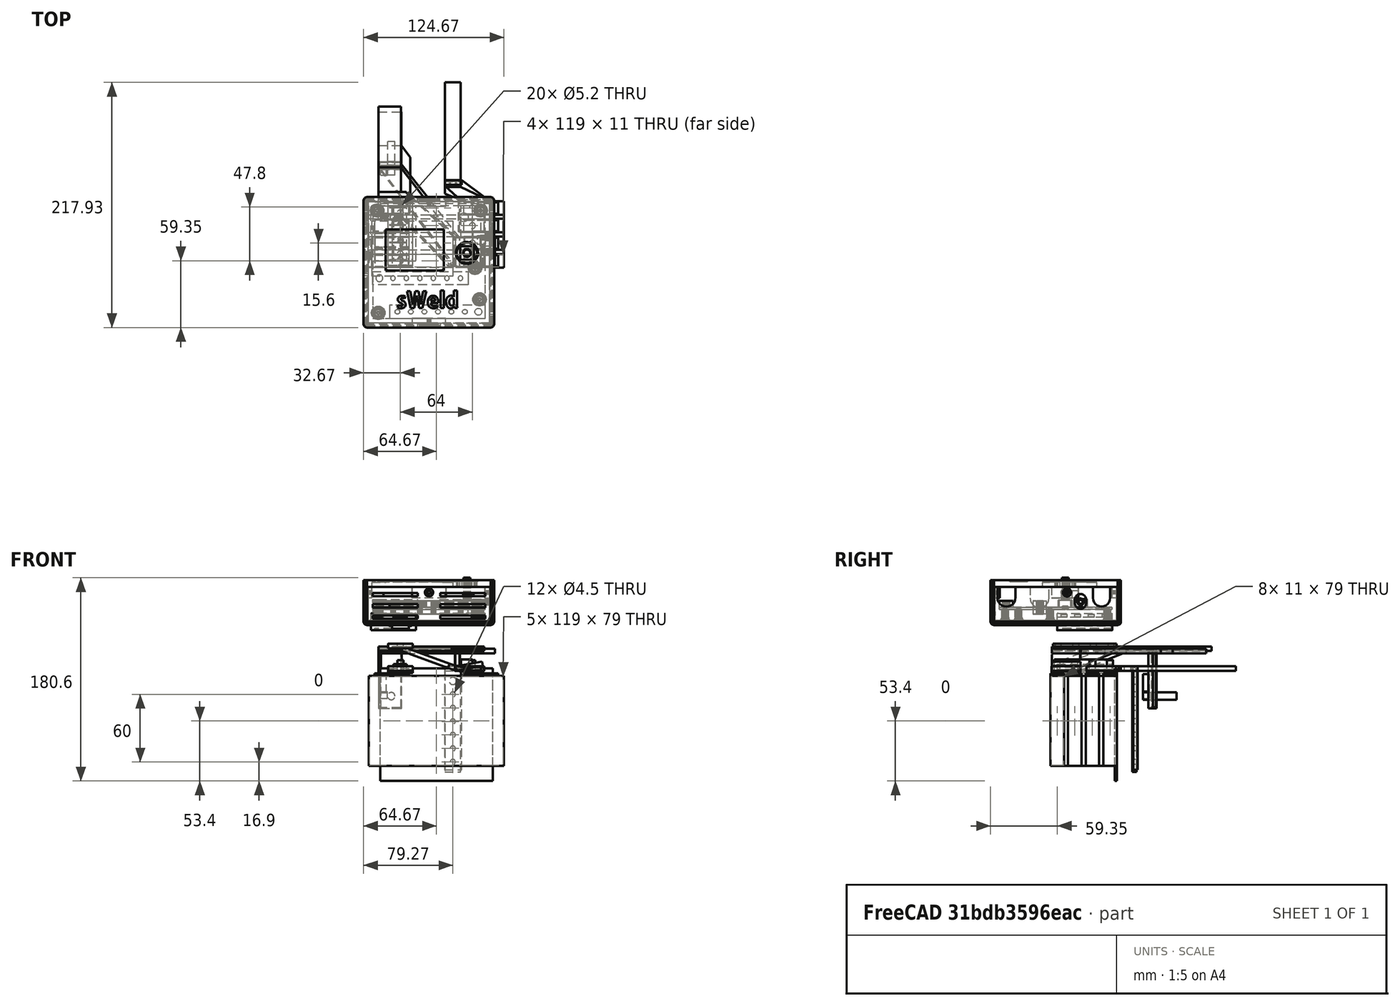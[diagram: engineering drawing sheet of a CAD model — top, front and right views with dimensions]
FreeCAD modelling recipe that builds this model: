
FCSTD DOCUMENT  (FreeCAD 0.17R13541 (Git))
Label: stm32welder-3d
License: CreativeCommons Attribution-NonCommercial-ShareAlike
LicenseURL: http://creativecommons.org/licenses/by-nc-sa/4.0/
objects: Drawing::FeatureViewPython×114, Part::Feature×45, Part::Box×32, Drawing::FeatureViewPart×32, Part::FeaturePython×13, Part::Fillet×11, Part::MultiFuse×11, Drawing::FeaturePage×10, Part::Cylinder×7, Part::Cut×6, Raytracing::RayFeature×5, App::DocumentObjectGroup×4, Part::Chamfer×4, Sketcher::SketchObject×3, App::Part×2, Raytracing::RayProject×1
note: 132 computed .brp shape members not serialized (recipe doc carries the construction recipe); baked Part::Feature solids carry a one-line shape summary decoded from their .brp

FEATURE [Part::Box] Box  label="立方体"
  AttacherType = Attacher::AttachEngine3D
  Height = 80
  Length = 120
  Placement = pos=(-84.5,0,-80) rot=(0,0,1;0rad)
  Width = 12
FEATURE [Part::Box] Box001  label="dianpian"
  AttacherType = Attacher::AttachEngine3D
  Height = 2.25
  Length = 30.5
  Width = 12
FEATURE [Part::Box] Box002  label="dianpian001"
  AttacherType = Attacher::AttachEngine3D
  Height = 2.25
  Length = 15
  Placement = pos=(0,0,2.25) rot=(0,0,1;0rad)
  Width = 12
FEATURE [Part::Fillet] Fillet
  Base = -> Box002
  Edges = 2 edges r=2: [Edge2,Edge6]
FEATURE [Part::Cylinder] Cylinder  label="圆柱体"
  Angle = 360
  AttacherType = Attacher::AttachEngine3D
  Height = 10
  Placement = pos=(7.5,6,4.5) rot=(0,0,1;0rad)
  Radius = 2.7
FEATURE [Part::MultiFuse] Fusion001  label="电极001"
  Placement = pos=(-24.5,12,80) rot=(0,0,1;3.14159rad)
  Shapes = -> [Fillet,Box001,Cylinder]
FEATURE [Part::Box] Box003  label="立方体001"
  AttacherType = Attacher::AttachEngine3D
  Height = 3.3
  Length = 22
  Placement = pos=(-43,-0.2,84.5) rot=(0,0,1;0rad)
  Width = 49
FEATURE [Part::Fillet] Fillet001
  Base = -> Box003
  Edges = 4 edges r=1: [Edge1,Edge3,Edge5,Edge7]
FEATURE [Part::Fillet] Fillet002
  Base = -> Box
  Edges = 12 edges r=0.5: [Edge1,Edge2,Edge3,Edge4,Edge5,Edge6,Edge7,Edge8,Edge9,Edge10,Edge11,Edge12]
FEATURE [Part::MultiFuse] Fusion  label="电极2"
  Placement = pos=(24.5,0,80) rot=(0,0,1;0rad)
  Shapes = -> [Fillet,Box001,Cylinder,Fillet002]
FEATURE [Part::Cylinder] Cylinder001  label="圆柱体001"
  Angle = 360
  AttacherType = Attacher::AttachEngine3D
  Height = 10
  Placement = pos=(7.5,6,4.5) rot=(0,0,1;0rad)
  Radius = 2.7
FEATURE [Part::MultiFuse] Fusion002  label="1201280"
  Shapes = -> [Fusion,Fusion001,Cylinder001]
FEATURE [Part::FeaturePython] Array  # Draft array (typed FeaturePython)
  Angle = 360
  ArrayType = 0
  Axis = (0,0,1)
  Base = -> Fusion002
  Center = (0,0,0)
  Fuse = false
  IntervalAxis = (0,0,0)
  IntervalX = (1,0,0)
  IntervalY = (0,12.2,0)
  IntervalZ = (0,0,0)
  NumberPolar = 1
  NumberX = 1
  NumberY = 4
  NumberZ = 1
FEATURE [Part::Box] Box004  label="立方体002"
  AttacherType = Attacher::AttachEngine3D
  Height = 8
  Length = 11.5
  Placement = pos=(-38,-0.2,84.5) rot=(0,0,1;0rad)
  Width = 49
FEATURE [Part::Box] Box005  label="立方体003"
  AttacherType = Attacher::AttachEngine3D
  Height = 3
  Length = 15
  Placement = pos=(-39.5,-0.2,82) rot=(0,0,1;0rad)
  Width = 49
FEATURE [Part::MultiFuse] Fusion002005
  Shapes = -> [Box005,Box004,Fillet001]
FEATURE [Part::MultiFuse] Fusion002006
  Shapes = -> [Array,Fusion002005]
FEATURE [Part::Box] Box006  label="立方体004"
  AttacherType = Attacher::AttachEngine3D
  Height = 15
  Length = 40
  Placement = pos=(-58,-0.2,80.5) rot=(0,0,1;0rad)
  Width = 49
FEATURE [Part::Fillet] Fillet003
  Base = -> Box006
  Edges = 4 edges r=1: [Edge1,Edge3,Edge5,Edge7]
FEATURE [Part::Cut] Cut
  Base = -> Fillet003
  Tool = -> Fusion002006
FEATURE [Part::Box] Box007  label="电极片"
  AttacherType = Attacher::AttachEngine3D
  Height = 2.25
  Length = 30.5
  Placement = pos=(24.5,-6,40) rot=(0,0,1;0rad)
  Width = 12
FEATURE [Part::Box] Box008  label="dianpian003"
  AttacherType = Attacher::AttachEngine3D
  Height = 2.25
  Length = 15
  Placement = pos=(24.5,-5,42.25) rot=(0,0,1;0rad)
  Width = 10
FEATURE [Part::Fillet] Fillet004  label="小垫片"
  Base = -> Box008
  Edges = 2 edges r=2: [Edge2,Edge6]
FEATURE [Part::Cylinder] Cylinder002  label="圆柱体002"
  Angle = 360
  AttacherType = Attacher::AttachEngine3D
  Height = 10
  Placement = pos=(32,0,44) rot=(0,0,1;0rad)
  Radius = 2.6
FEATURE [Part::Box] Box009  label="立方体005"
  AttacherType = Attacher::AttachEngine3D
  Height = 80
  Length = 120
  Placement = pos=(-60,-6,-40) rot=(0,0,1;0rad)
  Width = 12
FEATURE [Part::Fillet] Fillet005  label="1280120"
  Base = -> Box009
  Edges = 12 edges r=0.5: [Edge1,Edge2,Edge3,Edge4,Edge5,Edge6,Edge7,Edge8,Edge9,Edge10,Edge11,Edge12]
FEATURE [Part::Box] Box010  label="立方体006"
  AttacherType = Attacher::AttachEngine3D
  Height = 3.3
  Length = 22
  Placement = pos=(-43,-0.2,84.5) rot=(0,0,1;0rad)
  Width = 49
FEATURE [Part::Fillet] Fillet006
  Base = -> Box010
  Edges = 4 edges r=1: [Edge1,Edge3,Edge5,Edge7]
FEATURE [Part::Box] Box011  label="立方体007"
  AttacherType = Attacher::AttachEngine3D
  Height = 8
  Length = 11.5
  Placement = pos=(-38,-0.2,84.5) rot=(0,0,1;0rad)
  Width = 49
FEATURE [Part::Box] Box012  label="立方体008"
  AttacherType = Attacher::AttachEngine3D
  Height = 3
  Length = 15
  Placement = pos=(-39.5,-0.2,82) rot=(0,0,1;0rad)
  Width = 49
FEATURE [Part::MultiFuse] Fusion002007
  Placement = pos=(0,0,-42) rot=(0,0,1;0rad)
  Shapes = -> [Box012,Box011,Fillet006]
FEATURE [Part::Box] Box015  label="电极片001"
  AttacherType = Attacher::AttachEngine3D
  Height = 2.25
  Length = 30
  Placement = pos=(24.75,-5,40.1) rot=(0,0,1;0rad)
  Width = 10
FEATURE [Part::Box] Box016  label="电极片002"
  AttacherType = Attacher::AttachEngine3D
  Height = 2.25
  Length = 30.5
  Placement = pos=(-55,-6,40) rot=(0,0,1;0rad)
  Width = 12
FEATURE [Part::Box] Box017  label="dianpian004"
  AttacherType = Attacher::AttachEngine3D
  Height = 2.25
  Length = 15
  Placement = pos=(-39.5,-5,42.25) rot=(0,0,1;0rad)
  Width = 10
FEATURE [Part::Fillet] Fillet007  label="小垫片001"
  Base = -> Box017
  Edges = 2 edges r=2: [Edge2,Edge6]
FEATURE [Part::Cylinder] Cylinder003  label="圆柱体003"
  Angle = 360
  AttacherType = Attacher::AttachEngine3D
  Height = 10
  Placement = pos=(-32,0,44) rot=(0,0,1;0rad)
  Radius = 2.6
FEATURE [Part::Box] Box018  label="电极片003"
  AttacherType = Attacher::AttachEngine3D
  Height = 2.25
  Length = 30
  Placement = pos=(-54.75,-5,40.1) rot=(0,0,1;0rad)
  Width = 10
FEATURE [App::DocumentObjectGroup] ___  label="垫片1"
  Group = -> [Fillet004,Box015,Cylinder002,Box007]
FEATURE [App::DocumentObjectGroup] ___001  label="垫片"
  Group = -> [Fillet007,Box018,Cylinder003,Box016]
FEATURE [Part::Box] Box019  label="立方体009"
  AttacherType = Attacher::AttachEngine3D
  Height = 80
  Length = 120
  Placement = pos=(-60,-6,-40) rot=(0,0,1;0rad)
  Width = 58.7
FEATURE [Part::Feature] Fusion002008001  label="Fusion002009"
  shape: bbox 120 x 12 x 94 mm, 57 faces (baked)
FEATURE [Part::FeaturePython] Array001  # Draft array (typed FeaturePython)
  Angle = 360
  ArrayType = 0
  Axis = (0,0,1)
  Base = -> Fusion002008001
  Center = (0,0,0)
  Fuse = false
  IntervalAxis = (0,0,0)
  IntervalX = (1,0,0)
  IntervalY = (0,15.6,0)
  IntervalZ = (0,0,0)
  NumberPolar = 1
  NumberX = 1
  NumberY = 4
  NumberZ = 1
FEATURE [Part::Feature] Fusion002008002  label="Fusion002010"
  Placement = pos=(0,0,0) rot=(0,0,1;3.14159rad)
  shape: bbox 120 x 12 x 94 mm, 57 faces (baked)
FEATURE [Part::Feature] Fusion002008003  label="Fusion002011"
  Placement = pos=(0,15.6,0) rot=(0,0,1;3.14159rad)
  shape: bbox 120 x 12 x 94 mm, 57 faces (baked)
FEATURE [Part::Feature] Fusion002008004  label="Fusion002012"
  Placement = pos=(0,31.2,0) rot=(0,0,1;0rad)
  shape: bbox 120 x 12 x 94 mm, 57 faces (baked)
FEATURE [Part::Feature] Fusion002008005  label="Fusion002013"
  Placement = pos=(0,46.8,0) rot=(0,0,1;0rad)
  shape: bbox 120 x 12 x 94 mm, 57 faces (baked)
FEATURE [Raytracing::RayFeature] Fusion002008002_View
  Result = <blob: 50830 chars omitted>
  Source = -> Fusion002008002
  Transparency = 0
FEATURE [Raytracing::RayFeature] Fusion002008003_View
  Result = <blob: 51430 chars omitted>
  Source = -> Fusion002008003
  Transparency = 0
FEATURE [Raytracing::RayFeature] Fusion002008004_View
  Result = <blob: 48512 chars omitted>
  Source = -> Fusion002008004
  Transparency = 0
FEATURE [Raytracing::RayFeature] Fusion002008005_View
  Result = <blob: 48514 chars omitted>
  Source = -> Fusion002008005
  Transparency = 0
FEATURE [Raytracing::RayFeature] Box019_View
  Result = <blob: 2730 chars omitted>
  Source = -> Box019
  Transparency = 0
FEATURE [Raytracing::RayProject] PovProject
  Camera = // declares position and view direction\n\n// Generated by FreeCAD (http://www.freecadweb.org/)\n#declare cam_location =  <-28.5232,128.515,-118.34>;\n#declare cam_look_at  = <-1.61992,1.61848,13.5845>;\n#declare cam_sky      = <0.137048,0.727723,0.672039>;\n#declare cam_angle    = 45; \ncamera {\n  location  cam_location\n  look_at   cam_look_at\n  sky       cam_sky\n  angle     cam_angle \n  right x*2560/1920\n}
  Group = -> [Fusion002008002_View,Fusion002008003_View,Fusion002008004_View,Fusion002008005_View,Box019_View]
  Template = <path>
FEATURE [Part::Feature] Part__Feature  label="PCB-1"
  Placement = pos=(-56.6699,-51.3757,99.2) rot=(0,0,1;0rad)
  shape: bbox 100 x 100 x 1.6 mm, 576 faces (baked)
FEATURE [Part::Feature] Part__Feature001  label="300A\X2\4fdd9669\X0\-1"
  Placement = pos=(-47.0399,30.0255,103.8) rot=(0,0,1;0rad)
  shape: bbox 80.8 x 19.2 x 9 mm, 223 faces, 0 solids (baked)
FEATURE [Part::Feature] Part__Feature002  label="铜条1"
  Placement = pos=(28.3301,-21.5457,106.8) rot=(0,0.707107,-0.707107;3.14159rad)
  shape: bbox 85 x 12 x 6 mm, 478 faces (baked)
FEATURE [Part::Feature] Part__Feature003  label="铜条2"
  Placement = pos=(-41.6699,-51.3757,100.8) rot=(1,0,0;1.5708rad)
  shape: bbox 85 x 12 x 6 mm, 478 faces (baked)
FEATURE [Part::Feature] Part__Feature004  label="cross recessed hex bolts indentation gb-1"
  Placement = pos=(37.3301,-45.3757,114.971) rot=(0.367338,0.854474,-0.367338;1.72742rad)
  shape: bbox 11.23 x 11.07 x 14 mm, 1805 faces, 0 solids (baked)
FEATURE [Part::Feature] Part__Feature005  label="cross recessed hex bolts indentation gb-2"
  Placement = pos=(-50.6699,-15.5457,113.264) rot=(-0.550865,0.626973,0.550865;2.02156rad)
  shape: bbox 10.66 x 11.45 x 14 mm, 1805 faces, 0 solids (baked)
FEATURE [Part::Feature] Part__Feature006  label="plain washers-xl series-grade c1 gb-1"
  Placement = pos=(24.3601,38.5743,103.8) rot=(0,0,1;0.568241rad)
  shape: bbox 19.99 x 19.99 x 3 mm, 244 faces, 0 solids (baked)
FEATURE [Part::Feature] Part__Feature007  label="plain washers-xl series-grade c1 gb-2"
  Placement = pos=(-36.8399,38.5743,103.8) rot=(0,0,1;0rad)
  shape: bbox 19.99 x 19.99 x 3 mm, 244 faces, 0 solids (baked)
FEATURE [Part::Feature] Part__Feature008  label="18mm\X2\94dc67f1\X0\-1"
  Placement = pos=(-49.2499,-6.10568,100.8) rot=(1,0,0;1.5708rad)
  shape: bbox 4.33 x 5 x 18 mm, 90 faces, 0 solids (baked)
FEATURE [Part::Feature] Part__Feature009  label="18mm\X2\94dc67f1\X0\-2"
  Placement = pos=(-49.2499,24.8943,100.8) rot=(1,0,0;1.5708rad)
  shape: bbox 4.33 x 5 x 18 mm, 90 faces, 0 solids (baked)
FEATURE [Part::Feature] Part__Feature010  label="18mm\X2\94dc67f1\X0\-3"
  Placement = pos=(10.7501,-6.10568,100.8) rot=(1,0,0;1.5708rad)
  shape: bbox 4.33 x 5 x 18 mm, 90 faces, 0 solids (baked)
FEATURE [Part::Feature] Part__Feature011  label="18mm\X2\94dc67f1\X0\-4"
  Placement = pos=(10.7501,24.8943,100.8) rot=(1,0,0;1.5708rad)
  shape: bbox 4.33 x 5 x 18 mm, 90 faces, 0 solids (baked)
FEATURE [Part::Feature] Part__Feature012  label="外壳"
  Placement = pos=(-56.6699,-51.6162,89.2) rot=(0,0,1;0rad)
  shape: bbox 116 x 116 x 34 mm, 3868 faces (baked)
FEATURE [Part::Feature] Part__Feature013  label="盖子"
  Placement = pos=(-64.6699,-59.3507,119.2) rot=(1,0,0;1.5708rad)
  shape: bbox 116 x 116 x 16 mm, 1294 faces (baked)
FEATURE [Part::Feature] Part__Feature014  label="2.0IPS-2"
  Placement = pos=(-52.2499,-10.1057,118.8) rot=(1,0,0;1.5708rad)
  shape: bbox 66 x 39 x 3.8 mm, 322 faces, 0 solids (baked)
FEATURE [Part::Feature] Part__Feature015  label="EC11-2"
  Placement = pos=(21.1801,0.954319,100.8) rot=(1,0,0;1.5708rad)
  shape: bbox 12 x 12 x 26.4 mm, 312 faces (baked)
FEATURE [Part::Feature] Part__Feature016  label="编码开关帽"
  Placement = pos=(27.1801,6.95432,115.2) rot=(0.098915,0.703639,0.703639;2.9444rad)
  shape: bbox 19.8 x 19.79 x 22.36 mm, 3852 faces, 0 solids (baked)
FEATURE [Part::Feature] Part__Feature017  label="hex flange bolts-heavy grade b gb-1"
  Placement = pos=(-36.8399,38.5743,115.068) rot=(0.395904,0.828566,-0.395904;1.75776rad)
  shape: bbox 14.19 x 14.19 x 18.6 mm, 3036 faces, 0 solids (baked)
FEATURE [Part::Feature] Part__Feature018  label="hex flange bolts-heavy grade b gb-2"
  Placement = pos=(24.3601,38.5743,115.493) rot=(-0.329414,0.884858,0.329414;1.69282rad)
  shape: bbox 14.2 x 14.19 x 18.6 mm, 3036 faces, 0 solids (baked)
FEATURE [Part::Feature] Part__Feature019  label="SC16-6-1"
  Placement = pos=(-70.1441,38.5743,110.61) rot=(0.57735,0.57735,0.57735;2.0944rad)
  shape: bbox 43.96 x 13 x 9 mm, 516 faces, 0 solids (baked)
FEATURE [Part::Feature] Part__Feature020  label="SC16-6-2"
  Placement = pos=(57.6643,38.5743,110.61) rot=(0.57735,-0.57735,-0.57735;2.0944rad)
  shape: bbox 43.96 x 13 x 9 mm, 516 faces, 0 solids (baked)
FEATURE [Part::Feature] Part__Feature021  label="SC16-6-4"
  Placement = pos=(-83.9741,-15.5457,110.61) rot=(0.57735,0.57735,0.57735;2.0944rad)
  shape: bbox 43.96 x 13 x 9 mm, 516 faces, 0 solids (baked)
FEATURE [Part::Feature] Part__Feature022  label="SC16-6-6"
  Placement = pos=(70.6343,-45.3757,110.61) rot=(0.57735,-0.57735,-0.57735;2.0944rad)
  shape: bbox 43.96 x 13 x 9 mm, 516 faces, 0 solids (baked)
FEATURE [Part::Feature] Part__Feature023  label="3F06-2"
  Placement = pos=(43.3301,26.6243,103.3) rot=(0.57735,-0.57735,-0.57735;2.0944rad)
  shape: bbox 14.3 x 12 x 7.998 mm, 182 faces (baked)
FEATURE [Part::MultiFuse] Fusion002008006  label="电池组"
  Shapes = -> [Fusion002008005,Fusion002008004,Fusion002008003,Fusion002008002,Box019]
FEATURE [Part::Feature] Part__Feature024  label="铜条003"
  Placement = pos=(28.3301,-21.55,101) rot=(0,0.707107,-0.707107;3.14159rad)
  shape: bbox 85 x 12 x 6 mm, 478 faces (baked)
FEATURE [App::Part] _X2_9ed88ba4_X0_
  Group = -> [Part__Feature,Part__Feature001,Part__Feature002,Part__Feature003,Part__Feature004,Part__Feature005,Part__Feature006,Part__Feature007,Part__Feature008,Part__Feature009,Part__Feature010,Part__Feature011,Part__Feature012,Part__Feature013,Part__Feature014,Part__Feature015,Part__Feature016,Part__Feature017,Part__Feature018,Part__Feature019,Part__Feature020,Part__Feature021,Part__Feature022,+2 more]
  License = CC BY 3.0
  LicenseURL = http://creativecommons.org/licenses/by/3.0/
  Origin = -> Origin
FEATURE [App::Part] STM32
  Group = -> [_X2_9ed88ba4_X0_]
  License = CC BY 3.0
  LicenseURL = http://creativecommons.org/licenses/by/3.0/
  Origin = -> Origin001
  Placement = pos=(-1,-24,-15) rot=(-0.57735,0.57735,0.57735;2.0944rad)
FEATURE [Part::Box] Box020  label="立方体010"
  AttacherType = Attacher::AttachEngine3D
  Height = 4
  Length = 22
  Placement = pos=(-43,-5,44.5) rot=(0,0,1;0rad)
  Width = 56.7
FEATURE [Part::Fillet] Fillet008  label="串连铜排"
  Base = -> Box020
  Edges = 4 edges r=1: [Edge1,Edge3,Edge5,Edge7]
FEATURE [Part::Box] Box021  label="testpcb"
  AttacherType = Attacher::AttachEngine3D
  Height = 100
  Length = 100
  Placement = pos=(-50,51,-53.4) rot=(0,0,1;0rad)
  Width = 2
FEATURE [Part::Box] Box022  label="立方体011"
  AttacherType = Attacher::AttachEngine3D
  Height = 4
  Length = 22
  Placement = pos=(20.5,26.2,44.5) rot=(0,0,1;0rad)
  Width = 28.35
FEATURE [Part::Fillet] Fillet009  label="负极"
  Base = -> Box022
  Edges = 2 edges r=1: [Edge1,Edge5]
FEATURE [Part::Box] Box023  label="负极1"
  AttacherType = Attacher::AttachEngine3D
  Height = 4
  Length = 35
  Placement = pos=(7.5,54.5,44.5) rot=(0,0,1;0rad)
  Width = 11
FEATURE [Part::Box] Box024  label="负极002"
  AttacherType = Attacher::AttachEngine3D
  Height = 92
  Length = 15
  Placement = pos=(7.5,67.5,-43.5) rot=(0,0,1;0rad)
  Width = 4
FEATURE [Part::Box] Box025  label="正"
  AttacherType = Attacher::AttachEngine3D
  Height = 4
  Length = 22
  Placement = pos=(20.5,-4.9,44.5) rot=(0,0,1;0rad)
  Width = 25.5
FEATURE [Part::Box] Box026  label="负极003"
  AttacherType = Attacher::AttachEngine3D
  Height = 4
  Length = 66
  Placement = pos=(-50.2,-4.9,60) rot=(0,0,1;0rad)
  Width = 87.48
FEATURE [Part::Chamfer] Chamfer001  label="正001"
  Base = -> Box026
  Edges = 2 edges: [Edge1 r1=85.85 r2=64.7,Edge7 r1=62.2 r2=47]
FEATURE [Part::Box] Box027  label="正002"
  AttacherType = Attacher::AttachEngine3D
  Height = 15.6
  Length = 4
  Placement = pos=(16.5,-4.9,44.5) rot=(0,0,1;0rad)
  Width = 25.6
FEATURE [Part::Box] Box028  label="正003"
  AttacherType = Attacher::AttachEngine3D
  Height = 53
  Length = 18.5
  Placement = pos=(-49.2,81,11) rot=(0,0,1;0rad)
  Width = 4
FEATURE [Part::Cylinder] Cylinder004  label="圆柱体004"
  Angle = 360
  AttacherType = Attacher::AttachEngine3D
  Height = 20
  Radius = 2.25
FEATURE [Part::FeaturePython] Array002  # Draft array (typed FeaturePython)
  Angle = 360
  ArrayType = 0
  Axis = (0,0,1)
  Base = -> Cylinder004
  Center = (0,0,0)
  Fuse = false
  IntervalAxis = (0,0,0)
  IntervalX = (1,0,0)
  IntervalY = (0,12,0)
  IntervalZ = (0,0,0)
  NumberPolar = 1
  NumberX = 1
  NumberY = 6
  NumberZ = 1
FEATURE [Part::Cylinder] Cylinder005  label="圆柱体005"
  Angle = 360
  AttacherType = Attacher::AttachEngine3D
  Height = 20
  Placement = pos=(0,72,0) rot=(0,0,1;0rad)
  Radius = 3.25
FEATURE [Part::MultiFuse] Fusion002008007
  Placement = pos=(14.6,85,-36.5) rot=(1,0,0;1.5708rad)
  Shapes = -> [Cylinder005,Array002]
FEATURE [Part::Feature] Fusion002008006001  label="电池组切割"
  shape: bbox 120 x 58.8 x 94 mm, 234 faces (baked)
FEATURE [Part::MultiFuse] Fusion002008006002  label="开孔"
  Shapes = -> [Fusion002008007,Fusion002008006001]
FEATURE [Part::Feature] Cut001001  label="串联铜排"
  shape: bbox 22 x 56.7 x 4 mm, 18 faces (baked)
FEATURE [Part::MultiFuse] Fusion002008006003  label="负001"
  Shapes = -> [Box024,Fillet009]
FEATURE [App::DocumentObjectGroup] ___003  label="负"
  Group = -> [Fusion002008006003]
FEATURE [Part::Box] Box029  label="立方体012"
  AttacherType = Attacher::AttachEngine3D
  Height = 6
  Length = 6
  Placement = pos=(-49.5,76,20) rot=(0,0,1;0rad)
  Width = 5.7
FEATURE [Part::Box] Box030  label="立方体013"
  AttacherType = Attacher::AttachEngine3D
  Height = 16.7
  Length = 5
  Placement = pos=(-49.5,76,25) rot=(0,0,1;0rad)
  Width = 5.7
FEATURE [Part::Cylinder] Cylinder006  label="保险位置开孔"
  Angle = 360
  AttacherType = Attacher::AttachEngine3D
  Height = 30
  Placement = pos=(-40.1,76,22) rot=(-1,0,0;1.5708rad)
  Radius = 3.25
FEATURE [Part::Box] Box031  label="立方体014"
  AttacherType = Attacher::AttachEngine3D
  Height = 14.6
  Length = 10
  Placement = pos=(22,-2.6,40) rot=(0,0,1;0rad)
  Width = 51.7
FEATURE [Part::Feature] Fusion002008006003002001  label="正005"
  shape: bbox 91.7 x 89.9 x 53.1 mm, 32 faces (baked)
FEATURE [Part::Feature] Fusion002008006003002002001  label="开孔002"
  shape: bbox 120 x 112 x 94 mm, 237 faces, 2 solids (baked)
FEATURE [Part::Feature] Cut001002002_solid  label="正极"
  shape: bbox 91.7 x 89.9 x 53.1 mm, 37 faces (baked)
FEATURE [Part::Feature] Fusion002008006003002002002  label="负002"
  shape: bbox 35 x 45.3 x 92 mm, 24 faces (baked)
FEATURE [Part::Cut] Cut001002
  Base = -> Fusion002008006003002002002
  Tool = -> Fusion002008006002
FEATURE [Drawing::FeatureViewPart] Ortho  label="Ortho_0_0"
  Direction = (0,0,1)
  HiddenWidth = 0.15
  LineWidth = 0.35
  Rotation = 0
  Scale = 3
  ShowHiddenLines = false
  ShowSmoothLines = false
  Source = -> Cut001001
  Tolerance = 0.05
  ViewResult = <g id="Ortho_0_0"\n   transform="rotate(0,239,240.367) translate(239,240.367) scale(3,3)"\n  >\n<g   fill="none"\n   stroke="rgb(0, 0, 0)"\n   stroke-linecap="butt"\n   stroke-linejoin="miter"\n   stroke-width="0.116667"\n   transform="scale(1,-1)"\n  >\n<path id= "1" d=" M -43 -4 L -43 50.7 " />\n<path d="M-43 -4 A1 1 0 0 1 -42 -5" /><path d="M-43 50.7 A1 1 0 0 0 -42 51.7" /><path id= "4" d=" M -42 -5 L -22 -5 " />\n<path id= "5" d=" M -42 51.7 L -22 51.7 " />\n<path d="M-21 -4 A1 1 0 0 0 -22 -5" /><path d="M-21 50.7 A1 1 0 0 1 -22 51.7" /><path id= "8" d=" M -21 -4 L -21 50.7 " />\n<circle cx ="-32" cy ="3.92e-15" r ="2.6" /><circle cx ="-32" cy ="15.6" r ="2.6" /><circle cx ="-32" cy ="46.8" r ="2.6" /><circle cx ="-32" cy ="31.2" r ="2.6" /></g>\n</g>
  Visible = false
  X = 239
  Y = 240.367
FEATURE [Drawing::FeatureViewPart] Ortho001  label="Ortho_-1_0"
  Direction = (-1,0,0)
  HiddenWidth = 0.15
  LineWidth = 0.35
  Rotation = 180
  Scale = 3
  ShowHiddenLines = false
  ShowSmoothLines = false
  Source = -> Cut001001
  Tolerance = 0.05
  ViewResult = <g id="Ortho_-1_0"\n   transform="rotate(180,-79.5,240.367) translate(-79.5,240.367) scale(3,3)"\n  >\n<g   fill="none"\n   stroke="rgb(0, 0, 0)"\n   stroke-linecap="butt"\n   stroke-linejoin="miter"\n   stroke-width="0.116667"\n   transform="scale(1,-1)"\n  >\n<path id= "1" d=" M -48.5 4 L -48.5 -50.7 " />\n<path id= "2" d=" M -44.5 4 L -44.5 -50.7 " />\n<path d="M-48.5,4 Q-48.5,4.16942 -48.5,4.33028  Q-48.5,4.43541 -48.5,4.53203  Q-48.5,4.62569 -48.5,4.70711  Q-48.5,4.74447 -48.5,4.78183  Q-48.5,4.81428 -48.5,4.84672  Q-48.5,4.87385 -48.5,4.90097  Q-48.5,4.92243 -48.5,4.94388  Q-48.5,4.95941 -48.5,4.97493  Q-48.5,4.98432 -48.5,4.99371  Q-48.5,4.99686 -48.5,5 " /><path d="M-48.5,-50.7 Q-48.5,-50.8694 -48.5,-51.0303  Q-48.5,-51.1354 -48.5,-51.232  Q-48.5,-51.3257 -48.5,-51.4071  Q-48.5,-51.4445 -48.5,-51.4818  Q-48.5,-51.5143 -48.5,-51.5467  Q-48.5,-51.5738 -48.5,-51.601  Q-48.5,-51.6224 -48.5,-51.6439  Q-48.5,-51.6594 -48.5,-51.6749  Q-48.5,-51.6843 -48.5,-51.6937  Q-48.5,-51.6969 -48.5,-51.7 " /><path d="M-44.5,4 Q-44.5,4.16942 -44.5,4.33028  Q-44.5,4.43541 -44.5,4.53203  Q-44.5,4.62569 -44.5,4.70711  Q-44.5,4.74447 -44.5,4.78183  Q-44.5,4.81428 -44.5,4.84672  Q-44.5,4.87385 -44.5,4.90097  Q-44.5,4.92243 -44.5,4.94388  Q-44.5,4.95941 -44.5,4.97493  Q-44.5,4.98432 -44.5,4.99371  Q-44.5,4.99686 -44.5,5 " /><path id= "6" d=" M -44.5 5 L -48.5 5 " />\n<path d="M-44.5,-50.7 Q-44.5,-50.8694 -44.5,-51.0303  Q-44.5,-51.1354 -44.5,-51.232  Q-44.5,-51.3257 -44.5,-51.4071  Q-44.5,-51.4445 -44.5,-51.4818  Q-44.5,-51.5143 -44.5,-51.5467  Q-44.5,-51.5738 -44.5,-51.601  Q-44.5,-51.6224 -44.5,-51.6439  Q-44.5,-51.6594 -44.5,-51.6749  Q-44.5,-51.6843 -44.5,-51.6937  Q-44.5,-51.6969 -44.5,-51.7 " /><path id= "8" d=" M -44.5 -51.7 L -48.5 -51.7 " />\n</g>\n</g>
  Visible = false
  X = -79.5
  Y = 240.367
FEATURE [Drawing::FeatureViewPart] Ortho002  label="Ortho_0_1"
  Direction = (0,1,0)
  HiddenWidth = 0.15
  LineWidth = 0.35
  Rotation = 90
  Scale = 3
  ShowHiddenLines = false
  ShowSmoothLines = false
  Source = -> Cut001001
  Tolerance = 0.05
  ViewResult = <blob: 2357 chars omitted>
  Visible = false
  X = 239
  Y = -91.8667
FEATURE [Drawing::FeatureViewPython] dim001  # drawing view (typed FeaturePython)
  Rotation = 0
  ViewResult = <g> \n  <line x1="54.000000" y1="83.267000" x2="54.000000" y2="68.562284" style="stroke:rgb(0,0,255);stroke-width:0.30" />\n<line x1="66.000000" y1="83.267000" x2="66.000000" y2="68.562284" style="stroke:rgb(0,0,255);stroke-width:0.30" />\n<line x1="54.000000" y1="69.562284" x2="66.000000" y2="69.562284" style="stroke:rgb(0,0,255);stroke-width:0.30" /> \n  <polygon points="66.000000,69.562284 63.000000,68.562284 62.000000,69.562284 63.000000,70.562284" style="fill:rgb(0,0,255);stroke:rgb(0,0,255);stroke-width:0" /><polygon points="54.000000,69.562284 57.000000,70.562284 58.000000,69.562284 57.000000,68.562284" style="fill:rgb(0,0,255);stroke:rgb(0,0,255);stroke-width:0" /> \n  <text x="60.000000" y="67.562284" font-family="Verdana" font-size="3.6" fill="rgb(255,0,0)" text-anchor="middle" transform="rotate(0.000000 60.000000,67.562284)" >4</text> </g>
  Visible = false
  X = 0
  Y = 0
  arrowL1 = 3
  arrowL2 = 1
  arrowW = 2
  arrow_scheme = 0
  autoPlaceOffset = 2
  autoPlaceText = true
  click1_x = 58.398
  click1_y = 69.5623
  click2_x = 58.398
  click2_y = 69.5623
  comma_decimal_place = false
  dimension_line_overshoot = 1
  gap_datum_points = 2
  halfDimension_linear = false
  lineColor = rgb(0,0,255)
  strokeWidth = 0.3
  textFormat_linear = %(value)3.3f
  textRenderer_color = rgb(255,0,0)
  textRenderer_family = Verdana
  textRenderer_size = 3.6
  unit_custom_scale = 1
  unit_scheme = 0
FEATURE [Drawing::FeatureViewPython] dim002  # drawing view (typed FeaturePython)
  Rotation = 0
  ViewResult = <g> \n  <line x1="68.000000" y1="252.367000" x2="74.426855" y2="252.367000" style="stroke:rgb(0,0,255);stroke-width:0.30" />\n<line x1="68.000000" y1="88.267000" x2="74.426855" y2="88.267000" style="stroke:rgb(0,0,255);stroke-width:0.30" />\n<line x1="73.426855" y1="252.367000" x2="73.426855" y2="88.267000" style="stroke:rgb(0,0,255);stroke-width:0.30" /> \n  <polygon points="73.426855,88.267000 72.426855,91.267000 73.426855,92.267000 74.426855,91.267000" style="fill:rgb(0,0,255);stroke:rgb(0,0,255);stroke-width:0" /><polygon points="73.426855,252.367000 74.426855,249.367000 73.426855,248.367000 72.426855,249.367000" style="fill:rgb(0,0,255);stroke:rgb(0,0,255);stroke-width:0" /> \n  <text x="71.426855" y="170.317000" font-family="Verdana" font-size="3.6" fill="rgb(255,0,0)" text-anchor="middle" transform="rotate(-90.000000 71.426855,170.317000)" >54.7</text> </g>
  Visible = false
  X = 0
  Y = 0
  arrowL1 = 3
  arrowL2 = 1
  arrowW = 2
  arrow_scheme = 0
  autoPlaceOffset = 2
  autoPlaceText = true
  click1_x = 73.4269
  click1_y = 109.067
  click2_x = 73.4269
  click2_y = 109.067
  comma_decimal_place = false
  dimension_line_overshoot = 1
  gap_datum_points = 2
  halfDimension_linear = false
  lineColor = rgb(0,0,255)
  strokeWidth = 0.3
  textFormat_linear = %(value)3.3f
  textRenderer_color = rgb(255,0,0)
  textRenderer_family = Verdana
  textRenderer_size = 3.6
  unit_custom_scale = 1
  unit_scheme = 0
FEATURE [Drawing::FeatureViewPython] dia001  # drawing view (typed FeaturePython)
  Rotation = 0
  ViewResult = <g>  <circle cx ="113.000000" cy ="88.267000" r="0.500000" stroke="none" fill="rgb(0,0,255)" /> \n<line x1="100.192590" y1="71.566136" x2="114.825601" y2="90.647584" style="stroke:rgb(0,0,255);stroke-width:0.30" />\n<polygon points="111.174399,85.886416 110.142326,82.897298 108.740264,82.712304 108.555270,84.114366" style="fill:rgb(0,0,255);stroke:rgb(0,0,255);stroke-width:0" />\n<polygon points="114.825601,90.647584 115.857674,93.636702 117.259736,93.821696 117.444730,92.419634" style="fill:rgb(0,0,255);stroke:rgb(0,0,255);stroke-width:0" />\n<line x1="100.192590" y1="71.566136" x2="115.579310" y2="71.566136" style="stroke:rgb(0,0,255);stroke-width:0.30" />\n<text x="107.885950" y="69.566136" font-family="Verdana" font-size="3.6" fill="rgb(255,0,0)" text-anchor="middle" transform="rotate(0.000000 107.885950,69.566136)" >Ø2</text> </g>
  Visible = false
  X = 0
  Y = 0
  arrowL1 = 3
  arrowL2 = 1
  arrowW = 2
  arrow_scheme = 0
  autoPlaceOffset = 2
  autoPlaceText = true
  centerPointDia = 1
  click1_x = 100.193
  click1_y = 71.5661
  click2_x = 115.579
  click2_y = 80.5119
  click3_x = 115.579
  click3_y = 80.5119
  comma_decimal_place = false
  lineColor = rgb(0,0,255)
  strokeWidth = 0.3
  textFormat_circular = Ø%(value)3.3f
  textRenderer_color = rgb(255,0,0)
  textRenderer_family = Verdana
  textRenderer_size = 3.6
  unit_custom_scale = 1
  unit_scheme = 0
FEATURE [Drawing::FeatureViewPython] dia002  # drawing view (typed FeaturePython)
  Rotation = 0
  ViewResult = <g>  <circle cx ="173.000000" cy ="252.367000" r="0.500000" stroke="none" fill="rgb(0,0,255)" /> \n<line x1="187.861107" y1="260.142904" x2="170.341882" y2="250.976170" style="stroke:rgb(0,0,255);stroke-width:0.30" />\n<polygon points="175.658118,253.757830 177.852626,256.034699 179.202276,255.612270 178.779846,254.262620" style="fill:rgb(0,0,255);stroke:rgb(0,0,255);stroke-width:0" />\n<polygon points="170.341882,250.976170 168.147374,248.699301 166.797724,249.121730 167.220154,250.471380" style="fill:rgb(0,0,255);stroke:rgb(0,0,255);stroke-width:0" />\n<line x1="187.861107" y1="260.142904" x2="193.944228" y2="260.142904" style="stroke:rgb(0,0,255);stroke-width:0.30" />\n<text x="190.902668" y="258.142904" font-family="Verdana" font-size="3.6" fill="rgb(255,0,0)" text-anchor="middle" transform="rotate(0.000000 190.902668,258.142904)" >Ø2</text> </g>
  Visible = false
  X = 0
  Y = 0
  arrowL1 = 3
  arrowL2 = 1
  arrowW = 2
  arrow_scheme = 0
  autoPlaceOffset = 2
  autoPlaceText = true
  centerPointDia = 1
  click1_x = 187.861
  click1_y = 260.143
  click2_x = 193.944
  click2_y = 263.721
  click3_x = 193.944
  click3_y = 263.721
  comma_decimal_place = false
  lineColor = rgb(0,0,255)
  strokeWidth = 0.3
  textFormat_circular = Ø%(value)3.3f
  textRenderer_color = rgb(255,0,0)
  textRenderer_family = Verdana
  textRenderer_size = 3.6
  unit_custom_scale = 1
  unit_scheme = 0
FEATURE [Drawing::FeatureViewPython] dia003  # drawing view (typed FeaturePython)
  Rotation = 0
  ViewResult = <g>  <circle cx ="143.000000" cy ="99.967000" r="0.500000" stroke="none" fill="rgb(0,0,255)" /> \n<line x1="150.288885" y1="114.147987" x2="139.434308" y2="93.029721" style="stroke:rgb(0,0,255);stroke-width:0.30" />\n<polygon points="146.565692,106.904279 146.083667,103.778955 144.737132,103.346700 144.304877,104.693235" style="fill:rgb(0,0,255);stroke:rgb(0,0,255);stroke-width:0" />\n<polygon points="139.434308,93.029721 139.916333,96.155045 141.262868,96.587300 141.695123,95.240765" style="fill:rgb(0,0,255);stroke:rgb(0,0,255);stroke-width:0" />\n<line x1="150.288885" y1="114.147987" x2="163.170790" y2="114.147987" style="stroke:rgb(0,0,255);stroke-width:0.30" />\n<text x="156.729838" y="112.147987" font-family="Verdana" font-size="3.6" fill="rgb(255,0,0)" text-anchor="middle" transform="rotate(0.000000 156.729838,112.147987)" >Ø5.2</text> </g>
  Visible = false
  X = 0
  Y = 0
  arrowL1 = 3
  arrowL2 = 1
  arrowW = 2
  arrow_scheme = 0
  autoPlaceOffset = 2
  autoPlaceText = true
  centerPointDia = 1
  click1_x = 150.289
  click1_y = 114.148
  click2_x = 163.171
  click2_y = 115.221
  click3_x = 163.171
  click3_y = 115.221
  comma_decimal_place = false
  lineColor = rgb(0,0,255)
  strokeWidth = 0.3
  textFormat_circular = Ø%(value)3.3f
  textRenderer_color = rgb(255,0,0)
  textRenderer_family = Verdana
  textRenderer_size = 3.6
  unit_custom_scale = 1
  unit_scheme = 0
FEATURE [Drawing::FeatureViewPython] dim003  # drawing view (typed FeaturePython)
  Rotation = 0
  ViewResult = <g> \n  <line x1="141.000000" y1="99.967000" x2="125.314230" y2="99.967000" style="stroke:rgb(0,0,255);stroke-width:0.30" />\n<line x1="141.000000" y1="146.767000" x2="125.314230" y2="146.767000" style="stroke:rgb(0,0,255);stroke-width:0.30" />\n<line x1="126.314230" y1="99.967000" x2="126.314230" y2="146.767000" style="stroke:rgb(0,0,255);stroke-width:0.30" /> \n  <polygon points="126.314230,146.767000 127.314230,143.767000 126.314230,142.767000 125.314230,143.767000" style="fill:rgb(0,0,255);stroke:rgb(0,0,255);stroke-width:0" /><polygon points="126.314230,99.967000 125.314230,102.967000 126.314230,103.967000 127.314230,102.967000" style="fill:rgb(0,0,255);stroke:rgb(0,0,255);stroke-width:0" /> \n  <text x="124.314230" y="123.367000" font-family="Verdana" font-size="3.6" fill="rgb(255,0,0)" text-anchor="middle" transform="rotate(-90.000000 124.314230,123.367000)" >15.6</text> </g>
  Visible = false
  X = 0
  Y = 0
  arrowL1 = 3
  arrowL2 = 1
  arrowW = 2
  arrow_scheme = 0
  autoPlaceOffset = 2
  autoPlaceText = true
  click1_x = 126.314
  click1_y = 150.647
  click2_x = 126.314
  click2_y = 150.647
  comma_decimal_place = false
  dimension_line_overshoot = 1
  gap_datum_points = 2
  halfDimension_linear = false
  lineColor = rgb(0,0,255)
  strokeWidth = 0.3
  textFormat_linear = %(value)3.3f
  textRenderer_color = rgb(255,0,0)
  textRenderer_family = Verdana
  textRenderer_size = 3.6
  unit_custom_scale = 1
  unit_scheme = 0
FEATURE [Drawing::FeatureViewPython] dim004  # drawing view (typed FeaturePython)
  Rotation = 0
  ViewResult = <g> \n  <line x1="145.000000" y1="146.767000" x2="158.445499" y2="146.767000" style="stroke:rgb(0,0,255);stroke-width:0.30" />\n<line x1="145.000000" y1="193.567000" x2="158.445499" y2="193.567000" style="stroke:rgb(0,0,255);stroke-width:0.30" />\n<line x1="157.445499" y1="146.767000" x2="157.445499" y2="193.567000" style="stroke:rgb(0,0,255);stroke-width:0.30" /> \n  <polygon points="157.445499,193.567000 158.445499,190.567000 157.445499,189.567000 156.445499,190.567000" style="fill:rgb(0,0,255);stroke:rgb(0,0,255);stroke-width:0" /><polygon points="157.445499,146.767000 156.445499,149.767000 157.445499,150.767000 158.445499,149.767000" style="fill:rgb(0,0,255);stroke:rgb(0,0,255);stroke-width:0" /> \n  <text x="155.445499" y="170.167000" font-family="Verdana" font-size="3.6" fill="rgb(255,0,0)" text-anchor="middle" transform="rotate(-90.000000 155.445499,170.167000)" >15.6</text> </g>
  Visible = false
  X = 0
  Y = 0
  arrowL1 = 3
  arrowL2 = 1
  arrowW = 2
  arrow_scheme = 0
  autoPlaceOffset = 2
  autoPlaceText = true
  click1_x = 157.445
  click1_y = 174.264
  click2_x = 157.445
  click2_y = 174.264
  comma_decimal_place = false
  dimension_line_overshoot = 1
  gap_datum_points = 2
  halfDimension_linear = false
  lineColor = rgb(0,0,255)
  strokeWidth = 0.3
  textFormat_linear = %(value)3.3f
  textRenderer_color = rgb(255,0,0)
  textRenderer_family = Verdana
  textRenderer_size = 3.6
  unit_custom_scale = 1
  unit_scheme = 0
FEATURE [Drawing::FeatureViewPython] dim005  # drawing view (typed FeaturePython)
  Rotation = 0
  ViewResult = <g> \n  <line x1="141.000000" y1="193.567000" x2="127.103383" y2="193.567000" style="stroke:rgb(0,0,255);stroke-width:0.30" />\n<line x1="141.000000" y1="240.367000" x2="127.103383" y2="240.367000" style="stroke:rgb(0,0,255);stroke-width:0.30" />\n<line x1="128.103383" y1="193.567000" x2="128.103383" y2="240.367000" style="stroke:rgb(0,0,255);stroke-width:0.30" /> \n  <polygon points="128.103383,240.367000 129.103383,237.367000 128.103383,236.367000 127.103383,237.367000" style="fill:rgb(0,0,255);stroke:rgb(0,0,255);stroke-width:0" /><polygon points="128.103383,193.567000 127.103383,196.567000 128.103383,197.567000 129.103383,196.567000" style="fill:rgb(0,0,255);stroke:rgb(0,0,255);stroke-width:0" /> \n  <text x="126.103383" y="216.967000" font-family="Verdana" font-size="3.6" fill="rgb(255,0,0)" text-anchor="middle" transform="rotate(-90.000000 126.103383,216.967000)" >15.6</text> </g>
  Visible = false
  X = 0
  Y = 0
  arrowL1 = 3
  arrowL2 = 1
  arrowW = 2
  arrow_scheme = 0
  autoPlaceOffset = 2
  autoPlaceText = true
  click1_x = 128.103
  click1_y = 220.782
  click2_x = 128.103
  click2_y = 220.782
  comma_decimal_place = false
  dimension_line_overshoot = 1
  gap_datum_points = 2
  halfDimension_linear = false
  lineColor = rgb(0,0,255)
  strokeWidth = 0.3
  textFormat_linear = %(value)3.3f
  textRenderer_color = rgb(255,0,0)
  textRenderer_family = Verdana
  textRenderer_size = 3.6
  unit_custom_scale = 1
  unit_scheme = 0
FEATURE [Drawing::FeatureViewPython] centerLines001  # drawing view (typed FeaturePython)
  Rotation = 0
  ViewResult = <g transform="scale(3.000000,3.000000)" stroke="rgb(0,0,255)"  stroke-width="0.100000" > <path d="M 47.666667,28.422333 L 47.666667,29.089000 M 47.666667,29.755667 L 47.666667,31.755667 M 47.666667,32.422333 L 47.666667,33.089000 M 47.666667,33.755667 L 47.666667,35.755667 M 47.666667,36.422333 L 47.666667,37.089000 M 47.666667,37.755667 L 47.666667,39.755667 M 47.666667,40.422333 L 47.666667,41.089000 M 47.666667,41.755667 L 47.666667,43.755667 M 47.666667,44.422333 L 47.666667,45.089000 M 47.666667,45.755667 L 47.666667,47.755667 M 47.666667,48.422333 L 47.666667,49.089000 M 47.666667,49.755667 L 47.666667,51.755667 M 47.666667,52.422333 L 47.666667,53.089000 M 47.666667,53.755667 L 47.666667,55.755667 M 47.666667,56.422333 L 47.666667,57.089000 M 47.666667,57.755667 L 47.666667,59.755667 M 47.666667,60.422333 L 47.666667,61.089000 M 47.666667,61.755667 L 47.666667,63.755667 M 47.666667,64.422333 L 47.666667,65.089000 M 47.666667,65.755667 L 47.666667,67.755667 M 47.666667,68.422333 L 47.666667,69.089000 M 47.666667,69.755667 L 47.666667,71.755667 M 47.666667,72.422333 L 47.666667,73.089000 M 47.666667,73.755667 L 47.666667,75.755667 M 47.666667,76.422333 L 47.666667,77.089000 M 47.666667,77.755667 L 47.666667,79.755667 M 47.666667,80.422333 L 47.666667,81.089000 M 47.666667,81.755667 L 47.666667,83.755667 M 47.666667,84.422333 L 47.666667,85.089000 M 47.666667,85.755667 L 47.666667,87.755667 "/>\n<path d="M 47.666667,28.422333 L 47.666667,27.755667 M 47.666667,27.089000 L 47.666667,25.089000 "/> </g> 
  Visible = false
  X = 0
  Y = 0
  centerLine_color = rgb(0,0,255)
  centerLine_len_dash = 6
  centerLine_len_dot = 2
  centerLine_len_gap = 2
  centerLine_width = 0.3
  click1_x = 145.279
  click1_y = 263.721
  click2_x = 144.206
  click2_y = 73.3553
FEATURE [Drawing::FeatureViewPython] dimStack001  # drawing view (typed FeaturePython)
  Rotation = 0
  ViewResult = <g> <line x1="110.000000" y1="254.367000" x2="110.000000" y2="278.733860" style="stroke:rgb(0,0,255);stroke-width:0.30" />\n<line x1="176.000000" y1="254.367000" x2="176.000000" y2="278.733860" style="stroke:rgb(0,0,255);stroke-width:0.30" />\n<line x1="110.000000" y1="277.733860" x2="176.000000" y2="277.733860" style="stroke:rgb(0,0,255);stroke-width:0.30" />\n<polygon points="110.000000,277.733860 113.000000,278.733860 114.000000,277.733860 113.000000,276.733860" style="fill:rgb(0,0,255);stroke:rgb(0,0,255);stroke-width:0" />\n<polygon points="176.000000,277.733860 173.000000,276.733860 172.000000,277.733860 173.000000,278.733860" style="fill:rgb(0,0,255);stroke:rgb(0,0,255);stroke-width:0" />\n<text x="143.000000" y="275.733860" font-family="Verdana" font-size="3.6" fill="rgb(255,0,0)" text-anchor="middle" transform="rotate(0.000000 143.000000,275.733860)" >22</text> </g> 
  Visible = false
  X = 0
  Y = 0
  arrowL1 = 3
  arrowL2 = 1
  arrowW = 2
  arrow_scheme = 0
  autoPlaceOffset = 2
  click1_x = 175.709
  click1_y = 277.734
  comma_decimal_place = false
  dimension_line_overshoot = 1
  gap_datum_points = 2
  lineColor = rgb(0,0,255)
  stack_offset = 7
  stack_offset0 = 0
  strokeWidth = 0.3
  textFormat_linear = %(value)3.3f
  textRenderer_color = rgb(255,0,0)
  textRenderer_family = Verdana
  textRenderer_size = 3.6
  unit_custom_scale = 1
  unit_scheme = 0
FEATURE [Drawing::FeatureViewPython] dimStack002  # drawing view (typed FeaturePython)
  Rotation = 0
  ViewResult = <g> <line x1="111.000000" y1="255.367000" x2="89.688607" y2="255.367000" style="stroke:rgb(0,0,255);stroke-width:0.30" />\n<line x1="111.000000" y1="85.267000" x2="89.688607" y2="85.267000" style="stroke:rgb(0,0,255);stroke-width:0.30" />\n<line x1="90.688607" y1="255.367000" x2="90.688607" y2="85.267000" style="stroke:rgb(0,0,255);stroke-width:0.30" />\n<polygon points="90.688607,255.367000 91.688607,252.367000 90.688607,251.367000 89.688607,252.367000" style="fill:rgb(0,0,255);stroke:rgb(0,0,255);stroke-width:0" />\n<polygon points="90.688607,85.267000 89.688607,88.267000 90.688607,89.267000 91.688607,88.267000" style="fill:rgb(0,0,255);stroke:rgb(0,0,255);stroke-width:0" />\n<text x="88.688607" y="170.317000" font-family="Verdana" font-size="3.6" fill="rgb(255,0,0)" text-anchor="middle" transform="rotate(-90.000000 88.688607,170.317000)" >56.7</text> </g> 
  Visible = false
  X = 0
  Y = 0
  arrowL1 = 3
  arrowL2 = 1
  arrowW = 2
  arrow_scheme = 0
  autoPlaceOffset = 2
  click1_x = 90.6886
  click1_y = 104.601
  comma_decimal_place = false
  dimension_line_overshoot = 1
  gap_datum_points = 2
  lineColor = rgb(0,0,255)
  stack_offset = 7
  stack_offset0 = 0
  strokeWidth = 0.3
  textFormat_linear = %(value)3.3f
  textRenderer_color = rgb(255,0,0)
  textRenderer_family = Verdana
  textRenderer_size = 3.6
  unit_custom_scale = 1
  unit_scheme = 0
FEATURE [Drawing::FeaturePage] Page  label="chuanlian"
  EditableTexts = AUTHOR NAME | CREATION DATE | SUPERVISOR NAME | CHECK DATE | SCALE | WEIGHT | NUMBER | SHEET | TITLE | SUBTITLE
  Group = -> [Ortho,Ortho001,Ortho002,dim001,dim002,dia001,dia002,dia003,dim003,dim004,dim005,centerLines001,dimStack001,dimStack002]
  Template = <path>
FEATURE [Drawing::FeatureViewPart] Ortho003  label="Ortho_0_002"
  Direction = (1,0,0)
  HiddenWidth = 0.15
  LineWidth = 0.35
  Rotation = -90
  Scale = 0.8
  ShowHiddenLines = false
  ShowSmoothLines = false
  Source = -> Cut001002002_solid
  Tolerance = 0.05
  ViewResult = <g id="Ortho_0_002"\n   transform="rotate(-90,177.96,148.54) translate(177.96,148.54) scale(0.8,0.8)"\n  >\n<g   fill="none"\n   stroke="rgb(0, 0, 0)"\n   stroke-linecap="butt"\n   stroke-linejoin="miter"\n   stroke-width="0.437500"\n   transform="scale(1,-1)"\n  >\n<path id= "1" d=" M 11 -81 L 60 -81 " />\n<path id= "2" d=" M 64 -84.95 L 64 -85 " />\n<path id= "3" d=" M 11 -85 L 64 -85 " />\n<path id= "4" d=" M 11 -81 L 11 -85 " />\n<path id= "5" d=" M 60 -20.75 L 60 -84.95 " />\n<path id= "6" d=" M 60 -20.7 L 60 -20.75 " />\n<path id= "7" d=" M 60 -84.95 L 64 -84.95 " />\n<path id= "8" d=" M 60 -20.75 L 64 -20.75 " />\n<path id= "9" d=" M 64 -20.75 L 64 -84.95 " />\n<path id= "10" d=" M 64 -20.7 L 64 -20.75 " />\n<path id= "11" d=" M 60 -20.7 L 64 -20.7 " />\n<path id= "12" d=" M 44.5 -20.7 L 60 -20.7 " />\n<path id= "13" d=" M 64 4.9 L 64 -20.7 " />\n<path id= "14" d=" M 60 4.9 L 60 -20.7 " />\n<path id= "15" d=" M 60 4.9 L 64 4.9 " />\n<path id= "16" d=" M 48.5 4.9 L 60 4.9 " />\n<path id= "17" d=" M 44.5 -20.6 L 44.5 -20.7 " />\n<path id= "18" d=" M 64 -20.7 L 64.1 -20.7 " />\n<path id= "19" d=" M 64 4.9 L 64.1 4.9 " />\n<path id= "20" d=" M 64.1 4.9 L 64.1 -20.7 " />\n<path id= "21" d=" M 44.5 -20.6 L 48.5 -20.6 " />\n<path id= "22" d=" M 48.5 4.9 L 48.5 -20.6 " />\n<path id= "23" d=" M 44.5 4.9 L 44.5 -20.6 " />\n<path id= "24" d=" M 44.5 4.9 L 48.5 4.9 " />\n</g>\n</g>
  Visible = false
  X = 177.96
  Y = 148.54
FEATURE [Drawing::FeatureViewPart] Ortho004  label="Ortho_-1_001"
  Direction = (0,-1,0)
  HiddenWidth = 0.15
  LineWidth = 0.35
  Rotation = 90
  Scale = 0.8
  ShowHiddenLines = false
  ShowSmoothLines = false
  Source = -> Cut001002002_solid
  Tolerance = 0.05
  ViewResult = <g id="Ortho_-1_001"\n   transform="rotate(90,101.442,148.54) translate(101.442,148.54) scale(0.8,0.8)"\n  >\n<g   fill="none"\n   stroke="rgb(0, 0, 0)"\n   stroke-linecap="butt"\n   stroke-linejoin="miter"\n   stroke-width="0.437500"\n   transform="scale(1,-1)"\n  >\n<path id= "1" d=" M -11 -49.2 L -60 -49.2 " />\n<path id= "2" d=" M -11 -30.7 L -60 -30.7 " />\n<path id= "3" d=" M -11 -49.2 L -11 -30.7 " />\n<circle cx ="-22" cy ="-40.1" r ="3.25" /><path id= "5" d=" M -60 -49.2 L -60 16.5 " />\n<path id= "6" d=" M -60 -49.2 L -64 -49.2 " />\n<path id= "7" d=" M -44.5 16.5 L -60 16.5 " />\n<path id= "8" d=" M -60 16.5 L -64 16.5 " />\n<path id= "9" d=" M -64 -49.2 L -64 16.5 " />\n<path id= "10" d=" M -60 20.5 L -64 20.5 " />\n<path id= "11" d=" M -48.5 20.5 L -60 20.5 " />\n<path id= "12" d=" M -44.5 16.5 L -44.5 20.5 " />\n<path id= "13" d=" M -44.5 20.5 L -48.5 20.5 " />\n<path id= "14" d=" M -60 16.5 L -60 20.5 " />\n<path id= "15" d=" M -64 16.5 L -64 20.5 " />\n<path id= "16" d=" M -64 16.5 L -64.1 16.5 " />\n<path id= "17" d=" M -64 20.5 L -64.1 20.5 " />\n<path id= "18" d=" M -48.5 20.5 L -48.5 42.5 " />\n<path id= "19" d=" M -44.5 37.5 L -44.5 42.5 " />\n<path id= "20" d=" M -44.5 20.5 L -44.5 26.5 " />\n<path id= "21" d=" M -44.5 26.5 L -44.5 37.5 " />\n<path id= "22" d=" M -44.5 42.5 L -48.5 42.5 " />\n<path id= "23" d=" M -64.1 16.5 L -64.1 20.5 " />\n</g>\n</g>
  Visible = false
  X = 101.442
  Y = 148.54
FEATURE [Drawing::FeatureViewPart] Ortho005  label="Ortho_0_003"
  Direction = (0,0,1)
  HiddenWidth = 0.15
  LineWidth = 0.35
  Rotation = 90
  Scale = 0.8
  ShowHiddenLines = false
  ShowSmoothLines = false
  Source = -> Cut001002002_solid
  Tolerance = 0.05
  ViewResult = <g id="Ortho_0_003"\n   transform="rotate(90,177.96,60.2925) translate(177.96,60.2925) scale(0.8,0.8)"\n  >\n<g   fill="none"\n   stroke="rgb(0, 0, 0)"\n   stroke-linecap="butt"\n   stroke-linejoin="miter"\n   stroke-width="0.437500"\n   transform="scale(1,-1)"\n  >\n<path id= "1" d=" M -49.2 84.95 L -49.2 85 " />\n<path id= "2" d=" M -49.2 81 L -49.2 84.95 " />\n<path id= "3" d=" M -49.2 85 L -30.7 85 " />\n<path id= "4" d=" M -30.7 84.95 L -30.7 85 " />\n<path id= "5" d=" M -49.2 84.95 L -30.7 84.95 " />\n<path id= "6" d=" M -49.2 80.95 L -49.2 81 " />\n<path id= "7" d=" M -30.7 81 L -30.7 84.95 " />\n<path id= "8" d=" M -49.2 81 L -30.7 81 " />\n<path id= "9" d=" M -30.7 84.95 L -30.5 84.95 " />\n<path id= "10" d=" M 20.5 20.75 L -30.5 84.95 " />\n<path id= "11" d=" M 20.5 20.7 L 20.5 20.75 " />\n<path id= "12" d=" M -49.2 80.95 L 16.5 -4.9 " />\n<path id= "13" d=" M 16.5 20.7 L 20.5 20.7 " />\n<path id= "14" d=" M 16.5 -4.9 L 16.5 20.7 " />\n<path id= "15" d=" M 20.5 -4.9 L 20.5 20.7 " />\n<path id= "16" d=" M 20.5 20.6 L 42.5 20.6 " />\n<path id= "17" d=" M 20.5 -4.9 L 42.5 -4.9 " />\n<path id= "18" d=" M 42.5 -4.9 L 42.5 20.6 " />\n<circle cx ="32" cy ="0" r ="2.6" /><circle cx ="32" cy ="15.6" r ="2.6" /><path id= "21" d=" M 16.5 -4.9 L 20.5 -4.9 " />\n</g>\n</g>
  Visible = false
  X = 177.96
  Y = 60.2925
FEATURE [Drawing::FeatureViewPart] Ortho006  label="Ortho_1_0"
  Direction = (0,1,0)
  HiddenWidth = 0.15
  LineWidth = 0.35
  Rotation = -90
  Scale = 0.8
  ShowHiddenLines = false
  ShowSmoothLines = false
  Source = -> Cut001002002_solid
  Tolerance = 0.05
  ViewResult = <g id="Ortho_1_0"\n   transform="rotate(-90,318.557,148.54) translate(318.557,148.54) scale(0.8,0.8)"\n  >\n<g   fill="none"\n   stroke="rgb(0, 0, 0)"\n   stroke-linecap="butt"\n   stroke-linejoin="miter"\n   stroke-width="0.437500"\n   transform="scale(1,-1)"\n  >\n<path id= "1" d=" M 11 -49.2 L 64 -49.2 " />\n<path id= "2" d=" M 64 -49.2 L 64 -30.7 " />\n<path id= "3" d=" M 11 -49.2 L 11 -30.7 " />\n<path id= "4" d=" M 11 -30.7 L 64 -30.7 " />\n<circle cx ="22" cy ="-40.1" r ="3.25" /><path id= "6" d=" M 60 -30.7 L 60 -30.5 " />\n<path id= "7" d=" M 60 20.5 L 60 -30.5 " />\n<path id= "8" d=" M 60 -30.5 L 64 -30.5 " />\n<path id= "9" d=" M 64 -30.7 L 64 -30.5 " />\n<path id= "10" d=" M 60 20.5 L 64 20.5 " />\n<path id= "11" d=" M 64 20.5 L 64 -30.5 " />\n<path id= "12" d=" M 44.5 20.5 L 60 20.5 " />\n<path id= "13" d=" M 44.5 16.5 L 60 16.5 " />\n<path id= "14" d=" M 44.5 16.5 L 44.5 20.5 " />\n<path id= "15" d=" M 64 20.5 L 64.1 20.5 " />\n<path id= "16" d=" M 64.1 16.5 L 64.1 20.5 " />\n<path id= "17" d=" M 64 16.5 L 64.1 16.5 " />\n<path id= "18" d=" M 44.5 20.5 L 44.5 26.5 " />\n<path id= "19" d=" M 44.5 37.5 L 44.5 26.5 " />\n<path id= "20" d=" M 44.5 37.5 L 44.5 42.5 " />\n<path id= "21" d=" M 44.5 42.5 L 48.5 42.5 " />\n<path id= "22" d=" M 48.5 20.5 L 48.5 42.5 " />\n</g>\n</g>
  Visible = false
  X = 318.557
  Y = 148.54
FEATURE [Drawing::FeatureViewPart] Ortho007  label="Ortho_0_-1"
  Direction = (0,0,-1)
  HiddenWidth = 0.15
  LineWidth = 0.35
  Rotation = 90
  Scale = 0.8
  ShowHiddenLines = false
  ShowSmoothLines = false
  Source = -> Cut001002002_solid
  Tolerance = 0.05
  ViewResult = <g id="Ortho_0_-1"\n   transform="rotate(90,177.96,176.708) translate(177.96,176.708) scale(0.8,0.8)"\n  >\n<g   fill="none"\n   stroke="rgb(0, 0, 0)"\n   stroke-linecap="butt"\n   stroke-linejoin="miter"\n   stroke-width="0.437500"\n   transform="scale(1,-1)"\n  >\n<path id= "1" d=" M 49.2 81 L 49.2 85 " />\n<path id= "2" d=" M 49.2 81 L 30.7 81 " />\n<path id= "3" d=" M 49.2 85 L 30.7 85 " />\n<path id= "4" d=" M 30.7 81 L 30.7 85 " />\n<path id= "5" d=" M 49.2 80.95 L 49.2 81 " />\n<path id= "6" d=" M 30.7 84.95 L 30.5 84.95 " />\n<path id= "7" d=" M -20.5 20.75 L 30.5 84.95 " />\n<path id= "8" d=" M -20.5 20.7 L -20.5 20.75 " />\n<path id= "9" d=" M 49.2 80.95 L -16.5 -4.9 " />\n<path id= "10" d=" M -16.5 20.7 L -20.5 20.7 " />\n<path id= "11" d=" M -16.5 -4.9 L -16.5 20.7 " />\n<path id= "12" d=" M -20.5 20.6 L -20.5 20.7 " />\n<path id= "13" d=" M -20.5 -4.9 L -20.5 20.6 " />\n<path id= "14" d=" M -16.5 -4.9 L -20.5 -4.9 " />\n<path id= "15" d=" M -20.5 20.6 L -26.5 20.6 " />\n<path id= "16" d=" M -37.5 20.6 L -26.5 20.6 " />\n<path id= "17" d=" M -37.5 20.6 L -42.5 20.6 " />\n<path id= "18" d=" M -26.5 20.6 L -26.5 10.6 " />\n<path id= "19" d=" M -37.5 10.6 L -26.5 10.6 " />\n<path id= "20" d=" M -37.5 20.6 L -37.5 10.6 " />\n<path id= "21" d=" M -42.5 -4.9 L -42.5 20.6 " />\n<path id= "22" d=" M -37.5 -4.9 L -42.5 -4.9 " />\n<path id= "23" d=" M -37.5 5 L -37.5 -4.9 " />\n<path id= "24" d=" M -37.5 5 L -26.5 5 " />\n<path id= "25" d=" M -26.5 5 L -26.5 -4.9 " />\n<path id= "26" d=" M -20.5 -4.9 L -26.5 -4.9 " />\n<path id= "27" d=" M -26.5 -4.9 L -37.5 -4.9 " />\n<circle cx ="-32" cy ="15.6" r ="2.6" /><circle cx ="-32" cy ="0" r ="2.6" /></g>\n</g>
  Visible = false
  X = 177.96
  Y = 176.708
FEATURE [Drawing::FeaturePage] Page001
  EditableTexts = AUTHOR NAME | CREATION DATE | SUPERVISOR NAME | CHECK DATE | SCALE | WEIGHT | NUMBER | SHEET | TITLE | SUBTITLE
  Group = -> [Ortho007,Ortho003,Ortho004,Ortho005,Ortho006]
  Template = <path>
FEATURE [Part::Feature] Cut001002002  label="负003"
  shape: bbox 35 x 45.3 x 92 mm, 35 faces (baked)
FEATURE [Drawing::FeatureViewPart] Ortho008  label="Ortho_0_004"
  Direction = (1,0,0)
  HiddenWidth = 0.15
  LineWidth = 0.35
  Rotation = -90
  Scale = 1.5
  ShowHiddenLines = false
  ShowSmoothLines = false
  Source = -> Cut001002002
  Tolerance = 0.05
  ViewResult = <g id="Ortho_0_004"\n   transform="rotate(-90,82.9,192.917) translate(82.9,192.917) scale(1.5,1.5)"\n  >\n<g   fill="none"\n   stroke="rgb(0, 0, 0)"\n   stroke-linecap="butt"\n   stroke-linejoin="miter"\n   stroke-width="0.233333"\n   transform="scale(1,-1)"\n  >\n<path id= "1" d=" M -43.5 -67.5 L 44.5 -67.5 " />\n<path id= "2" d=" M -43.5 -71.5 L 44.5 -71.5 " />\n<path id= "3" d=" M -43.5 -67.5 L -43.5 -71.5 " />\n<path id= "4" d=" M 44.5 -56.5 L 44.5 -71.5 " />\n<path id= "5" d=" M 44.5 -54.55 L 44.5 -56.5 " />\n<path id= "6" d=" M 44.5 -71.5 L 48.5 -71.5 " />\n<path id= "7" d=" M 44.5 -56.5 L 48.5 -56.5 " />\n<path id= "8" d=" M 48.5 -56.5 L 48.5 -71.5 " />\n<path id= "9" d=" M 48.5 -54.55 L 48.5 -56.5 " />\n<path id= "10" d=" M 44.5 -54.55 L 48.5 -54.55 " />\n<path id= "11" d=" M 44.5 -54.5 L 44.5 -54.55 " />\n<path id= "12" d=" M 48.5 -54.5 L 48.5 -54.55 " />\n<path id= "13" d=" M 44.5 -54.5 L 48.5 -54.5 " />\n<path id= "14" d=" M 44.5 -27.2 L 44.5 -54.5 " />\n<path d="M44.5,-27.2 Q44.5,-27.0306 44.5,-26.8697  Q44.5,-26.7646 44.5,-26.668  Q44.5,-26.5743 44.5,-26.4929  Q44.5,-26.4555 44.5,-26.4182  Q44.5,-26.3857 44.5,-26.3533  Q44.5,-26.3262 44.5,-26.299  Q44.5,-26.2776 44.5,-26.2561  Q44.5,-26.2406 44.5,-26.2251  Q44.5,-26.2157 44.5,-26.2063  Q44.5,-26.2031 44.5,-26.2 " /><path id= "16" d=" M 48.5 -27.2 L 48.5 -54.5 " />\n<path id= "17" d=" M 44.5 -26.2 L 48.5 -26.2 " />\n<path d="M48.5,-27.2 Q48.5,-27.0306 48.5,-26.8697  Q48.5,-26.7646 48.5,-26.668  Q48.5,-26.5743 48.5,-26.4929  Q48.5,-26.4555 48.5,-26.4182  Q48.5,-26.3857 48.5,-26.3533  Q48.5,-26.3262 48.5,-26.299  Q48.5,-26.2776 48.5,-26.2561  Q48.5,-26.2406 48.5,-26.2251  Q48.5,-26.2157 48.5,-26.2063  Q48.5,-26.2031 48.5,-26.2 " /></g>\n</g>
  Visible = false
  X = 82.9
  Y = 192.917
FEATURE [Drawing::FeatureViewPart] Ortho009  label="Ortho_-1_002"
  Direction = (0,-1,0)
  HiddenWidth = 0.15
  LineWidth = 0.35
  Rotation = 90
  Scale = 1.5
  ShowHiddenLines = false
  ShowSmoothLines = false
  Source = -> Cut001002002
  Tolerance = 0.05
  ViewResult = <blob: 2983 chars omitted>
  Visible = false
  X = 28.6
  Y = 192.917
FEATURE [Drawing::FeatureViewPart] Ortho010  label="Ortho_0_005"
  Direction = (0,0,1)
  HiddenWidth = 0.15
  LineWidth = 0.35
  Rotation = 90
  Scale = 1.5
  ShowHiddenLines = false
  ShowSmoothLines = false
  Source = -> Cut001002002
  Tolerance = 0.05
  ViewResult = <g id="Ortho_0_005"\n   transform="rotate(90,82.9,27.5833) translate(82.9,27.5833) scale(1.5,1.5)"\n  >\n<g   fill="none"\n   stroke="rgb(0, 0, 0)"\n   stroke-linecap="butt"\n   stroke-linejoin="miter"\n   stroke-width="0.233333"\n   transform="scale(1,-1)"\n  >\n<path id= "1" d=" M 7.5 67.5 L 7.5 71.5 " />\n<path id= "2" d=" M 7.5 66.5 L 7.5 67.5 " />\n<path id= "3" d=" M 7.5 71.5 L 22.5 71.5 " />\n<path id= "4" d=" M 22.5 67.5 L 22.5 71.5 " />\n<path id= "5" d=" M 7.5 67.5 L 22.5 67.5 " />\n<path id= "6" d=" M 42.5 56.5 L 22.5 71.5 " />\n<path id= "7" d=" M 42.5 54.55 L 42.5 56.5 " />\n<path id= "8" d=" M 7.5 66.5 L 20.5 54.5 " />\n<path id= "9" d=" M 20.5 54.55 L 42.5 54.55 " />\n<path id= "10" d=" M 20.5 54.5 L 20.5 54.55 " />\n<path id= "11" d=" M 42.5 54.5 L 42.5 54.55 " />\n<path id= "12" d=" M 20.5 27.2 L 20.5 54.5 " />\n<path id= "13" d=" M 20.5 54.5 L 42.5 54.5 " />\n<path id= "14" d=" M 42.5 27.2 L 42.5 54.5 " />\n<path d="M42.5 27.2 A1 1 0 0 0 41.5 26.2" /><path id= "16" d=" M 21.5 26.2 L 41.5 26.2 " />\n<path d="M20.5 27.2 A1 1 0 0 1 21.5 26.2" /><circle cx ="32" cy ="31.2" r ="2.6" /><circle cx ="32" cy ="46.8" r ="2.6" /></g>\n</g>
  Visible = false
  X = 82.9
  Y = 27.5833
FEATURE [Drawing::FeatureViewPython] dim006  # drawing view (typed FeaturePython)
  Rotation = 0
  ViewResult = <g> \n  <line x1="192.150000" y1="258.167000" x2="206.681075" y2="258.167000" style="stroke:rgb(0,0,255);stroke-width:0.30" />\n<line x1="192.150000" y1="126.167000" x2="206.681075" y2="126.167000" style="stroke:rgb(0,0,255);stroke-width:0.30" />\n<line x1="205.681075" y1="258.167000" x2="205.681075" y2="126.167000" style="stroke:rgb(0,0,255);stroke-width:0.30" /> \n  <polygon points="205.681075,126.167000 204.681075,129.167000 205.681075,130.167000 206.681075,129.167000" style="fill:rgb(0,0,255);stroke:rgb(0,0,255);stroke-width:0" /><polygon points="205.681075,258.167000 206.681075,255.167000 205.681075,254.167000 204.681075,255.167000" style="fill:rgb(0,0,255);stroke:rgb(0,0,255);stroke-width:0" /> \n  <text x="203.681075" y="192.167000" font-family="Verdana" font-size="3.6" fill="rgb(255,0,0)" text-anchor="middle" transform="rotate(-90.000000 203.681075,192.167000)" >88</text> </g>
  Visible = false
  X = 0
  Y = 0
  arrowL1 = 3
  arrowL2 = 1
  arrowW = 2
  arrow_scheme = 0
  autoPlaceOffset = 2
  autoPlaceText = true
  click1_x = 205.681
  click1_y = 157.589
  click2_x = 205.681
  click2_y = 157.589
  comma_decimal_place = false
  dimension_line_overshoot = 1
  gap_datum_points = 2
  halfDimension_linear = false
  lineColor = rgb(0,0,255)
  strokeWidth = 0.3
  textFormat_linear = %(value)3.3f
  textRenderer_color = rgb(255,0,0)
  textRenderer_family = Verdana
  textRenderer_size = 3.6
  unit_custom_scale = 1
  unit_scheme = 0
FEATURE [Drawing::FeatureViewPython] dim007  # drawing view (typed FeaturePython)
  Rotation = 0
  ViewResult = <g> \n  <line x1="37.850000" y1="258.167000" x2="21.328634" y2="258.167000" style="stroke:rgb(0,0,255);stroke-width:0.30" />\n<line x1="37.850000" y1="126.167000" x2="21.328634" y2="126.167000" style="stroke:rgb(0,0,255);stroke-width:0.30" />\n<line x1="22.328634" y1="258.167000" x2="22.328634" y2="126.167000" style="stroke:rgb(0,0,255);stroke-width:0.30" /> \n  <polygon points="22.328634,126.167000 21.328634,129.167000 22.328634,130.167000 23.328634,129.167000" style="fill:rgb(0,0,255);stroke:rgb(0,0,255);stroke-width:0" /><polygon points="22.328634,258.167000 23.328634,255.167000 22.328634,254.167000 21.328634,255.167000" style="fill:rgb(0,0,255);stroke:rgb(0,0,255);stroke-width:0" /> \n  <text x="20.328634" y="192.167000" font-family="Verdana" font-size="3.6" fill="rgb(255,0,0)" text-anchor="middle" transform="rotate(-90.000000 20.328634,192.167000)" >88</text> </g>
  Visible = false
  X = 0
  Y = 0
  arrowL1 = 3
  arrowL2 = 1
  arrowW = 2
  arrow_scheme = 0
  autoPlaceOffset = 2
  autoPlaceText = true
  click1_x = 22.3286
  click1_y = 167.465
  click2_x = 22.3286
  click2_y = 167.465
  comma_decimal_place = false
  dimension_line_overshoot = 1
  gap_datum_points = 2
  halfDimension_linear = false
  lineColor = rgb(0,0,255)
  strokeWidth = 0.3
  textFormat_linear = %(value)3.3f
  textRenderer_color = rgb(255,0,0)
  textRenderer_family = Verdana
  textRenderer_size = 3.6
  unit_custom_scale = 1
  unit_scheme = 0
FEATURE [Drawing::FeatureViewPython] dia004  # drawing view (typed FeaturePython)
  Rotation = 0
  ViewResult = <g>  <circle cx ="50.500000" cy ="139.667000" r="0.500000" stroke="none" fill="rgb(0,0,255)" /> \n<line x1="65.268316" y1="145.136124" x2="45.928412" y2="137.974012" style="stroke:rgb(0,0,255);stroke-width:0.30" />\n<polygon points="55.071588,141.359988 52.605583,139.380388 51.320541,139.970870 51.911024,141.255911" style="fill:rgb(0,0,255);stroke:rgb(0,0,255);stroke-width:0" />\n<polygon points="45.928412,137.974012 48.394417,139.953612 49.679459,139.363130 49.088976,138.078089" style="fill:rgb(0,0,255);stroke:rgb(0,0,255);stroke-width:0" />\n<line x1="65.268316" y1="145.136124" x2="78.150220" y2="145.136124" style="stroke:rgb(0,0,255);stroke-width:0.30" />\n<text x="71.709268" y="143.136124" font-family="Verdana" font-size="3.6" fill="rgb(255,0,0)" text-anchor="middle" transform="rotate(0.000000 71.709268,143.136124)" >Ø6.5</text> </g>
  Visible = false
  X = 0
  Y = 0
  arrowL1 = 3
  arrowL2 = 1
  arrowW = 2
  arrow_scheme = 0
  autoPlaceOffset = 2
  autoPlaceText = true
  centerPointDia = 1
  click1_x = 65.2683
  click1_y = 145.136
  click2_x = 78.1502
  click2_y = 147.283
  click3_x = 78.1502
  click3_y = 147.283
  comma_decimal_place = false
  lineColor = rgb(0,0,255)
  strokeWidth = 0.3
  textFormat_circular = Ø%(value)3.3f
  textRenderer_color = rgb(255,0,0)
  textRenderer_family = Verdana
  textRenderer_size = 3.6
  unit_custom_scale = 1
  unit_scheme = 0
FEATURE [Drawing::FeatureViewPython] dia005  # drawing view (typed FeaturePython)
  Rotation = 0
  ViewResult = <g>  <circle cx ="50.500000" cy ="157.667000" r="0.500000" stroke="none" fill="rgb(0,0,255)" /> \n<line x1="64.838919" y1="162.741393" x2="47.318356" y2="156.541049" style="stroke:rgb(0,0,255);stroke-width:0.30" />\n<polygon points="53.681644,158.792951 56.176158,160.736505 57.452482,160.127410 56.843388,158.851086" style="fill:rgb(0,0,255);stroke:rgb(0,0,255);stroke-width:0" />\n<polygon points="47.318356,156.541049 44.823842,154.597495 43.547518,155.206590 44.156612,156.482914" style="fill:rgb(0,0,255);stroke:rgb(0,0,255);stroke-width:0" />\n<line x1="64.838919" y1="162.741393" x2="79.009014" y2="162.741393" style="stroke:rgb(0,0,255);stroke-width:0.30" />\n<text x="71.923967" y="160.741393" font-family="Verdana" font-size="3.6" fill="rgb(255,0,0)" text-anchor="middle" transform="rotate(0.000000 71.923967,160.741393)" >Ø4.5</text> </g>
  Visible = false
  X = 0
  Y = 0
  arrowL1 = 3
  arrowL2 = 1
  arrowW = 2
  arrow_scheme = 0
  autoPlaceOffset = 2
  autoPlaceText = true
  centerPointDia = 1
  click1_x = 64.8389
  click1_y = 162.741
  click2_x = 79.009
  click2_y = 164.459
  click3_x = 79.009
  click3_y = 164.459
  comma_decimal_place = false
  lineColor = rgb(0,0,255)
  strokeWidth = 0.3
  textFormat_circular = Ø%(value)3.3f
  textRenderer_color = rgb(255,0,0)
  textRenderer_family = Verdana
  textRenderer_size = 3.6
  unit_custom_scale = 1
  unit_scheme = 0
FEATURE [Drawing::FeatureViewPython] dia006  # drawing view (typed FeaturePython)
  Rotation = 0
  ViewResult = <g>  <circle cx ="129.700000" cy ="75.583300" r="0.500000" stroke="none" fill="rgb(0,0,255)" /> \n<line x1="133.971806" y1="81.585395" x2="127.438574" y2="72.405887" style="stroke:rgb(0,0,255);stroke-width:0.30" />\n<polygon points="131.961426,78.760713 132.886263,81.784729 134.280837,82.019598 134.515706,80.625024" style="fill:rgb(0,0,255);stroke:rgb(0,0,255);stroke-width:0" />\n<polygon points="127.438574,72.405887 126.513737,69.381871 125.119163,69.147002 124.884294,70.541576" style="fill:rgb(0,0,255);stroke:rgb(0,0,255);stroke-width:0" />\n<line x1="133.971806" y1="81.585395" x2="141.271552" y2="81.585395" style="stroke:rgb(0,0,255);stroke-width:0.30" />\n<text x="137.621679" y="79.585395" font-family="Verdana" font-size="3.6" fill="rgb(255,0,0)" text-anchor="middle" transform="rotate(0.000000 137.621679,79.585395)" >Ø5.2</text> </g>
  Visible = false
  X = 0
  Y = 0
  arrowL1 = 3
  arrowL2 = 1
  arrowW = 2
  arrow_scheme = 0
  autoPlaceOffset = 2
  autoPlaceText = true
  centerPointDia = 1
  click1_x = 133.972
  click1_y = 81.5854
  click2_x = 141.272
  click2_y = 82.4442
  click3_x = 141.272
  click3_y = 82.4442
  comma_decimal_place = false
  lineColor = rgb(0,0,255)
  strokeWidth = 0.3
  textFormat_circular = Ø%(value)3.3f
  textRenderer_color = rgb(255,0,0)
  textRenderer_family = Verdana
  textRenderer_size = 3.6
  unit_custom_scale = 1
  unit_scheme = 0
FEATURE [Drawing::FeatureViewPython] dia007  # drawing view (typed FeaturePython)
  Rotation = 0
  ViewResult = <g>  <circle cx ="153.100000" cy ="75.583300" r="0.500000" stroke="none" fill="rgb(0,0,255)" /> \n<line x1="158.447425" y1="81.155998" x2="150.399747" y2="72.769293" style="stroke:rgb(0,0,255);stroke-width:0.30" />\n<polygon points="155.800253,78.397307 157.155830,81.254301 158.569742,81.283468 158.598910,79.869556" style="fill:rgb(0,0,255);stroke:rgb(0,0,255);stroke-width:0" />\n<polygon points="150.399747,72.769293 149.044170,69.912299 147.630258,69.883132 147.601090,71.297044" style="fill:rgb(0,0,255);stroke:rgb(0,0,255);stroke-width:0" />\n<line x1="158.447425" y1="81.155998" x2="161.882599" y2="81.155998" style="stroke:rgb(0,0,255);stroke-width:0.30" />\n<text x="160.165012" y="79.155998" font-family="Verdana" font-size="3.6" fill="rgb(255,0,0)" text-anchor="middle" transform="rotate(0.000000 160.165012,79.155998)" >Ø5.2</text> </g>
  Visible = false
  X = 0
  Y = 0
  arrowL1 = 3
  arrowL2 = 1
  arrowW = 2
  arrow_scheme = 0
  autoPlaceOffset = 2
  autoPlaceText = true
  centerPointDia = 1
  click1_x = 158.447
  click1_y = 81.156
  click2_x = 161.883
  click2_y = 81.156
  click3_x = 161.883
  click3_y = 81.156
  comma_decimal_place = false
  lineColor = rgb(0,0,255)
  strokeWidth = 0.3
  textFormat_circular = Ø%(value)3.3f
  textRenderer_color = rgb(255,0,0)
  textRenderer_family = Verdana
  textRenderer_size = 3.6
  unit_custom_scale = 1
  unit_scheme = 0
FEATURE [Drawing::FeatureViewPython] dia008  # drawing view (typed FeaturePython)
  Rotation = 0
  ViewResult = <g>  <circle cx ="123.700000" cy ="59.833300" r="0.500000" stroke="none" fill="rgb(0,0,255)" /> \n<line x1="126.317543" y1="62.537538" x2="122.656757" y2="58.755504" style="stroke:rgb(0,0,255);stroke-width:0.30" />\n<polygon points="124.743243,60.911096 126.111199,63.762183 127.525224,63.785218 127.548260,62.371192" style="fill:rgb(0,0,255);stroke:rgb(0,0,255);stroke-width:0" />\n<polygon points="122.656757,58.755504 121.288801,55.904417 119.874776,55.881382 119.851740,57.295408" style="fill:rgb(0,0,255);stroke:rgb(0,0,255);stroke-width:0" />\n<line x1="126.317543" y1="62.537538" x2="132.529881" y2="62.537538" style="stroke:rgb(0,0,255);stroke-width:0.30" />\n<text x="129.423712" y="60.537538" font-family="Verdana" font-size="3.6" fill="rgb(255,0,0)" text-anchor="middle" transform="rotate(0.000000 129.423712,60.537538)" >Ø2</text> </g>
  Visible = false
  X = 0
  Y = 0
  arrowL1 = 3
  arrowL2 = 1
  arrowW = 2
  arrow_scheme = 0
  autoPlaceOffset = 2
  autoPlaceText = true
  centerPointDia = 1
  click1_x = 126.318
  click1_y = 62.5375
  click2_x = 132.53
  click2_y = 65.4366
  click3_x = 132.53
  click3_y = 65.4366
  comma_decimal_place = false
  lineColor = rgb(0,0,255)
  strokeWidth = 0.3
  textFormat_circular = Ø%(value)3.3f
  textRenderer_color = rgb(255,0,0)
  textRenderer_family = Verdana
  textRenderer_size = 3.6
  unit_custom_scale = 1
  unit_scheme = 0
FEATURE [Drawing::FeatureViewPython] dimStack003  # drawing view (typed FeaturePython)
  Rotation = 0
  ViewResult = <g> <line x1="52.500001" y1="139.667000" x2="87.558579" y2="139.667000" style="stroke:rgb(0,0,255);stroke-width:0.30" />\n<line x1="52.500001" y1="157.667000" x2="87.558579" y2="157.667000" style="stroke:rgb(0,0,255);stroke-width:0.30" />\n<line x1="86.558579" y1="139.667000" x2="86.558579" y2="157.667000" style="stroke:rgb(0,0,255);stroke-width:0.30" />\n<polygon points="86.558579,139.667000 85.558579,142.667000 86.558579,143.667000 87.558579,142.667000" style="fill:rgb(0,0,255);stroke:rgb(0,0,255);stroke-width:0" />\n<polygon points="86.558579,157.667000 87.558579,154.667000 86.558579,153.667000 85.558579,154.667000" style="fill:rgb(0,0,255);stroke:rgb(0,0,255);stroke-width:0" />\n<text x="84.558579" y="148.667000" font-family="Verdana" font-size="3.6" fill="rgb(255,0,0)" text-anchor="middle" transform="rotate(-90.000000 84.558579,148.667000)" >12</text> </g> 
  Visible = false
  X = 0
  Y = 0
  arrowL1 = 3
  arrowL2 = 1
  arrowW = 2
  arrow_scheme = 0
  autoPlaceOffset = 2
  click1_x = 86.5586
  click1_y = 158.415
  comma_decimal_place = false
  dimension_line_overshoot = 1
  gap_datum_points = 2
  lineColor = rgb(0,0,255)
  stack_offset = 7
  stack_offset0 = 0
  strokeWidth = 0.3
  textFormat_linear = %(value)3.3f
  textRenderer_color = rgb(255,0,0)
  textRenderer_family = Verdana
  textRenderer_size = 3.6
  unit_custom_scale = 1
  unit_scheme = 0
FEATURE [Drawing::FeatureViewPython] dimStack004  # drawing view (typed FeaturePython)
  Rotation = 0
  ViewResult = <g> <line x1="52.500001" y1="175.667000" x2="87.765657" y2="175.667000" style="stroke:rgb(0,0,255);stroke-width:0.30" />\n<line x1="52.500001" y1="193.667000" x2="87.765657" y2="193.667000" style="stroke:rgb(0,0,255);stroke-width:0.30" />\n<line x1="86.765657" y1="175.667000" x2="86.765657" y2="193.667000" style="stroke:rgb(0,0,255);stroke-width:0.30" />\n<polygon points="86.765657,175.667000 85.765657,178.667000 86.765657,179.667000 87.765657,178.667000" style="fill:rgb(0,0,255);stroke:rgb(0,0,255);stroke-width:0" />\n<polygon points="86.765657,193.667000 87.765657,190.667000 86.765657,189.667000 85.765657,190.667000" style="fill:rgb(0,0,255);stroke:rgb(0,0,255);stroke-width:0" />\n<text x="84.765657" y="184.667000" font-family="Verdana" font-size="3.6" fill="rgb(255,0,0)" text-anchor="middle" transform="rotate(-90.000000 84.765657,184.667000)" >12</text> </g> 
  Visible = false
  X = 0
  Y = 0
  arrowL1 = 3
  arrowL2 = 1
  arrowW = 2
  arrow_scheme = 0
  autoPlaceOffset = 2
  click1_x = 86.7657
  click1_y = 193.618
  comma_decimal_place = false
  dimension_line_overshoot = 1
  gap_datum_points = 2
  lineColor = rgb(0,0,255)
  stack_offset = 7
  stack_offset0 = 0
  strokeWidth = 0.3
  textFormat_linear = %(value)3.3f
  textRenderer_color = rgb(255,0,0)
  textRenderer_family = Verdana
  textRenderer_size = 3.6
  unit_custom_scale = 1
  unit_scheme = 0
FEATURE [Drawing::FeatureViewPython] dimStack005  # drawing view (typed FeaturePython)
  Rotation = 0
  ViewResult = <g> <line x1="52.500001" y1="157.667000" x2="87.558579" y2="157.667000" style="stroke:rgb(0,0,255);stroke-width:0.30" />\n<line x1="52.500001" y1="175.667000" x2="87.558579" y2="175.667000" style="stroke:rgb(0,0,255);stroke-width:0.30" />\n<line x1="86.558579" y1="157.667000" x2="86.558579" y2="175.667000" style="stroke:rgb(0,0,255);stroke-width:0.30" />\n<polygon points="86.558579,157.667000 85.558579,160.667000 86.558579,161.667000 87.558579,160.667000" style="fill:rgb(0,0,255);stroke:rgb(0,0,255);stroke-width:0" />\n<polygon points="86.558579,175.667000 87.558579,172.667000 86.558579,171.667000 85.558579,172.667000" style="fill:rgb(0,0,255);stroke:rgb(0,0,255);stroke-width:0" />\n<text x="84.558579" y="166.667000" font-family="Verdana" font-size="3.6" fill="rgb(255,0,0)" text-anchor="middle" transform="rotate(-90.000000 84.558579,166.667000)" >12</text> </g> 
  Visible = false
  X = 0
  Y = 0
  arrowL1 = 3
  arrowL2 = 1
  arrowW = 2
  arrow_scheme = 0
  autoPlaceOffset = 2
  click1_x = 86.5586
  click1_y = 173.738
  comma_decimal_place = false
  dimension_line_overshoot = 1
  gap_datum_points = 2
  lineColor = rgb(0,0,255)
  stack_offset = 7
  stack_offset0 = 0
  strokeWidth = 0.3
  textFormat_linear = %(value)3.3f
  textRenderer_color = rgb(255,0,0)
  textRenderer_family = Verdana
  textRenderer_size = 3.6
  unit_custom_scale = 1
  unit_scheme = 0
FEATURE [Drawing::FeatureViewPython] dimStack006  # drawing view (typed FeaturePython)
  Rotation = 0
  ViewResult = <g> <line x1="52.500001" y1="211.667000" x2="87.578227" y2="211.667000" style="stroke:rgb(0,0,255);stroke-width:0.30" />\n<line x1="52.500001" y1="193.667000" x2="87.578227" y2="193.667000" style="stroke:rgb(0,0,255);stroke-width:0.30" />\n<line x1="86.578227" y1="211.667000" x2="86.578227" y2="193.667000" style="stroke:rgb(0,0,255);stroke-width:0.30" />\n<polygon points="86.578227,211.667000 87.578227,208.667000 86.578227,207.667000 85.578227,208.667000" style="fill:rgb(0,0,255);stroke:rgb(0,0,255);stroke-width:0" />\n<polygon points="86.578227,193.667000 85.578227,196.667000 86.578227,197.667000 87.578227,196.667000" style="fill:rgb(0,0,255);stroke:rgb(0,0,255);stroke-width:0" />\n<text x="84.578227" y="202.667000" font-family="Verdana" font-size="3.6" fill="rgb(255,0,0)" text-anchor="middle" transform="rotate(-90.000000 84.578227,202.667000)" >12</text> </g> 
  Visible = false
  X = 0
  Y = 0
  arrowL1 = 3
  arrowL2 = 1
  arrowW = 2
  arrow_scheme = 0
  autoPlaceOffset = 2
  click1_x = 86.5782
  click1_y = 203.024
  comma_decimal_place = false
  dimension_line_overshoot = 1
  gap_datum_points = 2
  lineColor = rgb(0,0,255)
  stack_offset = 7
  stack_offset0 = 0
  strokeWidth = 0.3
  textFormat_linear = %(value)3.3f
  textRenderer_color = rgb(255,0,0)
  textRenderer_family = Verdana
  textRenderer_size = 3.6
  unit_custom_scale = 1
  unit_scheme = 0
FEATURE [Drawing::FeatureViewPython] dimStack007  # drawing view (typed FeaturePython)
  Rotation = 0
  ViewResult = <g> <line x1="52.500001" y1="211.667000" x2="87.956298" y2="211.667000" style="stroke:rgb(0,0,255);stroke-width:0.30" />\n<line x1="52.500001" y1="229.667000" x2="87.956298" y2="229.667000" style="stroke:rgb(0,0,255);stroke-width:0.30" />\n<line x1="86.956298" y1="211.667000" x2="86.956298" y2="229.667000" style="stroke:rgb(0,0,255);stroke-width:0.30" />\n<polygon points="86.956298,211.667000 85.956298,214.667000 86.956298,215.667000 87.956298,214.667000" style="fill:rgb(0,0,255);stroke:rgb(0,0,255);stroke-width:0" />\n<polygon points="86.956298,229.667000 87.956298,226.667000 86.956298,225.667000 85.956298,226.667000" style="fill:rgb(0,0,255);stroke:rgb(0,0,255);stroke-width:0" />\n<text x="84.956298" y="220.667000" font-family="Verdana" font-size="3.6" fill="rgb(255,0,0)" text-anchor="middle" transform="rotate(-90.000000 84.956298,220.667000)" >12</text> </g> 
  Visible = false
  X = 0
  Y = 0
  arrowL1 = 3
  arrowL2 = 1
  arrowW = 2
  arrow_scheme = 0
  autoPlaceOffset = 2
  click1_x = 86.9563
  click1_y = 231.19
  comma_decimal_place = false
  dimension_line_overshoot = 1
  gap_datum_points = 2
  lineColor = rgb(0,0,255)
  stack_offset = 7
  stack_offset0 = 0
  strokeWidth = 0.3
  textFormat_linear = %(value)3.3f
  textRenderer_color = rgb(255,0,0)
  textRenderer_family = Verdana
  textRenderer_size = 3.6
  unit_custom_scale = 1
  unit_scheme = 0
FEATURE [Drawing::FeatureViewPython] dimStack008  # drawing view (typed FeaturePython)
  Rotation = 0
  ViewResult = <g> <line x1="52.500001" y1="229.667000" x2="88.145334" y2="229.667000" style="stroke:rgb(0,0,255);stroke-width:0.30" />\n<line x1="52.500001" y1="247.667000" x2="88.145334" y2="247.667000" style="stroke:rgb(0,0,255);stroke-width:0.30" />\n<line x1="87.145334" y1="229.667000" x2="87.145334" y2="247.667000" style="stroke:rgb(0,0,255);stroke-width:0.30" />\n<polygon points="87.145334,229.667000 86.145334,232.667000 87.145334,233.667000 88.145334,232.667000" style="fill:rgb(0,0,255);stroke:rgb(0,0,255);stroke-width:0" />\n<polygon points="87.145334,247.667000 88.145334,244.667000 87.145334,243.667000 86.145334,244.667000" style="fill:rgb(0,0,255);stroke:rgb(0,0,255);stroke-width:0" />\n<text x="85.145334" y="238.667000" font-family="Verdana" font-size="3.6" fill="rgb(255,0,0)" text-anchor="middle" transform="rotate(-90.000000 85.145334,238.667000)" >12</text> </g> 
  Visible = false
  X = 0
  Y = 0
  arrowL1 = 3
  arrowL2 = 1
  arrowW = 2
  arrow_scheme = 0
  autoPlaceOffset = 2
  click1_x = 87.1453
  click1_y = 248.014
  comma_decimal_place = false
  dimension_line_overshoot = 1
  gap_datum_points = 2
  lineColor = rgb(0,0,255)
  stack_offset = 7
  stack_offset0 = 0
  strokeWidth = 0.3
  textFormat_linear = %(value)3.3f
  textRenderer_color = rgb(255,0,0)
  textRenderer_family = Verdana
  textRenderer_size = 3.6
  unit_custom_scale = 1
  unit_scheme = 0
FEATURE [Drawing::FeatureViewPython] dimStack009  # drawing view (typed FeaturePython)
  Rotation = 0
  ViewResult = <g> <line x1="52.500001" y1="247.667000" x2="88.334369" y2="247.667000" style="stroke:rgb(0,0,255);stroke-width:0.30" />\n<line x1="41.850001" y1="258.167000" x2="88.334369" y2="258.167000" style="stroke:rgb(0,0,255);stroke-width:0.30" />\n<line x1="87.334369" y1="247.667000" x2="87.334369" y2="258.167000" style="stroke:rgb(0,0,255);stroke-width:0.30" />\n<polygon points="87.334369,247.667000 86.334369,250.667000 87.334369,251.667000 88.334369,250.667000" style="fill:rgb(0,0,255);stroke:rgb(0,0,255);stroke-width:0" />\n<polygon points="87.334369,258.167000 88.334369,255.167000 87.334369,254.167000 86.334369,255.167000" style="fill:rgb(0,0,255);stroke:rgb(0,0,255);stroke-width:0" />\n<text x="85.334369" y="252.917000" font-family="Verdana" font-size="3.6" fill="rgb(255,0,0)" text-anchor="middle" transform="rotate(-90.000000 85.334369,252.917000)" >7</text> </g> 
  Visible = false
  X = 0
  Y = 0
  arrowL1 = 3
  arrowL2 = 1
  arrowW = 2
  arrow_scheme = 0
  autoPlaceOffset = 2
  click1_x = 87.3344
  click1_y = 258.979
  comma_decimal_place = false
  dimension_line_overshoot = 1
  gap_datum_points = 2
  lineColor = rgb(0,0,255)
  stack_offset = 7
  stack_offset0 = 0
  strokeWidth = 0.3
  textFormat_linear = %(value)3.3f
  textRenderer_color = rgb(255,0,0)
  textRenderer_family = Verdana
  textRenderer_size = 3.6
  unit_custom_scale = 1
  unit_scheme = 0
FEATURE [Drawing::FeatureViewPython] dimStack010  # drawing view (typed FeaturePython)
  Rotation = 0
  ViewResult = <g> <line x1="37.850000" y1="126.167000" x2="30.531110" y2="126.167000" style="stroke:rgb(0,0,255);stroke-width:0.30" />\n<line x1="48.499999" y1="139.667000" x2="30.531110" y2="139.667000" style="stroke:rgb(0,0,255);stroke-width:0.30" />\n<line x1="31.531110" y1="126.167000" x2="31.531110" y2="139.667000" style="stroke:rgb(0,0,255);stroke-width:0.30" />\n<polygon points="31.531110,126.167000 30.531110,129.167000 31.531110,130.167000 32.531110,129.167000" style="fill:rgb(0,0,255);stroke:rgb(0,0,255);stroke-width:0" />\n<polygon points="31.531110,139.667000 32.531110,136.667000 31.531110,135.667000 30.531110,136.667000" style="fill:rgb(0,0,255);stroke:rgb(0,0,255);stroke-width:0" />\n<text x="29.531110" y="132.917000" font-family="Verdana" font-size="3.6" fill="rgb(255,0,0)" text-anchor="middle" transform="rotate(-90.000000 29.531110,132.917000)" >9</text> </g> 
  Visible = false
  X = 0
  Y = 0
  arrowL1 = 3
  arrowL2 = 1
  arrowW = 2
  arrow_scheme = 0
  autoPlaceOffset = 2
  click1_x = 31.5311
  click1_y = 139.281
  comma_decimal_place = false
  dimension_line_overshoot = 1
  gap_datum_points = 2
  lineColor = rgb(0,0,255)
  stack_offset = 7
  stack_offset0 = 0
  strokeWidth = 0.3
  textFormat_linear = %(value)3.3f
  textRenderer_color = rgb(255,0,0)
  textRenderer_family = Verdana
  textRenderer_size = 3.6
  unit_custom_scale = 1
  unit_scheme = 0
FEATURE [Drawing::FeatureViewPython] dimStack011  # drawing view (typed FeaturePython)
  Rotation = 0
  ViewResult = <g> <line x1="122.200000" y1="57.833300" x2="122.200000" y2="38.977547" style="stroke:rgb(0,0,255);stroke-width:0.30" />\n<line x1="164.650000" y1="56.333300" x2="164.650000" y2="38.977547" style="stroke:rgb(0,0,255);stroke-width:0.30" />\n<line x1="122.200000" y1="39.977547" x2="164.650000" y2="39.977547" style="stroke:rgb(0,0,255);stroke-width:0.30" />\n<polygon points="122.200000,39.977547 125.200000,40.977547 126.200000,39.977547 125.200000,38.977547" style="fill:rgb(0,0,255);stroke:rgb(0,0,255);stroke-width:0" />\n<polygon points="164.650000,39.977547 161.650000,38.977547 160.650000,39.977547 161.650000,40.977547" style="fill:rgb(0,0,255);stroke:rgb(0,0,255);stroke-width:0" />\n<text x="143.425000" y="37.977547" font-family="Verdana" font-size="3.6" fill="rgb(255,0,0)" text-anchor="middle" transform="rotate(-0.000000 143.425000,37.977547)" >28.3</text> </g> 
  Visible = false
  X = 0
  Y = 0
  arrowL1 = 3
  arrowL2 = 1
  arrowW = 2
  arrow_scheme = 0
  autoPlaceOffset = 2
  click1_x = 160.054
  click1_y = 39.9775
  comma_decimal_place = false
  dimension_line_overshoot = 1
  gap_datum_points = 2
  lineColor = rgb(0,0,255)
  stack_offset = 7
  stack_offset0 = 0
  strokeWidth = 0.3
  textFormat_linear = %(value)3.3f
  textRenderer_color = rgb(255,0,0)
  textRenderer_family = Verdana
  textRenderer_size = 3.6
  unit_custom_scale = 1
  unit_scheme = 0
FEATURE [Drawing::FeatureViewPython] dimStack012  # drawing view (typed FeaturePython)
  Rotation = 0
  ViewResult = <g> <line x1="192.150000" y1="38.833300" x2="206.208486" y2="38.833300" style="stroke:rgb(0,0,255);stroke-width:0.30" />\n<line x1="192.150000" y1="61.333300" x2="206.208486" y2="61.333300" style="stroke:rgb(0,0,255);stroke-width:0.30" />\n<line x1="205.208486" y1="38.833300" x2="205.208486" y2="61.333300" style="stroke:rgb(0,0,255);stroke-width:0.30" />\n<polygon points="205.208486,38.833300 204.208486,41.833300 205.208486,42.833300 206.208486,41.833300" style="fill:rgb(0,0,255);stroke:rgb(0,0,255);stroke-width:0" />\n<polygon points="205.208486,61.333300 206.208486,58.333300 205.208486,57.333300 204.208486,58.333300" style="fill:rgb(0,0,255);stroke:rgb(0,0,255);stroke-width:0" />\n<text x="203.208486" y="50.083300" font-family="Verdana" font-size="3.6" fill="rgb(255,0,0)" text-anchor="middle" transform="rotate(-90.000000 203.208486,50.083300)" >15</text> </g> 
  Visible = false
  X = 0
  Y = 0
  arrowL1 = 3
  arrowL2 = 1
  arrowW = 2
  arrow_scheme = 0
  autoPlaceOffset = 2
  click1_x = 205.208
  click1_y = 60.1101
  comma_decimal_place = false
  dimension_line_overshoot = 1
  gap_datum_points = 2
  lineColor = rgb(0,0,255)
  stack_offset = 7
  stack_offset0 = 0
  strokeWidth = 0.3
  textFormat_linear = %(value)3.3f
  textRenderer_color = rgb(255,0,0)
  textRenderer_family = Verdana
  textRenderer_size = 3.6
  unit_custom_scale = 1
  unit_scheme = 0
FEATURE [Drawing::FeatureViewPython] dimStack013  # drawing view (typed FeaturePython)
  Rotation = 0
  ViewResult = <g> <line x1="39.850000" y1="260.167000" x2="39.850000" y2="274.955168" style="stroke:rgb(0,0,255);stroke-width:0.30" />\n<line x1="62.350000" y1="260.167000" x2="62.350000" y2="274.955168" style="stroke:rgb(0,0,255);stroke-width:0.30" />\n<line x1="39.850000" y1="273.955168" x2="62.350000" y2="273.955168" style="stroke:rgb(0,0,255);stroke-width:0.30" />\n<polygon points="39.850000,273.955168 42.850000,274.955168 43.850000,273.955168 42.850000,272.955168" style="fill:rgb(0,0,255);stroke:rgb(0,0,255);stroke-width:0" />\n<polygon points="62.350000,273.955168 59.350000,272.955168 58.350000,273.955168 59.350000,274.955168" style="fill:rgb(0,0,255);stroke:rgb(0,0,255);stroke-width:0" />\n<text x="51.100000" y="271.955168" font-family="Verdana" font-size="3.6" fill="rgb(255,0,0)" text-anchor="middle" transform="rotate(-0.000000 51.100000,271.955168)" >15</text> </g> 
  Visible = false
  X = 0
  Y = 0
  arrowL1 = 3
  arrowL2 = 1
  arrowW = 2
  arrow_scheme = 0
  autoPlaceOffset = 2
  click1_x = 55.8216
  click1_y = 273.955
  comma_decimal_place = false
  dimension_line_overshoot = 1
  gap_datum_points = 2
  lineColor = rgb(0,0,255)
  stack_offset = 7
  stack_offset0 = 0
  strokeWidth = 0.3
  textFormat_linear = %(value)3.3f
  textRenderer_color = rgb(255,0,0)
  textRenderer_family = Verdana
  textRenderer_size = 3.6
  unit_custom_scale = 1
  unit_scheme = 0
FEATURE [Drawing::FeatureViewPython] dimStack014  # drawing view (typed FeaturePython)
  Rotation = 0
  ViewResult = <g> <line x1="190.150000" y1="63.333300" x2="190.150000" y2="104.213345" style="stroke:rgb(0,0,255);stroke-width:0.30" />\n<line x1="164.650000" y1="93.333300" x2="164.650000" y2="104.213345" style="stroke:rgb(0,0,255);stroke-width:0.30" />\n<line x1="190.150000" y1="103.213345" x2="164.650000" y2="103.213345" style="stroke:rgb(0,0,255);stroke-width:0.30" />\n<polygon points="190.150000,103.213345 187.150000,102.213345 186.150000,103.213345 187.150000,104.213345" style="fill:rgb(0,0,255);stroke:rgb(0,0,255);stroke-width:0" />\n<polygon points="164.650000,103.213345 167.650000,104.213345 168.650000,103.213345 167.650000,102.213345" style="fill:rgb(0,0,255);stroke:rgb(0,0,255);stroke-width:0" />\n<text x="177.400000" y="101.213345" font-family="Verdana" font-size="3.6" fill="rgb(255,0,0)" text-anchor="middle" transform="rotate(0.000000 177.400000,101.213345)" >17</text> </g> 
  Visible = false
  X = 0
  Y = 0
  arrowL1 = 3
  arrowL2 = 1
  arrowW = 2
  arrow_scheme = 0
  autoPlaceOffset = 2
  click1_x = 177.504
  click1_y = 103.213
  comma_decimal_place = false
  dimension_line_overshoot = 1
  gap_datum_points = 2
  lineColor = rgb(0,0,255)
  stack_offset = 7
  stack_offset0 = 0
  strokeWidth = 0.3
  textFormat_linear = %(value)3.3f
  textRenderer_color = rgb(255,0,0)
  textRenderer_family = Verdana
  textRenderer_size = 3.6
  unit_custom_scale = 1
  unit_scheme = 0
FEATURE [Drawing::FeatureViewPython] dimStack015  # drawing view (typed FeaturePython)
  Rotation = 0
  ViewResult = <g> <line x1="166.650000" y1="91.333300" x2="225.385057" y2="91.333300" style="stroke:rgb(0,0,255);stroke-width:0.30" />\n<line x1="192.150000" y1="38.833300" x2="225.385057" y2="38.833300" style="stroke:rgb(0,0,255);stroke-width:0.30" />\n<line x1="224.385057" y1="91.333300" x2="224.385057" y2="38.833300" style="stroke:rgb(0,0,255);stroke-width:0.30" />\n<polygon points="224.385057,91.333300 225.385057,88.333300 224.385057,87.333300 223.385057,88.333300" style="fill:rgb(0,0,255);stroke:rgb(0,0,255);stroke-width:0" />\n<polygon points="224.385057,38.833300 223.385057,41.833300 224.385057,42.833300 225.385057,41.833300" style="fill:rgb(0,0,255);stroke:rgb(0,0,255);stroke-width:0" />\n<text x="222.385057" y="65.083300" font-family="Verdana" font-size="3.6" fill="rgb(255,0,0)" text-anchor="middle" transform="rotate(-90.000000 222.385057,65.083300)" >35</text> </g> 
  Visible = false
  X = 0
  Y = 0
  arrowL1 = 3
  arrowL2 = 1
  arrowW = 2
  arrow_scheme = 0
  autoPlaceOffset = 2
  click1_x = 224.385
  click1_y = 50.4725
  comma_decimal_place = false
  dimension_line_overshoot = 1
  gap_datum_points = 2
  lineColor = rgb(0,0,255)
  stack_offset = 7
  stack_offset0 = 0
  strokeWidth = 0.3
  textFormat_linear = %(value)3.3f
  textRenderer_color = rgb(255,0,0)
  textRenderer_family = Verdana
  textRenderer_size = 3.6
  unit_custom_scale = 1
  unit_scheme = 0
FEATURE [Drawing::FeatureViewPython] dimStack016  # drawing view (typed FeaturePython)
  Rotation = 0
  ViewResult = <g> <line x1="127.699999" y1="75.583300" x2="106.561160" y2="75.583300" style="stroke:rgb(0,0,255);stroke-width:0.30" />\n<line x1="121.699999" y1="91.333300" x2="106.561160" y2="91.333300" style="stroke:rgb(0,0,255);stroke-width:0.30" />\n<line x1="107.561160" y1="75.583300" x2="107.561160" y2="91.333300" style="stroke:rgb(0,0,255);stroke-width:0.30" />\n<polygon points="107.561160,75.583300 106.561160,78.583300 107.561160,79.583300 108.561160,78.583300" style="fill:rgb(0,0,255);stroke:rgb(0,0,255);stroke-width:0" />\n<polygon points="107.561160,91.333300 108.561160,88.333300 107.561160,87.333300 106.561160,88.333300" style="fill:rgb(0,0,255);stroke:rgb(0,0,255);stroke-width:0" />\n<text x="105.561160" y="83.458300" font-family="Verdana" font-size="3.6" fill="rgb(255,0,0)" text-anchor="middle" transform="rotate(-90.000000 105.561160,83.458300)" >10.5</text> </g> 
  Visible = false
  X = 0
  Y = 0
  arrowL1 = 3
  arrowL2 = 1
  arrowW = 2
  arrow_scheme = 0
  autoPlaceOffset = 2
  click1_x = 107.561
  click1_y = 90.1699
  comma_decimal_place = false
  dimension_line_overshoot = 1
  gap_datum_points = 2
  lineColor = rgb(0,0,255)
  stack_offset = 7
  stack_offset0 = 0
  strokeWidth = 0.3
  textFormat_linear = %(value)3.3f
  textRenderer_color = rgb(255,0,0)
  textRenderer_family = Verdana
  textRenderer_size = 3.6
  unit_custom_scale = 1
  unit_scheme = 0
FEATURE [Drawing::FeatureViewPython] dimStack017  # drawing view (typed FeaturePython)
  Rotation = 0
  ViewResult = <g> <line x1="127.699999" y1="75.583300" x2="106.561160" y2="75.583300" style="stroke:rgb(0,0,255);stroke-width:0.30" />\n<line x1="121.699999" y1="58.333300" x2="106.561160" y2="58.333300" style="stroke:rgb(0,0,255);stroke-width:0.30" />\n<line x1="107.561160" y1="75.583300" x2="107.561160" y2="58.333300" style="stroke:rgb(0,0,255);stroke-width:0.30" />\n<polygon points="107.561160,75.583300 108.561160,72.583300 107.561160,71.583300 106.561160,72.583300" style="fill:rgb(0,0,255);stroke:rgb(0,0,255);stroke-width:0" />\n<polygon points="107.561160,58.333300 106.561160,61.333300 107.561160,62.333300 108.561160,61.333300" style="fill:rgb(0,0,255);stroke:rgb(0,0,255);stroke-width:0" />\n<text x="105.561160" y="66.958300" font-family="Verdana" font-size="3.6" fill="rgb(255,0,0)" text-anchor="middle" transform="rotate(-90.000000 105.561160,66.958300)" >11.5</text> </g> 
  Visible = false
  X = 0
  Y = 0
  arrowL1 = 3
  arrowL2 = 1
  arrowW = 2
  arrow_scheme = 0
  autoPlaceOffset = 2
  click1_x = 107.561
  click1_y = 59.5462
  comma_decimal_place = false
  dimension_line_overshoot = 1
  gap_datum_points = 2
  lineColor = rgb(0,0,255)
  stack_offset = 7
  stack_offset0 = 0
  strokeWidth = 0.3
  textFormat_linear = %(value)3.3f
  textRenderer_color = rgb(255,0,0)
  textRenderer_family = Verdana
  textRenderer_size = 3.6
  unit_custom_scale = 1
  unit_scheme = 0
FEATURE [Drawing::FeatureViewPython] centerLines002  # drawing view (typed FeaturePython)
  Rotation = 0
  ViewResult = <g transform="scale(1.500000,1.500000)" stroke="rgb(0,0,255)"  stroke-width="0.200000" > <path d="M 33.666667,93.111333 L 33.666667,91.778000 M 33.666667,90.444667 L 33.666667,86.444667 M 33.666667,85.111333 L 33.666667,83.778000 M 33.666667,82.444667 L 33.666667,78.444667 M 33.666667,77.111333 L 33.666667,75.778000 M 33.666667,74.444667 L 33.666667,70.444667 M 33.666667,69.111333 L 33.666667,67.778000 M 33.666667,66.444667 L 33.666667,62.444667 M 33.666667,61.111333 L 33.666667,59.778000 M 33.666667,58.444667 L 33.666667,54.444667 M 33.666667,53.111333 L 33.666667,51.813882 "/>\n<path d="M 33.666667,93.111333 L 33.666667,94.444667 M 33.666667,95.778000 L 33.666667,99.778000 M 33.666667,101.111333 L 33.666667,102.444667 M 33.666667,103.778000 L 33.666667,107.778000 M 33.666667,109.111333 L 33.666667,110.444667 M 33.666667,111.778000 L 33.666667,115.778000 M 33.666667,117.111333 L 33.666667,118.444667 M 33.666667,119.778000 L 33.666667,123.778000 M 33.666667,125.111333 L 33.666667,126.444667 M 33.666667,127.778000 L 33.666667,131.778000 M 33.666667,133.111333 L 33.666667,134.444667 M 33.666667,135.778000 L 33.666667,139.778000 M 33.666667,141.111333 L 33.666667,142.444667 M 33.666667,143.778000 L 33.666667,147.778000 M 33.666667,149.111333 L 33.666667,150.444667 M 33.666667,151.778000 L 33.666667,155.778000 M 33.666667,157.111333 L 33.666667,158.444667 M 33.666667,159.778000 L 33.666667,163.778000 M 33.666667,165.111333 L 33.666667,166.444667 M 33.666667,167.778000 L 33.666667,171.778000 M 33.666667,173.111333 L 33.666667,174.444667 M 33.666667,175.778000 L 33.666667,179.778000 M 33.666667,181.111333 L 33.666667,182.444667 M 33.666667,183.778000 L 33.666667,187.778000 M 33.666667,189.111333 L 33.666667,189.220863 "/> </g> 
  Visible = false
  X = 0
  Y = 0
  centerLine_color = rgb(0,0,255)
  centerLine_len_dash = 6
  centerLine_len_dot = 2
  centerLine_len_gap = 2
  centerLine_width = 0.3
  click1_x = 51.5276
  click1_y = 77.7208
  click2_x = 60.1156
  click2_y = 283.831
FEATURE [Drawing::FeaturePage] Page002
  EditableTexts = AUTHOR NAME | CREATION DATE | SUPERVISOR NAME | CHECK DATE | SCALE | WEIGHT | NUMBER | SHEET | TITLE | SUBTITLE
  Group = -> [Ortho008,Ortho009,Ortho010,dim006,dim007,dia004,dia005,dia006,dia007,dia008,dimStack003,dimStack004,dimStack005,dimStack006,dimStack007,dimStack008,dimStack009,dimStack010,dimStack011,dimStack012,dimStack013,dimStack014,dimStack015,dimStack016,dimStack017,centerLines002]
  Template = <path>
FEATURE [Part::Fillet] Fillet010
  Base = -> Box025
  Edges = 2 edges r=2: [Edge5,Edge7]
FEATURE [Part::MultiFuse] Fusion002008006003002  label="正006"
  Shapes = -> [Box028,Chamfer001,Box027,Fillet010]
FEATURE [App::DocumentObjectGroup] ___002  label="正004"
  Group = -> [Fusion002008006003002,Box025]
FEATURE [Part::FeaturePython] Bend  # WARN: FeaturePython — macro-defined, semantics opaque (R4)
  AutoMiter = true
  BendType = 0
  LengthList = [10]
  ReliefFactor = 0.7
  UseReliefFactor = false
  angle = -90
  baseObject = -> Chamfer001 [Face8]
  bendAList = [-90]
  extend1 = 0
  extend2 = 0
  gap1 = 0
  gap2 = 0
  invert = false
  kfactor = 0.5
  length = 10
  miterangle1 = 0
  miterangle2 = 0
  offset = 0
  radius = 1
  reliefType = 0
  reliefd = 1
  reliefw = 0.8
  sketchflip = false
  sketchinvert = false
  unfold = false
FEATURE [Part::FeaturePython] Bend001  # WARN: FeaturePython — macro-defined, semantics opaque (R4)
  AutoMiter = true
  BendType = 0
  LengthList = [20.5]
  ReliefFactor = 0.7
  UseReliefFactor = false
  angle = 90
  baseObject = -> Bend [Face3]
  bendAList = [90]
  extend1 = 0
  extend2 = 0
  gap1 = 0
  gap2 = 0
  invert = false
  kfactor = 0.5
  length = 20.5
  miterangle1 = 0
  miterangle2 = 0
  offset = 0
  radius = 1
  reliefType = 0
  reliefd = 1
  reliefw = 0.8
  sketchflip = false
  sketchinvert = false
  unfold = false
FEATURE [Part::FeaturePython] Bend002  label="Bend002_material_0.40din"  # WARN: FeaturePython — macro-defined, semantics opaque (R4)
  AutoMiter = true
  BendType = 0
  LengthList = [47]
  ReliefFactor = 0.7
  UseReliefFactor = false
  angle = -90
  baseObject = -> Bend001 [Face24]
  bendAList = [-90]
  extend1 = 1
  extend2 = 0
  gap1 = 0
  gap2 = 0
  invert = false
  kfactor = 0.5
  length = 47
  miterangle1 = 0
  miterangle2 = 0
  offset = 0
  radius = 1
  reliefType = 0
  reliefd = 1
  reliefw = 0.8
  sketchflip = false
  sketchinvert = false
  unfold = false
FEATURE [Sketcher::SketchObject] Sketch  label="Unfold_Sketch"
  sketch-geometry (13):
    g0: LineSegment StartX=-50.2 StartY=85.4074 StartZ=0 EndX=-51.2 EndY=85.4074 EndZ=0
    g1: LineSegment StartX=-51.2 StartY=85.4074 StartZ=0 EndX=-51.2 EndY=132.407 EndZ=0
    g2: LineSegment StartX=-51.2 StartY=132.407 StartZ=0 EndX=-31.2 EndY=132.407 EndZ=0
    g3: LineSegment StartX=15.8 StartY=20.38 StartZ=0 EndX=-31.2 EndY=82.58 EndZ=0
    g4: LineSegment StartX=51.9549 StartY=-4.9 StartZ=0 EndX=51.9549 EndY=20.38 EndZ=0
    g5: LineSegment StartX=-50.2 StartY=80.95 StartZ=0 EndX=14.5 EndY=-4.9 EndZ=0
    g6: LineSegment StartX=-50.2 StartY=80.95 StartZ=0 EndX=-50.2 EndY=85.4074 EndZ=0
    g7: LineSegment StartX=14.5 StartY=-4.9 StartZ=0 EndX=51.9549 EndY=-4.9 EndZ=0
    g8: LineSegment StartX=51.9549 StartY=20.38 StartZ=0 EndX=15.8 EndY=20.38 EndZ=0
    g9: LineSegment StartX=-31.2 StartY=132.407 StartZ=0 EndX=-31.2 EndY=82.58 EndZ=0
    g10: LineSegment StartX=-50.2 StartY=83.9937 StartZ=0 EndX=-31.2 EndY=83.9937 EndZ=0
    g11: LineSegment StartX=30.0412 StartY=-4.9 StartZ=0 EndX=30.0412 EndY=20.38 EndZ=0
    g12: LineSegment StartX=17.2137 StartY=-4.9 StartZ=0 EndX=17.2137 EndY=20.38 EndZ=0
FEATURE [Drawing::FeatureViewPart] Ortho011  label="Ortho_0_006"
  Direction = (1,0,0)
  HiddenWidth = 0.15
  LineWidth = 0.35
  Rotation = -90
  Scale = 1.5
  ShowHiddenLines = false
  ShowSmoothLines = false
  Source = -> Sketch
  Tolerance = 0.05
  ViewResult = <g id="Ortho_0_006"\n   transform="rotate(-90,114.369,206.244) translate(114.369,206.244) scale(1.5,1.5)"\n  >\n<g   fill="none"\n   stroke="rgb(0, 0, 0)"\n   stroke-linecap="butt"\n   stroke-linejoin="miter"\n   stroke-width="0.233333"\n   transform="scale(1,-1)"\n  >\n<path id= "1" d=" M 0 -80.95 L 0 -85.4074 " />\n<path id= "2" d=" M 0 -85.4074 L 0 -132.407 " />\n<path id= "3" d=" M 0 -132.407 L 0 -82.58 " />\n<path id= "4" d=" M 0 -20.38 L 0 -82.58 " />\n<path id= "5" d=" M 0 4.9 L 0 -20.38 " />\n<path id= "6" d=" M 0 -80.95 L 0 4.9 " />\n<path id= "7" d=" M 0 4.9 L 0 -20.38 " />\n<path id= "8" d=" M 0 4.9 L 0 -20.38 " />\n</g>\n</g>
  Visible = false
  X = 114.369
  Y = 206.244
FEATURE [Drawing::FeatureViewPart] Ortho013  label="Ortho_0_007"
  Direction = (0,0,1)
  HiddenWidth = 0.15
  LineWidth = 0.35
  Rotation = 90
  Scale = 1.5
  ShowHiddenLines = false
  ShowSmoothLines = false
  Source = -> Sketch
  Tolerance = 0.05
  ViewResult = <g id="Ortho_0_007"\n   transform="rotate(90,114.369,107.556) translate(114.369,107.556) scale(1.5,1.5)"\n  >\n<g   fill="none"\n   stroke="rgb(0, 0, 0)"\n   stroke-linecap="butt"\n   stroke-linejoin="miter"\n   stroke-width="0.233333"\n   transform="scale(1,-1)"\n  >\n<path id= "1" d=" M -50.2 80.95 L -50.2 85.4074 " />\n<path id= "2" d=" M -50.2 85.4074 L -51.2 85.4074 " />\n<path id= "3" d=" M -51.2 85.4074 L -51.2 132.407 " />\n<path id= "4" d=" M -51.2 132.407 L -31.2 132.407 " />\n<path id= "5" d=" M -31.2 132.407 L -31.2 82.58 " />\n<path id= "6" d=" M 15.8 20.38 L -31.2 82.58 " />\n<path id= "7" d=" M 51.9549 20.38 L 15.8 20.38 " />\n<path id= "8" d=" M 51.9549 -4.9 L 51.9549 20.38 " />\n<path id= "9" d=" M 14.5 -4.9 L 51.9549 -4.9 " />\n<path id= "10" d=" M -50.2 80.95 L 14.5 -4.9 " />\n<path id= "11" d=" M -50.2 83.9937 L -31.2 83.9937 " />\n<path id= "12" d=" M 30.0412 -4.9 L 30.0412 20.38 " />\n<path id= "13" d=" M 17.2137 -4.9 L 17.2137 20.38 " />\n</g>\n</g>
  Visible = false
  X = 114.369
  Y = 107.556
FEATURE [Drawing::FeaturePage] Page003
  EditableTexts = AUTHOR NAME | CREATION DATE | SUPERVISOR NAME | CHECK DATE | SCALE | WEIGHT | NUMBER | SHEET | TITLE | SUBTITLE
  Group = -> [Ortho011,Ortho013]
  Template = <path>
FEATURE [Part::Cut] Cut001002003  label="zhengji"
  Base = -> Bend002
  Tool = -> Fusion002008006003002002001
FEATURE [Drawing::FeatureViewPart] Ortho014  label="Ortho_0_008"
  Direction = (1,0,0)
  HiddenWidth = 0.15
  LineWidth = 0.35
  Rotation = -90
  ShowHiddenLines = false
  ShowSmoothLines = false
  Source = -> Cut001002003
  Tolerance = 0.05
  ViewResult = <blob: 2479 chars omitted>
  Visible = false
  X = 168.66
  Y = 215.167
FEATURE [Drawing::FeatureViewPart] Ortho015  label="Ortho_1_1"
  Direction = (0.57735,0.57735,0.57735)
  HiddenWidth = 0.15
  LineWidth = 0.35
  Rotation = 120
  ShowHiddenLines = false
  ShowSmoothLines = false
  Source = -> Cut001002003
  Tolerance = 0.05
  ViewResult = <blob: 4084 chars omitted>
  Visible = false
  X = 300.742
  Y = 96.5499
FEATURE [Drawing::FeatureViewPart] Ortho016  label="Ortho_-1_003"
  Direction = (0,-1,0)
  HiddenWidth = 0.15
  LineWidth = 0.35
  Rotation = 90
  ShowHiddenLines = false
  ShowSmoothLines = false
  Source = -> Cut001002003
  Tolerance = 0.05
  ViewResult = <blob: 2621 chars omitted>
  Visible = false
  X = 91.33
  Y = 215.167
FEATURE [Drawing::FeatureViewPart] Ortho017  label="Ortho_0_009"
  Direction = (0,0,1)
  HiddenWidth = 0.15
  LineWidth = 0.35
  Rotation = 90
  ShowHiddenLines = false
  ShowSmoothLines = false
  Source = -> Cut001002003
  Tolerance = 0.05
  ViewResult = <blob: 2943 chars omitted>
  Visible = false
  X = 168.66
  Y = 85.0333
FEATURE [Drawing::FeatureViewPython] dim008  # drawing view (typed FeaturePython)
  Rotation = 0
  ViewResult = <g> \n  <line x1="38.130000" y1="156.167000" x2="24.334412" y2="156.167000" style="stroke:rgb(0,0,255);stroke-width:0.30" />\n<line x1="38.130000" y1="203.167000" x2="24.334412" y2="203.167000" style="stroke:rgb(0,0,255);stroke-width:0.30" />\n<line x1="25.334412" y1="156.167000" x2="25.334412" y2="203.167000" style="stroke:rgb(0,0,255);stroke-width:0.30" /> \n  <polygon points="25.334412,203.167000 26.334412,200.167000 25.334412,199.167000 24.334412,200.167000" style="fill:rgb(0,0,255);stroke:rgb(0,0,255);stroke-width:0" /><polygon points="25.334412,156.167000 24.334412,159.167000 25.334412,160.167000 26.334412,159.167000" style="fill:rgb(0,0,255);stroke:rgb(0,0,255);stroke-width:0" /> \n  <text x="23.334412" y="179.667000" font-family="Verdana" font-size="3.6" fill="rgb(255,0,0)" text-anchor="middle" transform="rotate(-90.000000 23.334412,179.667000)" >47</text> </g>
  Visible = false
  X = 0
  Y = 0
  arrowL1 = 3
  arrowL2 = 1
  arrowW = 2
  arrow_scheme = 0
  autoPlaceOffset = 2
  autoPlaceText = true
  click1_x = 25.3344
  click1_y = 172.188
  click2_x = 25.3344
  click2_y = 172.188
  comma_decimal_place = false
  dimension_line_overshoot = 1
  gap_datum_points = 2
  halfDimension_linear = false
  lineColor = rgb(0,0,255)
  strokeWidth = 0.3
  textFormat_linear = %(value)3.3f
  textRenderer_color = rgb(255,0,0)
  textRenderer_family = Verdana
  textRenderer_size = 3.6
  unit_custom_scale = 1
  unit_scheme = 0
FEATURE [Drawing::FeatureViewPython] dim009  # drawing view (typed FeaturePython)
  Rotation = 0
  ViewResult = <g> \n  <line x1="40.130000" y1="205.167000" x2="40.130000" y2="217.571088" style="stroke:rgb(0,0,255);stroke-width:0.30" />\n<line x1="60.130000" y1="205.167000" x2="60.130000" y2="217.571088" style="stroke:rgb(0,0,255);stroke-width:0.30" />\n<line x1="40.130000" y1="216.571088" x2="60.130000" y2="216.571088" style="stroke:rgb(0,0,255);stroke-width:0.30" /> \n  <polygon points="60.130000,216.571088 57.130000,215.571088 56.130000,216.571088 57.130000,217.571088" style="fill:rgb(0,0,255);stroke:rgb(0,0,255);stroke-width:0" /><polygon points="40.130000,216.571088 43.130000,217.571088 44.130000,216.571088 43.130000,215.571088" style="fill:rgb(0,0,255);stroke:rgb(0,0,255);stroke-width:0" /> \n  <text x="50.130000" y="214.571088" font-family="Verdana" font-size="3.6" fill="rgb(255,0,0)" text-anchor="middle" transform="rotate(0.000000 50.130000,214.571088)" >20</text> </g>
  Visible = false
  X = 0
  Y = 0
  arrowL1 = 3
  arrowL2 = 1
  arrowW = 2
  arrow_scheme = 0
  autoPlaceOffset = 2
  autoPlaceText = true
  click1_x = 51.2846
  click1_y = 216.571
  click2_x = 51.2846
  click2_y = 216.571
  comma_decimal_place = false
  dimension_line_overshoot = 1
  gap_datum_points = 2
  halfDimension_linear = false
  lineColor = rgb(0,0,255)
  strokeWidth = 0.3
  textFormat_linear = %(value)3.3f
  textRenderer_color = rgb(255,0,0)
  textRenderer_family = Verdana
  textRenderer_size = 3.6
  unit_custom_scale = 1
  unit_scheme = 0
FEATURE [Drawing::FeatureViewPython] dim010  # drawing view (typed FeaturePython)
  Rotation = 0
  ViewResult = <g> \n  <line x1="62.130000" y1="203.167000" x2="71.230443" y2="203.167000" style="stroke:rgb(0,0,255);stroke-width:0.30" />\n<line x1="62.130000" y1="156.167000" x2="71.230443" y2="156.167000" style="stroke:rgb(0,0,255);stroke-width:0.30" />\n<line x1="70.230443" y1="203.167000" x2="70.230443" y2="156.167000" style="stroke:rgb(0,0,255);stroke-width:0.30" /> \n  <polygon points="70.230443,156.167000 69.230443,159.167000 70.230443,160.167000 71.230443,159.167000" style="fill:rgb(0,0,255);stroke:rgb(0,0,255);stroke-width:0" /><polygon points="70.230443,203.167000 71.230443,200.167000 70.230443,199.167000 69.230443,200.167000" style="fill:rgb(0,0,255);stroke:rgb(0,0,255);stroke-width:0" /> \n  <text x="68.230443" y="179.667000" font-family="Verdana" font-size="3.6" fill="rgb(255,0,0)" text-anchor="middle" transform="rotate(-90.000000 68.230443,179.667000)" >47</text> </g>
  Visible = false
  X = 0
  Y = 0
  arrowL1 = 3
  arrowL2 = 1
  arrowW = 2
  arrow_scheme = 0
  autoPlaceOffset = 2
  autoPlaceText = true
  click1_x = 70.2304
  click1_y = 183.906
  click2_x = 70.2304
  click2_y = 183.906
  comma_decimal_place = false
  dimension_line_overshoot = 1
  gap_datum_points = 2
  halfDimension_linear = false
  lineColor = rgb(0,0,255)
  strokeWidth = 0.3
  textFormat_linear = %(value)3.3f
  textRenderer_color = rgb(255,0,0)
  textRenderer_family = Verdana
  textRenderer_size = 3.6
  unit_custom_scale = 1
  unit_scheme = 0
FEATURE [Drawing::FeatureViewPython] dia009  # drawing view (typed FeaturePython)
  Rotation = 0
  ViewResult = <g>  <circle cx ="51.230000" cy ="193.167000" r="0.500000" stroke="none" fill="rgb(0,0,255)" /> \n<line x1="55.450393" y1="198.644732" x2="49.246447" y2="190.592507" style="stroke:rgb(0,0,255);stroke-width:0.30" />\n<polygon points="53.213553,195.741493 54.252374,198.728273 55.654850,198.910101 55.836677,197.507625" style="fill:rgb(0,0,255);stroke:rgb(0,0,255);stroke-width:0" />\n<polygon points="49.246447,190.592507 48.207626,187.605727 46.805150,187.423899 46.623323,188.826375" style="fill:rgb(0,0,255);stroke:rgb(0,0,255);stroke-width:0" />\n<line x1="55.450393" y1="198.644732" x2="98.455954" y2="198.644732" style="stroke:rgb(0,0,255);stroke-width:0.30" />\n<text x="76.953173" y="196.644732" font-family="Verdana" font-size="3.6" fill="rgb(255,0,0)" text-anchor="middle" transform="rotate(0.000000 76.953173,196.644732)" >Ø6.5</text> </g>
  Visible = false
  X = 0
  Y = 0
  arrowL1 = 3
  arrowL2 = 1
  arrowW = 2
  arrow_scheme = 0
  autoPlaceOffset = 2
  autoPlaceText = true
  centerPointDia = 1
  click1_x = 55.4504
  click1_y = 198.645
  click2_x = 98.456
  click2_y = 197.7
  click3_x = 98.456
  click3_y = 197.7
  comma_decimal_place = false
  lineColor = rgb(0,0,255)
  strokeWidth = 0.3
  textFormat_circular = Ø%(value)3.3f
  textRenderer_color = rgb(255,0,0)
  textRenderer_family = Verdana
  textRenderer_size = 3.6
  unit_custom_scale = 1
  unit_scheme = 0
FEATURE [Drawing::FeatureViewPython] dim011  # drawing view (typed FeaturePython)
  Rotation = 0
  ViewResult = <g> \n  <line x1="51.230000" y1="191.167000" x2="51.230000" y2="180.814431" style="stroke:rgb(0,0,255);stroke-width:0.30" />\n<line x1="60.130000" y1="201.167000" x2="60.130000" y2="180.814431" style="stroke:rgb(0,0,255);stroke-width:0.30" />\n<line x1="51.230000" y1="181.814431" x2="60.130000" y2="181.814431" style="stroke:rgb(0,0,255);stroke-width:0.30" /> \n  <polygon points="60.130000,181.814431 63.130000,182.814431 64.130000,181.814431 63.130000,180.814431" style="fill:rgb(0,0,255);stroke:rgb(0,0,255);stroke-width:0" /><polygon points="51.230000,181.814431 48.230000,180.814431 47.230000,181.814431 48.230000,182.814431" style="fill:rgb(0,0,255);stroke:rgb(0,0,255);stroke-width:0" /> \n  <text x="55.680000" y="179.814431" font-family="Verdana" font-size="3.6" fill="rgb(255,0,0)" text-anchor="middle" transform="rotate(0.000000 55.680000,179.814431)" >8.9</text> </g>
  Visible = false
  X = 0
  Y = 0
  arrowL1 = 3
  arrowL2 = 1
  arrowW = 2
  arrow_scheme = 0
  autoPlaceOffset = 2
  autoPlaceText = true
  click1_x = 59.0172
  click1_y = 181.814
  click2_x = 59.0172
  click2_y = 181.814
  comma_decimal_place = false
  dimension_line_overshoot = 1
  gap_datum_points = 2
  halfDimension_linear = false
  lineColor = rgb(0,0,255)
  strokeWidth = 0.3
  textFormat_linear = %(value)3.3f
  textRenderer_color = rgb(255,0,0)
  textRenderer_family = Verdana
  textRenderer_size = 3.6
  unit_custom_scale = 1
  unit_scheme = 0
FEATURE [Drawing::FeatureViewPython] dim012  # drawing view (typed FeaturePython)
  Rotation = 0
  ViewResult = <g> \n  <line x1="49.230000" y1="193.167000" x2="32.132470" y2="193.167000" style="stroke:rgb(0,0,255);stroke-width:0.30" />\n<line x1="38.130000" y1="203.167000" x2="32.132470" y2="203.167000" style="stroke:rgb(0,0,255);stroke-width:0.30" />\n<line x1="33.132470" y1="193.167000" x2="33.132470" y2="203.167000" style="stroke:rgb(0,0,255);stroke-width:0.30" /> \n  <polygon points="33.132470,203.167000 32.132470,206.167000 33.132470,207.167000 34.132470,206.167000" style="fill:rgb(0,0,255);stroke:rgb(0,0,255);stroke-width:0" /><polygon points="33.132470,193.167000 34.132470,190.167000 33.132470,189.167000 32.132470,190.167000" style="fill:rgb(0,0,255);stroke:rgb(0,0,255);stroke-width:0" /> \n  <text x="31.132470" y="198.167000" font-family="Verdana" font-size="3.6" fill="rgb(255,0,0)" text-anchor="middle" transform="rotate(-90.000000 31.132470,198.167000)" >10</text> </g>
  Visible = false
  X = 0
  Y = 0
  arrowL1 = 3
  arrowL2 = 1
  arrowW = 2
  arrow_scheme = 0
  autoPlaceOffset = 2
  autoPlaceText = true
  click1_x = 33.1325
  click1_y = 197.552
  click2_x = 33.1325
  click2_y = 197.552
  comma_decimal_place = false
  dimension_line_overshoot = 1
  gap_datum_points = 2
  halfDimension_linear = false
  lineColor = rgb(0,0,255)
  strokeWidth = 0.3
  textFormat_linear = %(value)3.3f
  textRenderer_color = rgb(255,0,0)
  textRenderer_family = Verdana
  textRenderer_size = 3.6
  unit_custom_scale = 1
  unit_scheme = 0
FEATURE [Drawing::FeatureViewPython] dim013  # drawing view (typed FeaturePython)
  Rotation = 0
  ViewResult = <g> \n  <line x1="168.660000" y1="119.033300" x2="168.660000" y2="136.428973" style="stroke:rgb(0,0,255);stroke-width:0.30" />\n<line x1="163.760000" y1="129.333300" x2="163.760000" y2="136.428973" style="stroke:rgb(0,0,255);stroke-width:0.30" />\n<line x1="168.660000" y1="135.428973" x2="163.760000" y2="135.428973" style="stroke:rgb(0,0,255);stroke-width:0.30" /> \n  <polygon points="163.760000,135.428973 160.760000,134.428973 159.760000,135.428973 160.760000,136.428973" style="fill:rgb(0,0,255);stroke:rgb(0,0,255);stroke-width:0" /><polygon points="168.660000,135.428973 171.660000,136.428973 172.660000,135.428973 171.660000,134.428973" style="fill:rgb(0,0,255);stroke:rgb(0,0,255);stroke-width:0" /> \n  <text x="166.210000" y="133.428973" font-family="Verdana" font-size="3.6" fill="rgb(255,0,0)" text-anchor="middle" transform="rotate(0.000000 166.210000,133.428973)" >4.9</text> </g>
  Visible = false
  X = 0
  Y = 0
  arrowL1 = 3
  arrowL2 = 1
  arrowW = 2
  arrow_scheme = 0
  autoPlaceOffset = 2
  autoPlaceText = true
  click1_x = 165.455
  click1_y = 135.429
  click2_x = 165.455
  click2_y = 135.429
  comma_decimal_place = false
  dimension_line_overshoot = 1
  gap_datum_points = 2
  halfDimension_linear = false
  lineColor = rgb(0,0,255)
  strokeWidth = 0.3
  textFormat_linear = %(value)3.3f
  textRenderer_color = rgb(255,0,0)
  textRenderer_family = Verdana
  textRenderer_size = 3.6
  unit_custom_scale = 1
  unit_scheme = 0
FEATURE [Drawing::FeatureViewPython] dim014  # drawing view (typed FeaturePython)
  Rotation = 0
  ViewResult = <g> \n  <line x1="184.260000" y1="119.033300" x2="184.260000" y2="136.221895" style="stroke:rgb(0,0,255);stroke-width:0.30" />\n<line x1="168.660000" y1="119.033300" x2="168.660000" y2="136.221895" style="stroke:rgb(0,0,255);stroke-width:0.30" />\n<line x1="184.260000" y1="135.221895" x2="168.660000" y2="135.221895" style="stroke:rgb(0,0,255);stroke-width:0.30" /> \n  <polygon points="168.660000,135.221895 171.660000,136.221895 172.660000,135.221895 171.660000,134.221895" style="fill:rgb(0,0,255);stroke:rgb(0,0,255);stroke-width:0" /><polygon points="184.260000,135.221895 181.260000,134.221895 180.260000,135.221895 181.260000,136.221895" style="fill:rgb(0,0,255);stroke:rgb(0,0,255);stroke-width:0" /> \n  <text x="176.460000" y="133.221895" font-family="Verdana" font-size="3.6" fill="rgb(255,0,0)" text-anchor="middle" transform="rotate(0.000000 176.460000,133.221895)" >15.6</text> </g>
  Visible = false
  X = 0
  Y = 0
  arrowL1 = 3
  arrowL2 = 1
  arrowW = 2
  arrow_scheme = 0
  autoPlaceOffset = 2
  autoPlaceText = true
  click1_x = 176.637
  click1_y = 135.222
  click2_x = 176.637
  click2_y = 135.222
  comma_decimal_place = false
  dimension_line_overshoot = 1
  gap_datum_points = 2
  halfDimension_linear = false
  lineColor = rgb(0,0,255)
  strokeWidth = 0.3
  textFormat_linear = %(value)3.3f
  textRenderer_color = rgb(255,0,0)
  textRenderer_family = Verdana
  textRenderer_size = 3.6
  unit_custom_scale = 1
  unit_scheme = 0
FEATURE [Drawing::FeatureViewPython] dim015  # drawing view (typed FeaturePython)
  Rotation = 0
  ViewResult = <g> \n  <line x1="184.260000" y1="119.033300" x2="184.260000" y2="136.428973" style="stroke:rgb(0,0,255);stroke-width:0.30" />\n<line x1="189.040000" y1="129.333300" x2="189.040000" y2="136.428973" style="stroke:rgb(0,0,255);stroke-width:0.30" />\n<line x1="184.260000" y1="135.428973" x2="189.040000" y2="135.428973" style="stroke:rgb(0,0,255);stroke-width:0.30" /> \n  <polygon points="189.040000,135.428973 192.040000,136.428973 193.040000,135.428973 192.040000,134.428973" style="fill:rgb(0,0,255);stroke:rgb(0,0,255);stroke-width:0" /><polygon points="184.260000,135.428973 181.260000,134.428973 180.260000,135.428973 181.260000,136.428973" style="fill:rgb(0,0,255);stroke:rgb(0,0,255);stroke-width:0" /> \n  <text x="186.650000" y="133.428973" font-family="Verdana" font-size="3.6" fill="rgb(255,0,0)" text-anchor="middle" transform="rotate(0.000000 186.650000,133.428973)" >4.78</text> </g>
  Visible = false
  X = 0
  Y = 0
  arrowL1 = 3
  arrowL2 = 1
  arrowW = 2
  arrow_scheme = 0
  autoPlaceOffset = 2
  autoPlaceText = true
  click1_x = 188.648
  click1_y = 135.429
  click2_x = 188.648
  click2_y = 135.429
  comma_decimal_place = false
  dimension_line_overshoot = 1
  gap_datum_points = 2
  halfDimension_linear = false
  lineColor = rgb(0,0,255)
  strokeWidth = 0.3
  textFormat_linear = %(value)3.3f
  textRenderer_color = rgb(255,0,0)
  textRenderer_family = Verdana
  textRenderer_size = 3.6
  unit_custom_scale = 1
  unit_scheme = 0
FEATURE [Drawing::FeatureViewPython] dim016  # drawing view (typed FeaturePython)
  Rotation = 0
  ViewResult = <g> \n  <line x1="186.260000" y1="117.033300" x2="203.315147" y2="117.033300" style="stroke:rgb(0,0,255);stroke-width:0.30" />\n<line x1="191.040000" y1="127.333300" x2="203.315147" y2="127.333300" style="stroke:rgb(0,0,255);stroke-width:0.30" />\n<line x1="202.315147" y1="117.033300" x2="202.315147" y2="127.333300" style="stroke:rgb(0,0,255);stroke-width:0.30" /> \n  <polygon points="202.315147,127.333300 203.315147,124.333300 202.315147,123.333300 201.315147,124.333300" style="fill:rgb(0,0,255);stroke:rgb(0,0,255);stroke-width:0" /><polygon points="202.315147,117.033300 201.315147,120.033300 202.315147,121.033300 203.315147,120.033300" style="fill:rgb(0,0,255);stroke:rgb(0,0,255);stroke-width:0" /> \n  <text x="200.315147" y="122.183300" font-family="Verdana" font-size="3.6" fill="rgb(255,0,0)" text-anchor="middle" transform="rotate(-90.000000 200.315147,122.183300)" >10.3</text> </g>
  Visible = false
  X = 0
  Y = 0
  arrowL1 = 3
  arrowL2 = 1
  arrowW = 2
  arrow_scheme = 0
  autoPlaceOffset = 2
  autoPlaceText = true
  click1_x = 202.315
  click1_y = 126.732
  click2_x = 202.315
  click2_y = 126.732
  comma_decimal_place = false
  dimension_line_overshoot = 1
  gap_datum_points = 2
  halfDimension_linear = false
  lineColor = rgb(0,0,255)
  strokeWidth = 0.3
  textFormat_linear = %(value)3.3f
  textRenderer_color = rgb(255,0,0)
  textRenderer_family = Verdana
  textRenderer_size = 3.6
  unit_custom_scale = 1
  unit_scheme = 0
FEATURE [Drawing::FeatureViewPython] dim017  # drawing view (typed FeaturePython)
  Rotation = 0
  ViewResult = <g> \n  <line x1="163.760000" y1="129.333300" x2="163.760000" y2="145.333324" style="stroke:rgb(0,0,255);stroke-width:0.30" />\n<line x1="189.040000" y1="129.333300" x2="189.040000" y2="145.333324" style="stroke:rgb(0,0,255);stroke-width:0.30" />\n<line x1="163.760000" y1="144.333324" x2="189.040000" y2="144.333324" style="stroke:rgb(0,0,255);stroke-width:0.30" /> \n  <polygon points="189.040000,144.333324 186.040000,143.333324 185.040000,144.333324 186.040000,145.333324" style="fill:rgb(0,0,255);stroke:rgb(0,0,255);stroke-width:0" /><polygon points="163.760000,144.333324 166.760000,145.333324 167.760000,144.333324 166.760000,143.333324" style="fill:rgb(0,0,255);stroke:rgb(0,0,255);stroke-width:0" /> \n  <text x="176.400000" y="142.333324" font-family="Verdana" font-size="3.6" fill="rgb(255,0,0)" text-anchor="middle" transform="rotate(0.000000 176.400000,142.333324)" >25.28</text> </g>
  Visible = false
  X = 0
  Y = 0
  arrowL1 = 3
  arrowL2 = 1
  arrowW = 2
  arrow_scheme = 0
  autoPlaceOffset = 2
  autoPlaceText = true
  click1_x = 177.88
  click1_y = 144.333
  click2_x = 177.88
  click2_y = 144.333
  comma_decimal_place = false
  dimension_line_overshoot = 1
  gap_datum_points = 2
  halfDimension_linear = false
  lineColor = rgb(0,0,255)
  strokeWidth = 0.3
  textFormat_linear = %(value)3.3f
  textRenderer_color = rgb(255,0,0)
  textRenderer_family = Verdana
  textRenderer_size = 3.6
  unit_custom_scale = 1
  unit_scheme = 0
FEATURE [Drawing::FeatureViewPython] dim018  # drawing view (typed FeaturePython)
  Rotation = 0
  ViewResult = <g> \n  <line x1="161.760000" y1="106.833300" x2="152.237675" y2="106.833300" style="stroke:rgb(0,0,255);stroke-width:0.30" />\n<line x1="161.760000" y1="127.333300" x2="152.237675" y2="127.333300" style="stroke:rgb(0,0,255);stroke-width:0.30" />\n<line x1="153.237675" y1="106.833300" x2="153.237675" y2="127.333300" style="stroke:rgb(0,0,255);stroke-width:0.30" /> \n  <polygon points="153.237675,127.333300 154.237675,124.333300 153.237675,123.333300 152.237675,124.333300" style="fill:rgb(0,0,255);stroke:rgb(0,0,255);stroke-width:0" /><polygon points="153.237675,106.833300 152.237675,109.833300 153.237675,110.833300 154.237675,109.833300" style="fill:rgb(0,0,255);stroke:rgb(0,0,255);stroke-width:0" /> \n  <text x="151.237675" y="117.083300" font-family="Verdana" font-size="3.6" fill="rgb(255,0,0)" text-anchor="middle" transform="rotate(-90.000000 151.237675,117.083300)" >20.5</text> </g>
  Visible = false
  X = 0
  Y = 0
  arrowL1 = 3
  arrowL2 = 1
  arrowW = 2
  arrow_scheme = 0
  autoPlaceOffset = 2
  autoPlaceText = true
  click1_x = 153.238
  click1_y = 117.413
  click2_x = 153.238
  click2_y = 117.413
  comma_decimal_place = false
  dimension_line_overshoot = 1
  gap_datum_points = 2
  halfDimension_linear = false
  lineColor = rgb(0,0,255)
  strokeWidth = 0.3
  textFormat_linear = %(value)3.3f
  textRenderer_color = rgb(255,0,0)
  textRenderer_family = Verdana
  textRenderer_size = 3.6
  unit_custom_scale = 1
  unit_scheme = 0
FEATURE [Drawing::FeaturePage] Page004
  EditableTexts = AUTHOR NAME | CREATION DATE | SUPERVISOR NAME | CHECK DATE | SCALE | WEIGHT | NUMBER | SHEET | TITLE | SUBTITLE
  Group = -> [Ortho014,Ortho015,Ortho016,Ortho017,dim008,dim009,dim010,dia009,dim011,dim012,dim013,dim014,dim015,dim016,dim017,dim018]
  Template = <path>
FEATURE [Part::Chamfer] Chamfer
  Base = -> Box023
  Edges = 2 edges: [Edge1 r1=5 r2=12,Edge7 r1=10 r2=21]
FEATURE [Part::FeaturePython] Bend004  # WARN: FeaturePython — macro-defined, semantics opaque (R4)
  AutoMiter = true
  BendType = 0
  LengthList = [89]
  ReliefFactor = 0.7
  UseReliefFactor = false
  angle = -90
  baseObject = -> Chamfer [Face4]
  bendAList = [-90]
  extend1 = 0
  extend2 = 0
  gap1 = 0
  gap2 = 0
  invert = false
  kfactor = 0.5
  length = 89
  miterangle1 = 0
  miterangle2 = 0
  offset = 0
  radius = 1
  reliefType = 0
  reliefd = 1
  reliefw = 0.8
  sketchflip = false
  sketchinvert = false
  unfold = false
FEATURE [Part::FeaturePython] Extend001  label="Extend001_material_0.40ansi"  # WARN: FeaturePython — macro-defined, semantics opaque (R4)
  baseObject = -> Bend004 [Face15]
  gap1 = 0
  gap2 = 0
  length = 28.5
FEATURE [Part::Feature] Fusion002008006002001  label="开孔003-1"
  shape: bbox 120 x 91 x 94 mm, 255 faces, 8 solids (baked)
FEATURE [Part::Cut] Cut001002004
  Base = -> Extend001
  Tool = -> Fusion002008006002001
FEATURE [Drawing::FeatureViewPart] Ortho018  label="Ortho_0_010"
  Direction = (0,0,1)
  HiddenWidth = 0.15
  LineWidth = 0.35
  Rotation = 0
  Scale = 1.5
  ShowHiddenLines = false
  ShowSmoothLines = false
  Source = -> Cut001002004
  Tolerance = 0.05
  ViewResult = <g id="Ortho_0_010"\n   transform="rotate(0,67.5833,302.917) translate(67.5833,302.917) scale(1.5,1.5)"\n  >\n<g   fill="none"\n   stroke="rgb(0, 0, 0)"\n   stroke-linecap="butt"\n   stroke-linejoin="miter"\n   stroke-width="0.233333"\n   transform="scale(1,-1)"\n  >\n<path id= "1" d=" M 19.5 54.5 L 19.5 26 " />\n<path id= "2" d=" M 19.5 26 L 42.5 26 " />\n<path id= "3" d=" M 42.5 54.5 L 42.5 26 " />\n<path id= "4" d=" M 19.5 54.5 L 42.5 54.5 " />\n<circle cx ="32" cy ="31.2" r ="2.6" /><circle cx ="32" cy ="46.8" r ="2.6" /><path id= "7" d=" M 7.5 59.5 L 19.5 54.5 " />\n<path id= "8" d=" M 7.5 59.5 L 7.5 65.5 " />\n<path id= "9" d=" M 42.5 55.5 L 21.5 65.5 " />\n<path id= "10" d=" M 42.5 54.5 L 42.5 55.5 " />\n<path id= "11" d=" M 7.5 65.5 L 21.5 65.5 " />\n<path d="M7.5,65.5 L7.5,66.0598  L7.5,66.6126  L7.5,67.1514  L7.5,67.6694  L7.5,68.1602  L7.5,68.6174  L7.5,69.0355  L7.5,69.4092  L7.5,69.7336  L7.5,70.0048  L7.5,70.2194  L7.5,70.3746  L7.5,70.4686  L7.5,70.5 " /><path d="M21.5,65.5 L21.5,66.0598  L21.5,66.6126  L21.5,67.1514  L21.5,67.6694  L21.5,68.1602  L21.5,68.6174  L21.5,69.0355  L21.5,69.4092  L21.5,69.7336  L21.5,70.0048  L21.5,70.2194  L21.5,70.3746  L21.5,70.4686  L21.5,70.5 " /><path id= "14" d=" M 7.5 70.5 L 21.5 70.5 " />\n</g>\n</g>
  Visible = false
  X = 67.5833
  Y = 302.917
FEATURE [Drawing::FeatureViewPart] Ortho019  label="Ortho_1_002"
  Direction = (0.57735,0.57735,0.57735)
  HiddenWidth = 0.15
  LineWidth = 0.35
  Rotation = 0
  Scale = 1.5
  ShowHiddenLines = false
  ShowSmoothLines = false
  Source = -> Cut001002004
  Tolerance = 0.05
  ViewResult = <blob: 3822 chars omitted>
  Visible = false
  X = 245.741
  Y = 146.449
FEATURE [Drawing::FeatureViewPart] Ortho020  label="Ortho_0_011"
  Direction = (0,1,0)
  HiddenWidth = 0.15
  LineWidth = 0.35
  Rotation = 90
  Scale = 1.5
  ShowHiddenLines = false
  ShowSmoothLines = false
  Source = -> Cut001002004
  Tolerance = 0.05
  ViewResult = <g id="Ortho_0_011"\n   transform="rotate(90,67.5833,101.333) translate(67.5833,101.333) scale(1.5,1.5)"\n  >\n<g   fill="none"\n   stroke="rgb(0, 0, 0)"\n   stroke-linecap="butt"\n   stroke-linejoin="miter"\n   stroke-width="0.233333"\n   transform="scale(1,-1)"\n  >\n<path id= "1" d=" M 44.5 42.5 L 44.5 21.5 " />\n<path id= "2" d=" M 44.5 42.5 L 48.5 42.5 " />\n<path id= "3" d=" M 48.5 42.5 L 48.5 21.5 " />\n<path id= "4" d=" M 48.5 7.5 L 48.5 21.5 " />\n<path d="M48.5,7.5 Q48.4843,7.5 48.4686,7.5  Q48.4216,7.5 48.3746,7.5  Q48.297,7.5 48.2194,7.5  Q48.1121,7.5 48.0048,7.5  Q47.8692,7.5 47.7336,7.5  Q47.5714,7.5 47.4092,7.5  Q47.2223,7.5 47.0355,7.5  Q46.8265,7.5 46.6174,7.5  Q46.3888,7.5 46.1602,7.5  Q45.9148,7.5 45.6694,7.5  Q45.4104,7.5 45.1514,7.5  Q44.882,7.5 44.6126,7.5  Q44.0618,7.5 43.5,7.5 " /><path d="M48.5,21.5 Q48.4843,21.5 48.4686,21.5  Q48.4216,21.5 48.3746,21.5  Q48.297,21.5 48.2194,21.5  Q48.1121,21.5 48.0048,21.5  Q47.8692,21.5 47.7336,21.5  Q47.5714,21.5 47.4092,21.5  Q47.2223,21.5 47.0355,21.5  Q46.8265,21.5 46.6174,21.5  Q46.3888,21.5 46.1602,21.5  Q45.9148,21.5 45.6694,21.5  Q45.4104,21.5 45.1514,21.5  Q44.882,21.5 44.6126,21.5  Q44.0618,21.5 43.5,21.5 " /><path id= "7" d=" M 43.5 7.5 L 43.5 21.5 " />\n<path id= "8" d=" M 43.5 7.5 L -45.5 7.5 " />\n<path id= "9" d=" M -45.5 21.5 L 43.5 21.5 " />\n<path id= "10" d=" M -45.5 7.5 L -45.5 21.5 " />\n<circle cx ="-36.5" cy ="14.6" r ="2.25" /><circle cx ="-24.5" cy ="14.6" r ="2.25" /><circle cx ="-0.5" cy ="14.6" r ="2.25" /><circle cx ="-12.5" cy ="14.6" r ="2.25" /><circle cx ="35.5" cy ="14.6" r ="3.25" /><circle cx ="23.5" cy ="14.6" r ="2.25" /><circle cx ="11.5" cy ="14.6" r ="2.25" /></g>\n</g>
  Visible = false
  X = 67.5833
  Y = 101.333
FEATURE [Drawing::FeatureViewPython] dim019  # drawing view (typed FeaturePython)
  Rotation = 0
  ViewResult = <g> \n  <line x1="76.833300" y1="166.583000" x2="46.663047" y2="166.583000" style="stroke:rgb(0,0,255);stroke-width:0.30" />\n<line x1="76.833300" y1="33.083000" x2="46.663047" y2="33.083000" style="stroke:rgb(0,0,255);stroke-width:0.30" />\n<line x1="47.663047" y1="166.583000" x2="47.663047" y2="33.083000" style="stroke:rgb(0,0,255);stroke-width:0.30" /> \n  <polygon points="47.663047,33.083000 46.663047,36.083000 47.663047,37.083000 48.663047,36.083000" style="fill:rgb(0,0,255);stroke:rgb(0,0,255);stroke-width:0" /><polygon points="47.663047,166.583000 48.663047,163.583000 47.663047,162.583000 46.663047,163.583000" style="fill:rgb(0,0,255);stroke:rgb(0,0,255);stroke-width:0" /> \n  <text x="45.663047" y="99.833000" font-family="Verdana" font-size="3.6" fill="rgb(255,0,0)" text-anchor="middle" transform="rotate(-90.000000 45.663047,99.833000)" >89</text> </g>
  Visible = false
  X = 0
  Y = 0
  arrowL1 = 3
  arrowL2 = 1
  arrowW = 2
  arrow_scheme = 0
  autoPlaceOffset = 2
  autoPlaceText = true
  click1_x = 47.663
  click1_y = 67.4153
  click2_x = 47.663
  click2_y = 67.4153
  comma_decimal_place = false
  dimension_line_overshoot = 1
  gap_datum_points = 2
  halfDimension_linear = false
  lineColor = rgb(0,0,255)
  strokeWidth = 0.3
  textFormat_linear = %(value)3.3f
  textRenderer_color = rgb(255,0,0)
  textRenderer_family = Verdana
  textRenderer_size = 3.6
  unit_custom_scale = 1
  unit_scheme = 0
FEATURE [Drawing::FeatureViewPython] dim020  # drawing view (typed FeaturePython)
  Rotation = 0
  ViewResult = <g> \n  <line x1="78.833300" y1="31.083000" x2="78.833300" y2="18.752254" style="stroke:rgb(0,0,255);stroke-width:0.30" />\n<line x1="99.833300" y1="31.083000" x2="99.833300" y2="18.752254" style="stroke:rgb(0,0,255);stroke-width:0.30" />\n<line x1="78.833300" y1="19.752254" x2="99.833300" y2="19.752254" style="stroke:rgb(0,0,255);stroke-width:0.30" /> \n  <polygon points="99.833300,19.752254 96.833300,18.752254 95.833300,19.752254 96.833300,20.752254" style="fill:rgb(0,0,255);stroke:rgb(0,0,255);stroke-width:0" /><polygon points="78.833300,19.752254 81.833300,20.752254 82.833300,19.752254 81.833300,18.752254" style="fill:rgb(0,0,255);stroke:rgb(0,0,255);stroke-width:0" /> \n  <text x="89.333300" y="17.752254" font-family="Verdana" font-size="3.6" fill="rgb(255,0,0)" text-anchor="middle" transform="rotate(0.000000 89.333300,17.752254)" >14</text> </g>
  Visible = false
  X = 0
  Y = 0
  arrowL1 = 3
  arrowL2 = 1
  arrowW = 2
  arrow_scheme = 0
  autoPlaceOffset = 2
  autoPlaceText = true
  click1_x = 88.0263
  click1_y = 19.7523
  click2_x = 88.0263
  click2_y = 19.7523
  comma_decimal_place = false
  dimension_line_overshoot = 1
  gap_datum_points = 2
  halfDimension_linear = false
  lineColor = rgb(0,0,255)
  strokeWidth = 0.3
  textFormat_linear = %(value)3.3f
  textRenderer_color = rgb(255,0,0)
  textRenderer_family = Verdana
  textRenderer_size = 3.6
  unit_custom_scale = 1
  unit_scheme = 0
FEATURE [Drawing::FeatureViewPython] dim021  # drawing view (typed FeaturePython)
  Rotation = 0
  ViewResult = <g> \n  <line x1="96.833300" y1="265.917000" x2="96.833300" y2="276.672756" style="stroke:rgb(0,0,255);stroke-width:0.30" />\n<line x1="131.333300" y1="265.917000" x2="131.333300" y2="276.672756" style="stroke:rgb(0,0,255);stroke-width:0.30" />\n<line x1="96.833300" y1="275.672756" x2="131.333300" y2="275.672756" style="stroke:rgb(0,0,255);stroke-width:0.30" /> \n  <polygon points="131.333300,275.672756 128.333300,274.672756 127.333300,275.672756 128.333300,276.672756" style="fill:rgb(0,0,255);stroke:rgb(0,0,255);stroke-width:0" /><polygon points="96.833300,275.672756 99.833300,276.672756 100.833300,275.672756 99.833300,274.672756" style="fill:rgb(0,0,255);stroke:rgb(0,0,255);stroke-width:0" /> \n  <text x="114.083300" y="273.672756" font-family="Verdana" font-size="3.6" fill="rgb(255,0,0)" text-anchor="middle" transform="rotate(0.000000 114.083300,273.672756)" >23</text> </g>
  Visible = false
  X = 0
  Y = 0
  arrowL1 = 3
  arrowL2 = 1
  arrowW = 2
  arrow_scheme = 0
  autoPlaceOffset = 2
  autoPlaceText = true
  click1_x = 119.802
  click1_y = 275.673
  click2_x = 119.802
  click2_y = 275.673
  comma_decimal_place = false
  dimension_line_overshoot = 1
  gap_datum_points = 2
  halfDimension_linear = false
  lineColor = rgb(0,0,255)
  strokeWidth = 0.3
  textFormat_linear = %(value)3.3f
  textRenderer_color = rgb(255,0,0)
  textRenderer_family = Verdana
  textRenderer_size = 3.6
  unit_custom_scale = 1
  unit_scheme = 0
FEATURE [Drawing::FeatureViewPython] dim022  # drawing view (typed FeaturePython)
  Rotation = 0
  ViewResult = <g> \n  <line x1="133.333300" y1="221.167000" x2="154.724060" y2="221.167000" style="stroke:rgb(0,0,255);stroke-width:0.30" />\n<line x1="133.333300" y1="263.917000" x2="154.724060" y2="263.917000" style="stroke:rgb(0,0,255);stroke-width:0.30" />\n<line x1="153.724060" y1="221.167000" x2="153.724060" y2="263.917000" style="stroke:rgb(0,0,255);stroke-width:0.30" /> \n  <polygon points="153.724060,263.917000 154.724060,260.917000 153.724060,259.917000 152.724060,260.917000" style="fill:rgb(0,0,255);stroke:rgb(0,0,255);stroke-width:0" /><polygon points="153.724060,221.167000 152.724060,224.167000 153.724060,225.167000 154.724060,224.167000" style="fill:rgb(0,0,255);stroke:rgb(0,0,255);stroke-width:0" /> \n  <text x="151.724060" y="242.542000" font-family="Verdana" font-size="3.6" fill="rgb(255,0,0)" text-anchor="middle" transform="rotate(-90.000000 151.724060,242.542000)" >28.5</text> </g>
  Visible = false
  X = 0
  Y = 0
  arrowL1 = 3
  arrowL2 = 1
  arrowW = 2
  arrow_scheme = 0
  autoPlaceOffset = 2
  autoPlaceText = true
  click1_x = 153.724
  click1_y = 246.474
  click2_x = 153.724
  click2_y = 246.474
  comma_decimal_place = false
  dimension_line_overshoot = 1
  gap_datum_points = 2
  halfDimension_linear = false
  lineColor = rgb(0,0,255)
  strokeWidth = 0.3
  textFormat_linear = %(value)3.3f
  textRenderer_color = rgb(255,0,0)
  textRenderer_family = Verdana
  textRenderer_size = 3.6
  unit_custom_scale = 1
  unit_scheme = 0
FEATURE [Drawing::FeatureViewPython] dim023  # drawing view (typed FeaturePython)
  Rotation = 0
  ViewResult = <g> \n  <line x1="115.583300" y1="234.717000" x2="115.583300" y2="233.986169" style="stroke:rgb(0,0,255);stroke-width:0.30" />\n<line x1="131.333300" y1="223.167000" x2="131.333300" y2="233.986169" style="stroke:rgb(0,0,255);stroke-width:0.30" />\n<line x1="115.583300" y1="232.986169" x2="131.333300" y2="232.986169" style="stroke:rgb(0,0,255);stroke-width:0.30" /> \n  <polygon points="131.333300,232.986169 128.333300,231.986169 127.333300,232.986169 128.333300,233.986169" style="fill:rgb(0,0,255);stroke:rgb(0,0,255);stroke-width:0" /><polygon points="115.583300,232.986169 118.583300,233.986169 119.583300,232.986169 118.583300,231.986169" style="fill:rgb(0,0,255);stroke:rgb(0,0,255);stroke-width:0" /> \n  <text x="123.458300" y="230.986169" font-family="Verdana" font-size="3.6" fill="rgb(255,0,0)" text-anchor="middle" transform="rotate(0.000000 123.458300,230.986169)" >10.5</text> </g>
  Visible = false
  X = 0
  Y = 0
  arrowL1 = 3
  arrowL2 = 1
  arrowW = 2
  arrow_scheme = 0
  autoPlaceOffset = 2
  autoPlaceText = true
  click1_x = 131.065
  click1_y = 232.986
  click2_x = 131.065
  click2_y = 232.986
  comma_decimal_place = false
  dimension_line_overshoot = 1
  gap_datum_points = 2
  halfDimension_linear = false
  lineColor = rgb(0,0,255)
  strokeWidth = 0.3
  textFormat_linear = %(value)3.3f
  textRenderer_color = rgb(255,0,0)
  textRenderer_family = Verdana
  textRenderer_size = 3.6
  unit_custom_scale = 1
  unit_scheme = 0
FEATURE [Drawing::FeatureViewPython] dim024  # drawing view (typed FeaturePython)
  Rotation = 0
  ViewResult = <g> \n  <line x1="115.583300" y1="258.117000" x2="115.583300" y2="257.143009" style="stroke:rgb(0,0,255);stroke-width:0.30" />\n<line x1="96.833300" y1="261.917000" x2="96.833300" y2="255.143009" style="stroke:rgb(0,0,255);stroke-width:0.30" />\n<line x1="115.583300" y1="256.143009" x2="96.833300" y2="256.143009" style="stroke:rgb(0,0,255);stroke-width:0.30" /> \n  <polygon points="96.833300,256.143009 99.833300,257.143009 100.833300,256.143009 99.833300,255.143009" style="fill:rgb(0,0,255);stroke:rgb(0,0,255);stroke-width:0" /><polygon points="115.583300,256.143009 112.583300,255.143009 111.583300,256.143009 112.583300,257.143009" style="fill:rgb(0,0,255);stroke:rgb(0,0,255);stroke-width:0" /> \n  <text x="106.208300" y="254.143009" font-family="Verdana" font-size="3.6" fill="rgb(255,0,0)" text-anchor="middle" transform="rotate(0.000000 106.208300,254.143009)" >12.5</text> </g>
  Visible = false
  X = 0
  Y = 0
  arrowL1 = 3
  arrowL2 = 1
  arrowW = 2
  arrow_scheme = 0
  autoPlaceOffset = 2
  autoPlaceText = true
  click1_x = 97.6683
  click1_y = 256.143
  click2_x = 97.6683
  click2_y = 256.143
  comma_decimal_place = false
  dimension_line_overshoot = 1
  gap_datum_points = 2
  halfDimension_linear = false
  lineColor = rgb(0,0,255)
  strokeWidth = 0.3
  textFormat_linear = %(value)3.3f
  textRenderer_color = rgb(255,0,0)
  textRenderer_family = Verdana
  textRenderer_size = 3.6
  unit_custom_scale = 1
  unit_scheme = 0
FEATURE [Drawing::FeatureViewPython] dim025  # drawing view (typed FeaturePython)
  Rotation = 0
  ViewResult = <g> \n  <line x1="113.583300" y1="232.717000" x2="84.730267" y2="232.717000" style="stroke:rgb(0,0,255);stroke-width:0.30" />\n<line x1="113.583300" y1="256.117000" x2="84.730267" y2="256.117000" style="stroke:rgb(0,0,255);stroke-width:0.30" />\n<line x1="85.730267" y1="232.717000" x2="85.730267" y2="256.117000" style="stroke:rgb(0,0,255);stroke-width:0.30" /> \n  <polygon points="85.730267,256.117000 86.730267,253.117000 85.730267,252.117000 84.730267,253.117000" style="fill:rgb(0,0,255);stroke:rgb(0,0,255);stroke-width:0" /><polygon points="85.730267,232.717000 84.730267,235.717000 85.730267,236.717000 86.730267,235.717000" style="fill:rgb(0,0,255);stroke:rgb(0,0,255);stroke-width:0" /> \n  <text x="83.730267" y="244.417000" font-family="Verdana" font-size="3.6" fill="rgb(255,0,0)" text-anchor="middle" transform="rotate(-90.000000 83.730267,244.417000)" >15.6</text> </g>
  Visible = false
  X = 0
  Y = 0
  arrowL1 = 3
  arrowL2 = 1
  arrowW = 2
  arrow_scheme = 0
  autoPlaceOffset = 2
  autoPlaceText = true
  click1_x = 85.7303
  click1_y = 254.292
  click2_x = 85.7303
  click2_y = 254.292
  comma_decimal_place = false
  dimension_line_overshoot = 1
  gap_datum_points = 2
  halfDimension_linear = false
  lineColor = rgb(0,0,255)
  strokeWidth = 0.3
  textFormat_linear = %(value)3.3f
  textRenderer_color = rgb(255,0,0)
  textRenderer_family = Verdana
  textRenderer_size = 3.6
  unit_custom_scale = 1
  unit_scheme = 0
FEATURE [Drawing::FeatureViewPython] dim026  # drawing view (typed FeaturePython)
  Rotation = 0
  ViewResult = <g> \n  <line x1="96.833300" y1="223.167000" x2="96.833300" y2="222.573395" style="stroke:rgb(0,0,255);stroke-width:0.30" />\n<line x1="131.333300" y1="223.167000" x2="131.333300" y2="222.573395" style="stroke:rgb(0,0,255);stroke-width:0.30" />\n<line x1="96.833300" y1="221.573395" x2="131.333300" y2="221.573395" style="stroke:rgb(0,0,255);stroke-width:0.30" /> \n  <polygon points="131.333300,221.573395 128.333300,220.573395 127.333300,221.573395 128.333300,222.573395" style="fill:rgb(0,0,255);stroke:rgb(0,0,255);stroke-width:0" /><polygon points="96.833300,221.573395 99.833300,222.573395 100.833300,221.573395 99.833300,220.573395" style="fill:rgb(0,0,255);stroke:rgb(0,0,255);stroke-width:0" /> \n  <text x="114.083300" y="219.573395" font-family="Verdana" font-size="3.6" fill="rgb(255,0,0)" text-anchor="middle" transform="rotate(0.000000 114.083300,219.573395)" >23</text> </g>
  Visible = false
  X = 0
  Y = 0
  arrowL1 = 3
  arrowL2 = 1
  arrowW = 2
  arrow_scheme = 0
  autoPlaceOffset = 2
  autoPlaceText = true
  click1_x = 115.964
  click1_y = 221.573
  click2_x = 115.964
  click2_y = 221.573
  comma_decimal_place = false
  dimension_line_overshoot = 1
  gap_datum_points = 2
  halfDimension_linear = false
  lineColor = rgb(0,0,255)
  strokeWidth = 0.3
  textFormat_linear = %(value)3.3f
  textRenderer_color = rgb(255,0,0)
  textRenderer_family = Verdana
  textRenderer_size = 3.6
  unit_custom_scale = 1
  unit_scheme = 0
FEATURE [Drawing::FeatureViewPython] dim027  # drawing view (typed FeaturePython)
  Rotation = 0
  ViewResult = <g> \n  <line x1="113.583300" y1="232.717000" x2="84.523189" y2="232.717000" style="stroke:rgb(0,0,255);stroke-width:0.30" />\n<line x1="94.833300" y1="221.167000" x2="84.523189" y2="221.167000" style="stroke:rgb(0,0,255);stroke-width:0.30" />\n<line x1="85.523189" y1="232.717000" x2="85.523189" y2="221.167000" style="stroke:rgb(0,0,255);stroke-width:0.30" /> \n  <polygon points="85.523189,221.167000 84.523189,224.167000 85.523189,225.167000 86.523189,224.167000" style="fill:rgb(0,0,255);stroke:rgb(0,0,255);stroke-width:0" /><polygon points="85.523189,232.717000 86.523189,229.717000 85.523189,228.717000 84.523189,229.717000" style="fill:rgb(0,0,255);stroke:rgb(0,0,255);stroke-width:0" /> \n  <text x="83.523189" y="226.942000" font-family="Verdana" font-size="3.6" fill="rgb(255,0,0)" text-anchor="middle" transform="rotate(-90.000000 83.523189,226.942000)" >7.7</text> </g>
  Visible = false
  X = 0
  Y = 0
  arrowL1 = 3
  arrowL2 = 1
  arrowW = 2
  arrow_scheme = 0
  autoPlaceOffset = 2
  autoPlaceText = true
  click1_x = 85.5232
  click1_y = 223.437
  click2_x = 85.5232
  click2_y = 223.437
  comma_decimal_place = false
  dimension_line_overshoot = 1
  gap_datum_points = 2
  halfDimension_linear = false
  lineColor = rgb(0,0,255)
  strokeWidth = 0.3
  textFormat_linear = %(value)3.3f
  textRenderer_color = rgb(255,0,0)
  textRenderer_family = Verdana
  textRenderer_size = 3.6
  unit_custom_scale = 1
  unit_scheme = 0
FEATURE [Drawing::FeatureViewPython] dim028  # drawing view (typed FeaturePython)
  Rotation = 0
  ViewResult = <g> \n  <line x1="113.583300" y1="256.117000" x2="84.581171" y2="256.117000" style="stroke:rgb(0,0,255);stroke-width:0.30" />\n<line x1="94.833300" y1="263.917000" x2="84.581171" y2="263.917000" style="stroke:rgb(0,0,255);stroke-width:0.30" />\n<line x1="85.581171" y1="256.117000" x2="85.581171" y2="263.917000" style="stroke:rgb(0,0,255);stroke-width:0.30" /> \n  <polygon points="85.581171,263.917000 84.581171,266.917000 85.581171,267.917000 86.581171,266.917000" style="fill:rgb(0,0,255);stroke:rgb(0,0,255);stroke-width:0" /><polygon points="85.581171,256.117000 86.581171,253.117000 85.581171,252.117000 84.581171,253.117000" style="fill:rgb(0,0,255);stroke:rgb(0,0,255);stroke-width:0" /> \n  <text x="83.581171" y="260.017000" font-family="Verdana" font-size="3.6" fill="rgb(255,0,0)" text-anchor="middle" transform="rotate(-90.000000 83.581171,260.017000)" >5.2</text> </g>
  Visible = false
  X = 0
  Y = 0
  arrowL1 = 3
  arrowL2 = 1
  arrowW = 2
  arrow_scheme = 0
  autoPlaceOffset = 2
  autoPlaceText = true
  click1_x = 85.5812
  click1_y = 262.111
  click2_x = 85.5812
  click2_y = 262.111
  comma_decimal_place = false
  dimension_line_overshoot = 1
  gap_datum_points = 2
  halfDimension_linear = false
  lineColor = rgb(0,0,255)
  strokeWidth = 0.3
  textFormat_linear = %(value)3.3f
  textRenderer_color = rgb(255,0,0)
  textRenderer_family = Verdana
  textRenderer_size = 3.6
  unit_custom_scale = 1
  unit_scheme = 0
FEATURE [Drawing::FeatureViewPython] dimStack018  # drawing view (typed FeaturePython)
  Rotation = 0
  ViewResult = <g> <line x1="76.833300" y1="204.667000" x2="57.445678" y2="204.667000" style="stroke:rgb(0,0,255);stroke-width:0.30" />\n<line x1="94.833300" y1="221.167000" x2="57.445678" y2="221.167000" style="stroke:rgb(0,0,255);stroke-width:0.30" />\n<line x1="58.445678" y1="204.667000" x2="58.445678" y2="221.167000" style="stroke:rgb(0,0,255);stroke-width:0.30" />\n<polygon points="58.445678,204.667000 57.445678,207.667000 58.445678,208.667000 59.445678,207.667000" style="fill:rgb(0,0,255);stroke:rgb(0,0,255);stroke-width:0" />\n<polygon points="58.445678,221.167000 59.445678,218.167000 58.445678,217.167000 57.445678,218.167000" style="fill:rgb(0,0,255);stroke:rgb(0,0,255);stroke-width:0" />\n<text x="56.445678" y="212.917000" font-family="Verdana" font-size="3.6" fill="rgb(255,0,0)" text-anchor="middle" transform="rotate(-90.000000 56.445678,212.917000)" >11</text> </g> 
  Visible = false
  X = 0
  Y = 0
  arrowL1 = 3
  arrowL2 = 1
  arrowW = 2
  arrow_scheme = 0
  autoPlaceOffset = 2
  click1_x = 58.4457
  click1_y = 217.68
  comma_decimal_place = false
  dimension_line_overshoot = 1
  gap_datum_points = 2
  lineColor = rgb(0,0,255)
  stack_offset = 7
  stack_offset0 = 0
  strokeWidth = 0.3
  textFormat_linear = %(value)3.3f
  textRenderer_color = rgb(255,0,0)
  textRenderer_family = Verdana
  textRenderer_size = 3.6
  unit_custom_scale = 1
  unit_scheme = 0
FEATURE [Drawing::FeatureViewPython] dimStack019  # drawing view (typed FeaturePython)
  Rotation = 0
  ViewResult = <g> <line x1="78.833300" y1="202.667000" x2="78.833300" y2="188.731082" style="stroke:rgb(0,0,255);stroke-width:0.30" />\n<line x1="131.333300" y1="219.167000" x2="131.333300" y2="188.731082" style="stroke:rgb(0,0,255);stroke-width:0.30" />\n<line x1="78.833300" y1="189.731082" x2="131.333300" y2="189.731082" style="stroke:rgb(0,0,255);stroke-width:0.30" />\n<polygon points="78.833300,189.731082 81.833300,190.731082 82.833300,189.731082 81.833300,188.731082" style="fill:rgb(0,0,255);stroke:rgb(0,0,255);stroke-width:0" />\n<polygon points="131.333300,189.731082 128.333300,188.731082 127.333300,189.731082 128.333300,190.731082" style="fill:rgb(0,0,255);stroke:rgb(0,0,255);stroke-width:0" />\n<text x="105.083300" y="187.731082" font-family="Verdana" font-size="3.6" fill="rgb(255,0,0)" text-anchor="middle" transform="rotate(0.000000 105.083300,187.731082)" >35</text> </g> 
  Visible = false
  X = 0
  Y = 0
  arrowL1 = 3
  arrowL2 = 1
  arrowW = 2
  arrow_scheme = 0
  autoPlaceOffset = 2
  click1_x = 115.417
  click1_y = 189.731
  comma_decimal_place = false
  dimension_line_overshoot = 1
  gap_datum_points = 2
  lineColor = rgb(0,0,255)
  stack_offset = 7
  stack_offset0 = 0
  strokeWidth = 0.3
  textFormat_linear = %(value)3.3f
  textRenderer_color = rgb(255,0,0)
  textRenderer_family = Verdana
  textRenderer_size = 3.6
  unit_custom_scale = 1
  unit_scheme = 0
FEATURE [Drawing::FeatureViewPython] dia010  # drawing view (typed FeaturePython)
  Rotation = 0
  ViewResult = <g>  <circle cx ="115.583300" cy ="232.717000" r="0.500000" stroke="none" fill="rgb(0,0,255)" /> \n<line x1="120.339048" y1="241.462064" x2="113.720092" y2="229.290857" style="stroke:rgb(0,0,255);stroke-width:0.30" />\n<polygon points="117.446508,236.143143 118.001247,239.256383 119.357491,239.657136 119.758243,238.300892" style="fill:rgb(0,0,255);stroke:rgb(0,0,255);stroke-width:0" />\n<polygon points="113.720092,229.290857 113.165353,226.177617 111.809109,225.776864 111.408357,227.133108" style="fill:rgb(0,0,255);stroke:rgb(0,0,255);stroke-width:0" />\n<line x1="120.339048" y1="241.462064" x2="157.577516" y2="241.462064" style="stroke:rgb(0,0,255);stroke-width:0.30" />\n<text x="138.958282" y="239.462064" font-family="Verdana" font-size="3.6" fill="rgb(255,0,0)" text-anchor="middle" transform="rotate(0.000000 138.958282,239.462064)" >Ø5.2</text> </g>
  Visible = false
  X = 0
  Y = 0
  arrowL1 = 3
  arrowL2 = 1
  arrowW = 2
  arrow_scheme = 0
  autoPlaceOffset = 2
  autoPlaceText = true
  centerPointDia = 1
  click1_x = 120.339
  click1_y = 241.462
  click2_x = 157.578
  click2_y = 238.718
  click3_x = 157.578
  click3_y = 238.718
  comma_decimal_place = false
  lineColor = rgb(0,0,255)
  strokeWidth = 0.3
  textFormat_circular = Ø%(value)3.3f
  textRenderer_color = rgb(255,0,0)
  textRenderer_family = Verdana
  textRenderer_size = 3.6
  unit_custom_scale = 1
  unit_scheme = 0
FEATURE [Drawing::FeatureViewPython] dia011  # drawing view (typed FeaturePython)
  Rotation = 0
  ViewResult = <g>  <circle cx ="115.583300" cy ="256.117000" r="0.500000" stroke="none" fill="rgb(0,0,255)" /> \n<line x1="118.771113" y1="260.669274" x2="113.346222" y2="252.922398" style="stroke:rgb(0,0,255);stroke-width:0.30" />\n<polygon points="117.820378,259.311602 118.722079,262.342598 120.114817,262.588117 120.360336,261.195378" style="fill:rgb(0,0,255);stroke:rgb(0,0,255);stroke-width:0" />\n<polygon points="113.346222,252.922398 112.444521,249.891402 111.051783,249.645883 110.806264,251.038622" style="fill:rgb(0,0,255);stroke:rgb(0,0,255);stroke-width:0" />\n<line x1="118.771113" y1="260.669274" x2="157.185532" y2="260.669274" style="stroke:rgb(0,0,255);stroke-width:0.30" />\n<text x="137.978322" y="258.669274" font-family="Verdana" font-size="3.6" fill="rgb(255,0,0)" text-anchor="middle" transform="rotate(0.000000 137.978322,258.669274)" >Ø5.2</text> </g>
  Visible = false
  X = 0
  Y = 0
  arrowL1 = 3
  arrowL2 = 1
  arrowW = 2
  arrow_scheme = 0
  autoPlaceOffset = 2
  autoPlaceText = true
  centerPointDia = 1
  click1_x = 118.771
  click1_y = 260.669
  click2_x = 157.186
  click2_y = 261.061
  click3_x = 157.186
  click3_y = 261.061
  comma_decimal_place = false
  lineColor = rgb(0,0,255)
  strokeWidth = 0.3
  textFormat_circular = Ø%(value)3.3f
  textRenderer_color = rgb(255,0,0)
  textRenderer_family = Verdana
  textRenderer_size = 3.6
  unit_custom_scale = 1
  unit_scheme = 0
FEATURE [Drawing::FeatureViewPython] dia012  # drawing view (typed FeaturePython)
  Rotation = 0
  ViewResult = <g>  <circle cx ="89.483300" cy ="154.583000" r="0.500000" stroke="none" fill="rgb(0,0,255)" /> \n<line x1="101.915806" y1="161.105371" x2="85.166314" y2="152.318213" style="stroke:rgb(0,0,255);stroke-width:0.30" />\n<polygon points="93.800286,156.847787 91.608251,154.568536 90.258144,154.989500 90.679107,156.339607" style="fill:rgb(0,0,255);stroke:rgb(0,0,255);stroke-width:0" />\n<polygon points="85.166314,152.318213 87.358349,154.597464 88.708456,154.176500 88.287493,152.826393" style="fill:rgb(0,0,255);stroke:rgb(0,0,255);stroke-width:0" />\n<line x1="101.915806" y1="161.105371" x2="112.499371" y2="161.105371" style="stroke:rgb(0,0,255);stroke-width:0.30" />\n<text x="107.207588" y="159.105371" font-family="Verdana" font-size="3.6" fill="rgb(255,0,0)" text-anchor="middle" transform="rotate(0.000000 107.207588,159.105371)" >Ø6.5</text> </g>
  Visible = false
  X = 0
  Y = 0
  arrowL1 = 3
  arrowL2 = 1
  arrowW = 2
  arrow_scheme = 0
  autoPlaceOffset = 2
  autoPlaceText = true
  centerPointDia = 1
  click1_x = 101.916
  click1_y = 161.105
  click2_x = 112.499
  click2_y = 161.105
  click3_x = 112.499
  click3_y = 161.105
  comma_decimal_place = false
  lineColor = rgb(0,0,255)
  strokeWidth = 0.3
  textFormat_circular = Ø%(value)3.3f
  textRenderer_color = rgb(255,0,0)
  textRenderer_family = Verdana
  textRenderer_size = 3.6
  unit_custom_scale = 1
  unit_scheme = 0
FEATURE [Drawing::FeatureViewPython] dia013  # drawing view (typed FeaturePython)
  Rotation = 0
  ViewResult = <g>  <circle cx ="89.483300" cy ="136.583000" r="0.500000" stroke="none" fill="rgb(0,0,255)" /> \n<line x1="96.428032" y1="144.250064" x2="87.217557" y2="134.081594" style="stroke:rgb(0,0,255);stroke-width:0.30" />\n<polygon points="91.749043,139.084406 93.021879,141.979210 94.434368,142.049036 94.504194,140.636547" style="fill:rgb(0,0,255);stroke:rgb(0,0,255);stroke-width:0" />\n<polygon points="87.217557,134.081594 85.944721,131.186790 84.532232,131.116964 84.462406,132.529453" style="fill:rgb(0,0,255);stroke:rgb(0,0,255);stroke-width:0" />\n<line x1="96.428032" y1="144.250064" x2="116.419209" y2="144.250064" style="stroke:rgb(0,0,255);stroke-width:0.30" />\n<text x="106.423621" y="142.250064" font-family="Verdana" font-size="3.6" fill="rgb(255,0,0)" text-anchor="middle" transform="rotate(0.000000 106.423621,142.250064)" >Ø4.5</text> </g>
  Visible = false
  X = 0
  Y = 0
  arrowL1 = 3
  arrowL2 = 1
  arrowW = 2
  arrow_scheme = 0
  autoPlaceOffset = 2
  autoPlaceText = true
  centerPointDia = 1
  click1_x = 96.428
  click1_y = 144.25
  click2_x = 116.419
  click2_y = 144.642
  click3_x = 116.419
  click3_y = 144.642
  comma_decimal_place = false
  lineColor = rgb(0,0,255)
  strokeWidth = 0.3
  textFormat_circular = Ø%(value)3.3f
  textRenderer_color = rgb(255,0,0)
  textRenderer_family = Verdana
  textRenderer_size = 3.6
  unit_custom_scale = 1
  unit_scheme = 0
FEATURE [Drawing::FeatureViewPython] dimStack020  # drawing view (typed FeaturePython)
  Rotation = 0
  ViewResult = <g> <line x1="91.483301" y1="46.583000" x2="112.200854" y2="46.583000" style="stroke:rgb(0,0,255);stroke-width:0.30" />\n<line x1="91.483301" y1="64.583000" x2="112.200854" y2="64.583000" style="stroke:rgb(0,0,255);stroke-width:0.30" />\n<line x1="111.200854" y1="46.583000" x2="111.200854" y2="64.583000" style="stroke:rgb(0,0,255);stroke-width:0.30" />\n<polygon points="111.200854,46.583000 110.200854,49.583000 111.200854,50.583000 112.200854,49.583000" style="fill:rgb(0,0,255);stroke:rgb(0,0,255);stroke-width:0" />\n<polygon points="111.200854,64.583000 112.200854,61.583000 111.200854,60.583000 110.200854,61.583000" style="fill:rgb(0,0,255);stroke:rgb(0,0,255);stroke-width:0" />\n<text x="109.200854" y="55.583000" font-family="Verdana" font-size="3.6" fill="rgb(255,0,0)" text-anchor="middle" transform="rotate(-90.000000 109.200854,55.583000)" >12</text> </g> 
  Visible = false
  X = 0
  Y = 0
  arrowL1 = 3
  arrowL2 = 1
  arrowW = 2
  arrow_scheme = 0
  autoPlaceOffset = 2
  click1_x = 111.201
  click1_y = 55.704
  comma_decimal_place = false
  dimension_line_overshoot = 1
  gap_datum_points = 2
  lineColor = rgb(0,0,255)
  stack_offset = 7
  stack_offset0 = 0
  strokeWidth = 0.3
  textFormat_linear = %(value)3.3f
  textRenderer_color = rgb(255,0,0)
  textRenderer_family = Verdana
  textRenderer_size = 3.6
  unit_custom_scale = 1
  unit_scheme = 0
FEATURE [Drawing::FeatureViewPython] dimStack021  # drawing view (typed FeaturePython)
  Rotation = 0
  ViewResult = <g> <line x1="91.483301" y1="46.583000" x2="112.200854" y2="46.583000" style="stroke:rgb(0,0,255);stroke-width:0.30" />\n<line x1="101.833301" y1="33.083000" x2="112.200854" y2="33.083000" style="stroke:rgb(0,0,255);stroke-width:0.30" />\n<line x1="111.200854" y1="46.583000" x2="111.200854" y2="33.083000" style="stroke:rgb(0,0,255);stroke-width:0.30" />\n<polygon points="111.200854,46.583000 112.200854,43.583000 111.200854,42.583000 110.200854,43.583000" style="fill:rgb(0,0,255);stroke:rgb(0,0,255);stroke-width:0" />\n<polygon points="111.200854,33.083000 110.200854,36.083000 111.200854,37.083000 112.200854,36.083000" style="fill:rgb(0,0,255);stroke:rgb(0,0,255);stroke-width:0" />\n<text x="109.200854" y="39.833000" font-family="Verdana" font-size="3.6" fill="rgb(255,0,0)" text-anchor="middle" transform="rotate(-90.000000 109.200854,39.833000)" >9</text> </g> 
  Visible = false
  X = 0
  Y = 0
  arrowL1 = 3
  arrowL2 = 1
  arrowW = 2
  arrow_scheme = 0
  autoPlaceOffset = 2
  click1_x = 111.201
  click1_y = 35.6174
  comma_decimal_place = false
  dimension_line_overshoot = 1
  gap_datum_points = 2
  lineColor = rgb(0,0,255)
  stack_offset = 7
  stack_offset0 = 0
  strokeWidth = 0.3
  textFormat_linear = %(value)3.3f
  textRenderer_color = rgb(255,0,0)
  textRenderer_family = Verdana
  textRenderer_size = 3.6
  unit_custom_scale = 1
  unit_scheme = 0
FEATURE [Drawing::FeatureViewPython] dimStack022  # drawing view (typed FeaturePython)
  Rotation = 0
  ViewResult = <g> <line x1="91.483301" y1="154.583000" x2="122.933914" y2="154.583000" style="stroke:rgb(0,0,255);stroke-width:0.30" />\n<line x1="101.833301" y1="166.583000" x2="122.933914" y2="166.583000" style="stroke:rgb(0,0,255);stroke-width:0.30" />\n<line x1="121.933914" y1="154.583000" x2="121.933914" y2="166.583000" style="stroke:rgb(0,0,255);stroke-width:0.30" />\n<polygon points="121.933914,154.583000 120.933914,157.583000 121.933914,158.583000 122.933914,157.583000" style="fill:rgb(0,0,255);stroke:rgb(0,0,255);stroke-width:0" />\n<polygon points="121.933914,166.583000 122.933914,163.583000 121.933914,162.583000 120.933914,163.583000" style="fill:rgb(0,0,255);stroke:rgb(0,0,255);stroke-width:0" />\n<text x="119.933914" y="160.583000" font-family="Verdana" font-size="3.6" fill="rgb(255,0,0)" text-anchor="middle" transform="rotate(-90.000000 119.933914,160.583000)" >8</text> </g> 
  Visible = false
  X = 0
  Y = 0
  arrowL1 = 3
  arrowL2 = 1
  arrowW = 2
  arrow_scheme = 0
  autoPlaceOffset = 2
  click1_x = 121.934
  click1_y = 163.777
  comma_decimal_place = false
  dimension_line_overshoot = 1
  gap_datum_points = 2
  lineColor = rgb(0,0,255)
  stack_offset = 7
  stack_offset0 = 0
  strokeWidth = 0.3
  textFormat_linear = %(value)3.3f
  textRenderer_color = rgb(255,0,0)
  textRenderer_family = Verdana
  textRenderer_size = 3.6
  unit_custom_scale = 1
  unit_scheme = 0
FEATURE [Drawing::FeatureViewPython] dimStack023  # drawing view (typed FeaturePython)
  Rotation = 0
  ViewResult = <g> <line x1="101.833301" y1="166.583000" x2="134.526245" y2="166.583000" style="stroke:rgb(0,0,255);stroke-width:0.30" />\n<line x1="101.833301" y1="168.083000" x2="134.526245" y2="168.083000" style="stroke:rgb(0,0,255);stroke-width:0.30" />\n<line x1="133.526245" y1="166.583000" x2="133.526245" y2="168.083000" style="stroke:rgb(0,0,255);stroke-width:0.30" />\n<polygon points="133.526245,166.583000 134.526245,163.583000 133.526245,162.583000 132.526245,163.583000" style="fill:rgb(0,0,255);stroke:rgb(0,0,255);stroke-width:0" />\n<polygon points="133.526245,168.083000 132.526245,171.083000 133.526245,172.083000 134.526245,171.083000" style="fill:rgb(0,0,255);stroke:rgb(0,0,255);stroke-width:0" />\n<text x="131.526245" y="167.333000" font-family="Verdana" font-size="3.6" fill="rgb(255,0,0)" text-anchor="middle" transform="rotate(-90.000000 131.526245,167.333000)" >1</text> </g> 
  Visible = false
  X = 0
  Y = 0
  arrowL1 = 3
  arrowL2 = 1
  arrowW = 2
  arrow_scheme = 0
  autoPlaceOffset = 2
  click1_x = 133.526
  click1_y = 165.708
  comma_decimal_place = false
  dimension_line_overshoot = 1
  gap_datum_points = 2
  lineColor = rgb(0,0,255)
  stack_offset = 7
  stack_offset0 = 0
  strokeWidth = 0.3
  textFormat_linear = %(value)3.3f
  textRenderer_color = rgb(255,0,0)
  textRenderer_family = Verdana
  textRenderer_size = 3.6
  unit_custom_scale = 1
  unit_scheme = 0
FEATURE [Drawing::FeatureViewPython] dimStack024  # drawing view (typed FeaturePython)
  Rotation = 0
  ViewResult = <g> <line x1="133.333300" y1="174.083000" x2="144.923962" y2="174.083000" style="stroke:rgb(0,0,255);stroke-width:0.30" />\n<line x1="133.333300" y1="168.083000" x2="144.923962" y2="168.083000" style="stroke:rgb(0,0,255);stroke-width:0.30" />\n<line x1="143.923962" y1="174.083000" x2="143.923962" y2="168.083000" style="stroke:rgb(0,0,255);stroke-width:0.30" />\n<polygon points="143.923962,174.083000 142.923962,177.083000 143.923962,178.083000 144.923962,177.083000" style="fill:rgb(0,0,255);stroke:rgb(0,0,255);stroke-width:0" />\n<polygon points="143.923962,168.083000 144.923962,165.083000 143.923962,164.083000 142.923962,165.083000" style="fill:rgb(0,0,255);stroke:rgb(0,0,255);stroke-width:0" />\n<text x="141.923962" y="171.083000" font-family="Verdana" font-size="3.6" fill="rgb(255,0,0)" text-anchor="middle" transform="rotate(-90.000000 141.923962,171.083000)" >4</text> </g> 
  Visible = false
  X = 0
  Y = 0
  arrowL1 = 3
  arrowL2 = 1
  arrowW = 2
  arrow_scheme = 0
  autoPlaceOffset = 2
  click1_x = 143.924
  click1_y = 168.61
  comma_decimal_place = false
  dimension_line_overshoot = 1
  gap_datum_points = 2
  lineColor = rgb(0,0,255)
  stack_offset = 7
  stack_offset0 = 0
  strokeWidth = 0.3
  textFormat_linear = %(value)3.3f
  textRenderer_color = rgb(255,0,0)
  textRenderer_family = Verdana
  textRenderer_size = 3.6
  unit_custom_scale = 1
  unit_scheme = 0
FEATURE [Drawing::FeatureViewPython] dimStack025  # drawing view (typed FeaturePython)
  Rotation = 0
  ViewResult = <g> <line x1="91.483301" y1="64.583000" x2="112.215845" y2="64.583000" style="stroke:rgb(0,0,255);stroke-width:0.30" />\n<line x1="91.483301" y1="82.583000" x2="112.215845" y2="82.583000" style="stroke:rgb(0,0,255);stroke-width:0.30" />\n<line x1="111.215845" y1="64.583000" x2="111.215845" y2="82.583000" style="stroke:rgb(0,0,255);stroke-width:0.30" />\n<polygon points="111.215845,64.583000 110.215845,67.583000 111.215845,68.583000 112.215845,67.583000" style="fill:rgb(0,0,255);stroke:rgb(0,0,255);stroke-width:0" />\n<polygon points="111.215845,82.583000 112.215845,79.583000 111.215845,78.583000 110.215845,79.583000" style="fill:rgb(0,0,255);stroke:rgb(0,0,255);stroke-width:0" />\n<text x="109.215845" y="73.583000" font-family="Verdana" font-size="3.6" fill="rgb(255,0,0)" text-anchor="middle" transform="rotate(-90.000000 109.215845,73.583000)" >12</text> </g> 
  Visible = false
  X = 0
  Y = 0
  arrowL1 = 3
  arrowL2 = 1
  arrowW = 2
  arrow_scheme = 0
  autoPlaceOffset = 2
  click1_x = 111.216
  click1_y = 79.7099
  comma_decimal_place = false
  dimension_line_overshoot = 1
  gap_datum_points = 2
  lineColor = rgb(0,0,255)
  stack_offset = 7
  stack_offset0 = 0
  strokeWidth = 0.3
  textFormat_linear = %(value)3.3f
  textRenderer_color = rgb(255,0,0)
  textRenderer_family = Verdana
  textRenderer_size = 3.6
  unit_custom_scale = 1
  unit_scheme = 0
FEATURE [Drawing::FeatureViewPython] dimStack026  # drawing view (typed FeaturePython)
  Rotation = 0
  ViewResult = <g> <line x1="91.483301" y1="100.583000" x2="112.215845" y2="100.583000" style="stroke:rgb(0,0,255);stroke-width:0.30" />\n<line x1="91.483301" y1="82.583000" x2="112.215845" y2="82.583000" style="stroke:rgb(0,0,255);stroke-width:0.30" />\n<line x1="111.215845" y1="100.583000" x2="111.215845" y2="82.583000" style="stroke:rgb(0,0,255);stroke-width:0.30" />\n<polygon points="111.215845,100.583000 112.215845,97.583000 111.215845,96.583000 110.215845,97.583000" style="fill:rgb(0,0,255);stroke:rgb(0,0,255);stroke-width:0" />\n<polygon points="111.215845,82.583000 110.215845,85.583000 111.215845,86.583000 112.215845,85.583000" style="fill:rgb(0,0,255);stroke:rgb(0,0,255);stroke-width:0" />\n<text x="109.215845" y="91.583000" font-family="Verdana" font-size="3.6" fill="rgb(255,0,0)" text-anchor="middle" transform="rotate(-90.000000 109.215845,91.583000)" >12</text> </g> 
  Visible = false
  X = 0
  Y = 0
  arrowL1 = 3
  arrowL2 = 1
  arrowW = 2
  arrow_scheme = 0
  autoPlaceOffset = 2
  click1_x = 111.216
  click1_y = 86.1687
  comma_decimal_place = false
  dimension_line_overshoot = 1
  gap_datum_points = 2
  lineColor = rgb(0,0,255)
  stack_offset = 7
  stack_offset0 = 0
  strokeWidth = 0.3
  textFormat_linear = %(value)3.3f
  textRenderer_color = rgb(255,0,0)
  textRenderer_family = Verdana
  textRenderer_size = 3.6
  unit_custom_scale = 1
  unit_scheme = 0
FEATURE [Drawing::FeatureViewPython] dimStack027  # drawing view (typed FeaturePython)
  Rotation = 0
  ViewResult = <g> <line x1="91.483301" y1="136.583000" x2="112.215845" y2="136.583000" style="stroke:rgb(0,0,255);stroke-width:0.30" />\n<line x1="91.483301" y1="118.583000" x2="112.215845" y2="118.583000" style="stroke:rgb(0,0,255);stroke-width:0.30" />\n<line x1="111.215845" y1="136.583000" x2="111.215845" y2="118.583000" style="stroke:rgb(0,0,255);stroke-width:0.30" />\n<polygon points="111.215845,136.583000 112.215845,133.583000 111.215845,132.583000 110.215845,133.583000" style="fill:rgb(0,0,255);stroke:rgb(0,0,255);stroke-width:0" />\n<polygon points="111.215845,118.583000 110.215845,121.583000 111.215845,122.583000 112.215845,121.583000" style="fill:rgb(0,0,255);stroke:rgb(0,0,255);stroke-width:0" />\n<text x="109.215845" y="127.583000" font-family="Verdana" font-size="3.6" fill="rgb(255,0,0)" text-anchor="middle" transform="rotate(-90.000000 109.215845,127.583000)" >12</text> </g> 
  Visible = false
  X = 0
  Y = 0
  arrowL1 = 3
  arrowL2 = 1
  arrowW = 2
  arrow_scheme = 0
  autoPlaceOffset = 2
  click1_x = 111.216
  click1_y = 124.921
  comma_decimal_place = false
  dimension_line_overshoot = 1
  gap_datum_points = 2
  lineColor = rgb(0,0,255)
  stack_offset = 7
  stack_offset0 = 0
  strokeWidth = 0.3
  textFormat_linear = %(value)3.3f
  textRenderer_color = rgb(255,0,0)
  textRenderer_family = Verdana
  textRenderer_size = 3.6
  unit_custom_scale = 1
  unit_scheme = 0
FEATURE [Drawing::FeatureViewPython] dimStack028  # drawing view (typed FeaturePython)
  Rotation = 0
  ViewResult = <g> <line x1="91.483301" y1="100.583000" x2="112.373375" y2="100.583000" style="stroke:rgb(0,0,255);stroke-width:0.30" />\n<line x1="91.483301" y1="118.583000" x2="112.373375" y2="118.583000" style="stroke:rgb(0,0,255);stroke-width:0.30" />\n<line x1="111.373375" y1="100.583000" x2="111.373375" y2="118.583000" style="stroke:rgb(0,0,255);stroke-width:0.30" />\n<polygon points="111.373375,100.583000 110.373375,103.583000 111.373375,104.583000 112.373375,103.583000" style="fill:rgb(0,0,255);stroke:rgb(0,0,255);stroke-width:0" />\n<polygon points="111.373375,118.583000 112.373375,115.583000 111.373375,114.583000 110.373375,115.583000" style="fill:rgb(0,0,255);stroke:rgb(0,0,255);stroke-width:0" />\n<text x="109.373375" y="109.583000" font-family="Verdana" font-size="3.6" fill="rgb(255,0,0)" text-anchor="middle" transform="rotate(-90.000000 109.373375,109.583000)" >12</text> </g> 
  Visible = false
  X = 0
  Y = 0
  arrowL1 = 3
  arrowL2 = 1
  arrowW = 2
  arrow_scheme = 0
  autoPlaceOffset = 2
  click1_x = 111.373
  click1_y = 113.894
  comma_decimal_place = false
  dimension_line_overshoot = 1
  gap_datum_points = 2
  lineColor = rgb(0,0,255)
  stack_offset = 7
  stack_offset0 = 0
  strokeWidth = 0.3
  textFormat_linear = %(value)3.3f
  textRenderer_color = rgb(255,0,0)
  textRenderer_family = Verdana
  textRenderer_size = 3.6
  unit_custom_scale = 1
  unit_scheme = 0
FEATURE [Drawing::FeatureViewPython] dimStack029  # drawing view (typed FeaturePython)
  Rotation = 0
  ViewResult = <g> <line x1="91.483301" y1="154.583000" x2="131.430341" y2="154.583000" style="stroke:rgb(0,0,255);stroke-width:0.30" />\n<line x1="91.483301" y1="136.583000" x2="131.430341" y2="136.583000" style="stroke:rgb(0,0,255);stroke-width:0.30" />\n<line x1="130.430341" y1="154.583000" x2="130.430341" y2="136.583000" style="stroke:rgb(0,0,255);stroke-width:0.30" />\n<polygon points="130.430341,154.583000 131.430341,151.583000 130.430341,150.583000 129.430341,151.583000" style="fill:rgb(0,0,255);stroke:rgb(0,0,255);stroke-width:0" />\n<polygon points="130.430341,136.583000 129.430341,139.583000 130.430341,140.583000 131.430341,139.583000" style="fill:rgb(0,0,255);stroke:rgb(0,0,255);stroke-width:0" />\n<text x="128.430341" y="145.583000" font-family="Verdana" font-size="3.6" fill="rgb(255,0,0)" text-anchor="middle" transform="rotate(-90.000000 128.430341,145.583000)" >12</text> </g> 
  Visible = false
  X = 0
  Y = 0
  arrowL1 = 3
  arrowL2 = 1
  arrowW = 2
  arrow_scheme = 0
  autoPlaceOffset = 2
  click1_x = 130.43
  click1_y = 140.928
  comma_decimal_place = false
  dimension_line_overshoot = 1
  gap_datum_points = 2
  lineColor = rgb(0,0,255)
  stack_offset = 7
  stack_offset0 = 0
  strokeWidth = 0.3
  textFormat_linear = %(value)3.3f
  textRenderer_color = rgb(255,0,0)
  textRenderer_family = Verdana
  textRenderer_size = 3.6
  unit_custom_scale = 1
  unit_scheme = 0
FEATURE [Drawing::FeaturePage] Page005
  EditableTexts = AUTHOR NAME | CREATION DATE | SUPERVISOR NAME | CHECK DATE | SCALE | WEIGHT | NUMBER | SHEET | TITLE | SUBTITLE
  Group = -> [Ortho018,Ortho019,Ortho020,dim019,dim020,dim021,dim022,dim023,dim024,dim025,dim026,dim027,dim028,dimStack018,dimStack019,dia010,dia011,dia012,dia013,dimStack020,dimStack021,dimStack022,dimStack023,dimStack024,dimStack025,dimStack026,dimStack027,dimStack028,dimStack029]
  Template = <path>
FEATURE [Part::Feature] Unfold
  shape: bbox 103.2 x 137.3 x 4 mm, 12 faces (baked)
FEATURE [Part::Feature] Cut001002003001  label="Cut001002005"
  shape: bbox 93.5 x 92.48 x 52 mm, 44 faces (baked)
FEATURE [Drawing::FeatureViewPart] Ortho021  label="Ortho_0_012"
  Direction = (1,0,0)
  HiddenWidth = 0.15
  LineWidth = 0.35
  Rotation = -90
  ShowHiddenLines = false
  ShowSmoothLines = false
  Source = -> Cut001002003001
  Tolerance = 0.05
  ViewResult = <blob: 2479 chars omitted>
  Visible = false
  X = 168.66
  Y = 215.167
FEATURE [Drawing::FeatureViewPart] Ortho022  label="Ortho_1_003"
  Direction = (0.57735,0.57735,0.57735)
  HiddenWidth = 0.15
  LineWidth = 0.35
  Rotation = 120
  ShowHiddenLines = false
  ShowSmoothLines = false
  Source = -> Cut001002003001
  Tolerance = 0.05
  ViewResult = <blob: 4086 chars omitted>
  Visible = false
  X = 300.742
  Y = 96.5499
FEATURE [Drawing::FeatureViewPart] Ortho023  label="Ortho_0_013"
  Direction = (0,0,1)
  HiddenWidth = 0.15
  LineWidth = 0.35
  Rotation = 90
  ShowHiddenLines = false
  ShowSmoothLines = false
  Source = -> Cut001002003001
  Tolerance = 0.05
  ViewResult = <blob: 2943 chars omitted>
  Visible = false
  X = 168.66
  Y = 85.0333
FEATURE [Drawing::FeatureViewPart] Ortho024  label="Ortho_-1_004"
  Direction = (0,-1,0)
  HiddenWidth = 0.15
  LineWidth = 0.35
  Rotation = 90
  ShowHiddenLines = false
  ShowSmoothLines = false
  Source = -> Cut001002003001
  Tolerance = 0.05
  ViewResult = <blob: 2621 chars omitted>
  Visible = false
  X = 91.33
  Y = 215.167
FEATURE [Drawing::FeatureViewPython] dimStack030  # drawing view (typed FeaturePython)
  Rotation = 0
  ViewResult = <g> <line x1="51.230000" y1="195.167001" x2="51.230000" y2="221.159422" style="stroke:rgb(0,0,255);stroke-width:0.50" />\n<line x1="60.130000" y1="205.167001" x2="60.130000" y2="221.159422" style="stroke:rgb(0,0,255);stroke-width:0.50" />\n<line x1="51.230000" y1="220.159422" x2="60.130000" y2="220.159422" style="stroke:rgb(0,0,255);stroke-width:0.50" />\n<polygon points="51.230000,220.159422 48.230000,219.159422 47.230000,220.159422 48.230000,221.159422" style="fill:rgb(0,0,255);stroke:rgb(0,0,255);stroke-width:0" />\n<polygon points="60.130000,220.159422 63.130000,221.159422 64.130000,220.159422 63.130000,219.159422" style="fill:rgb(0,0,255);stroke:rgb(0,0,255);stroke-width:0" />\n<text x="55.680000" y="218.159422" font-family="inherit" font-size="3.6" fill="rgb(0,0,255)" text-anchor="middle" transform="rotate(0.000000 55.680000,218.159422)" >8.9</text> </g> 
  Visible = false
  X = 0
  Y = 0
  arrowL1 = 3
  arrowL2 = 1
  arrowW = 2
  arrow_scheme = 0
  autoPlaceOffset = 2
  click1_x = 57.5441
  click1_y = 220.159
  comma_decimal_place = false
  dimension_line_overshoot = 1
  gap_datum_points = 2
  lineColor = rgb(0,0,255)
  stack_offset = 7
  stack_offset0 = 0
  strokeWidth = 0.5
  textFormat_linear = %(value)3.3f
  textRenderer_color = rgb(0,0,255)
  textRenderer_family = inherit
  textRenderer_size = 3.6
  unit_custom_scale = 1
  unit_scheme = 0
FEATURE [Drawing::FeatureViewPython] dimStack031  # drawing view (typed FeaturePython)
  Rotation = 0
  ViewResult = <g> <line x1="40.130000" y1="205.167001" x2="40.130000" y2="231.602609" style="stroke:rgb(0,0,255);stroke-width:0.50" />\n<line x1="60.130000" y1="205.167001" x2="60.130000" y2="231.602609" style="stroke:rgb(0,0,255);stroke-width:0.50" />\n<line x1="40.130000" y1="230.602609" x2="60.130000" y2="230.602609" style="stroke:rgb(0,0,255);stroke-width:0.50" />\n<polygon points="40.130000,230.602609 43.130000,231.602609 44.130000,230.602609 43.130000,229.602609" style="fill:rgb(0,0,255);stroke:rgb(0,0,255);stroke-width:0" />\n<polygon points="60.130000,230.602609 57.130000,229.602609 56.130000,230.602609 57.130000,231.602609" style="fill:rgb(0,0,255);stroke:rgb(0,0,255);stroke-width:0" />\n<text x="50.130000" y="228.602609" font-family="inherit" font-size="3.6" fill="rgb(0,0,255)" text-anchor="middle" transform="rotate(0.000000 50.130000,228.602609)" >20</text> </g> 
  Visible = false
  X = 0
  Y = 0
  arrowL1 = 3
  arrowL2 = 1
  arrowW = 2
  arrow_scheme = 0
  autoPlaceOffset = 2
  click1_x = 59.036
  click1_y = 230.603
  comma_decimal_place = false
  dimension_line_overshoot = 1
  gap_datum_points = 2
  lineColor = rgb(0,0,255)
  stack_offset = 7
  stack_offset0 = 0
  strokeWidth = 0.5
  textFormat_linear = %(value)3.3f
  textRenderer_color = rgb(0,0,255)
  textRenderer_family = inherit
  textRenderer_size = 3.6
  unit_custom_scale = 1
  unit_scheme = 0
FEATURE [Drawing::FeatureViewPython] dimStack032  # drawing view (typed FeaturePython)
  Rotation = 0
  ViewResult = <g> <line x1="53.230001" y1="193.167000" x2="75.807316" y2="193.167000" style="stroke:rgb(0,0,255);stroke-width:0.50" />\n<line x1="62.130001" y1="203.167000" x2="75.807316" y2="203.167000" style="stroke:rgb(0,0,255);stroke-width:0.50" />\n<line x1="74.807316" y1="193.167000" x2="74.807316" y2="203.167000" style="stroke:rgb(0,0,255);stroke-width:0.50" />\n<polygon points="74.807316,193.167000 75.807316,190.167000 74.807316,189.167000 73.807316,190.167000" style="fill:rgb(0,0,255);stroke:rgb(0,0,255);stroke-width:0" />\n<polygon points="74.807316,203.167000 73.807316,206.167000 74.807316,207.167000 75.807316,206.167000" style="fill:rgb(0,0,255);stroke:rgb(0,0,255);stroke-width:0" />\n<text x="72.807316" y="198.167000" font-family="inherit" font-size="3.6" fill="rgb(0,0,255)" text-anchor="middle" transform="rotate(-90.000000 72.807316,198.167000)" >10</text> </g> 
  Visible = false
  X = 0
  Y = 0
  arrowL1 = 3
  arrowL2 = 1
  arrowW = 2
  arrow_scheme = 0
  autoPlaceOffset = 2
  click1_x = 74.8073
  click1_y = 202.044
  comma_decimal_place = false
  dimension_line_overshoot = 1
  gap_datum_points = 2
  lineColor = rgb(0,0,255)
  stack_offset = 7
  stack_offset0 = 0
  strokeWidth = 0.5
  textFormat_linear = %(value)3.3f
  textRenderer_color = rgb(0,0,255)
  textRenderer_family = inherit
  textRenderer_size = 3.6
  unit_custom_scale = 1
  unit_scheme = 0
FEATURE [Drawing::FeatureViewPython] dimStack033  # drawing view (typed FeaturePython)
  Rotation = 0
  ViewResult = <g> <line x1="186.260001" y1="117.033300" x2="205.019877" y2="117.033300" style="stroke:rgb(0,0,255);stroke-width:0.50" />\n<line x1="191.040001" y1="127.333300" x2="205.019877" y2="127.333300" style="stroke:rgb(0,0,255);stroke-width:0.50" />\n<line x1="204.019877" y1="117.033300" x2="204.019877" y2="127.333300" style="stroke:rgb(0,0,255);stroke-width:0.50" />\n<polygon points="204.019877,117.033300 203.019877,120.033300 204.019877,121.033300 205.019877,120.033300" style="fill:rgb(0,0,255);stroke:rgb(0,0,255);stroke-width:0" />\n<polygon points="204.019877,127.333300 205.019877,124.333300 204.019877,123.333300 203.019877,124.333300" style="fill:rgb(0,0,255);stroke:rgb(0,0,255);stroke-width:0" />\n<text x="202.019877" y="122.183300" font-family="inherit" font-size="3.6" fill="rgb(0,0,255)" text-anchor="middle" transform="rotate(-90.000000 202.019877,122.183300)" >10.3</text> </g> 
  Visible = false
  X = 0
  Y = 0
  arrowL1 = 3
  arrowL2 = 1
  arrowW = 2
  arrow_scheme = 0
  autoPlaceOffset = 2
  click1_x = 204.02
  click1_y = 122.909
  comma_decimal_place = false
  dimension_line_overshoot = 1
  gap_datum_points = 2
  lineColor = rgb(0,0,255)
  stack_offset = 7
  stack_offset0 = 0
  strokeWidth = 0.5
  textFormat_linear = %(value)3.3f
  textRenderer_color = rgb(0,0,255)
  textRenderer_family = inherit
  textRenderer_size = 3.6
  unit_custom_scale = 1
  unit_scheme = 0
FEATURE [Drawing::FeatureViewPython] dimStack034  # drawing view (typed FeaturePython)
  Rotation = 0
  ViewResult = <g> <line x1="166.659999" y1="117.033300" x2="151.543829" y2="117.033300" style="stroke:rgb(0,0,255);stroke-width:0.50" />\n<line x1="161.759999" y1="127.333300" x2="151.543829" y2="127.333300" style="stroke:rgb(0,0,255);stroke-width:0.50" />\n<line x1="152.543829" y1="117.033300" x2="152.543829" y2="127.333300" style="stroke:rgb(0,0,255);stroke-width:0.50" />\n<polygon points="152.543829,117.033300 151.543829,120.033300 152.543829,121.033300 153.543829,120.033300" style="fill:rgb(0,0,255);stroke:rgb(0,0,255);stroke-width:0" />\n<polygon points="152.543829,127.333300 153.543829,124.333300 152.543829,123.333300 151.543829,124.333300" style="fill:rgb(0,0,255);stroke:rgb(0,0,255);stroke-width:0" />\n<text x="150.543829" y="122.183300" font-family="inherit" font-size="3.6" fill="rgb(0,0,255)" text-anchor="middle" transform="rotate(-90.000000 150.543829,122.183300)" >10.3</text> </g> 
  Visible = false
  X = 0
  Y = 0
  arrowL1 = 3
  arrowL2 = 1
  arrowW = 2
  arrow_scheme = 0
  autoPlaceOffset = 2
  click1_x = 152.544
  click1_y = 125.992
  comma_decimal_place = false
  dimension_line_overshoot = 1
  gap_datum_points = 2
  lineColor = rgb(0,0,255)
  stack_offset = 7
  stack_offset0 = 0
  strokeWidth = 0.5
  textFormat_linear = %(value)3.3f
  textRenderer_color = rgb(0,0,255)
  textRenderer_family = inherit
  textRenderer_size = 3.6
  unit_custom_scale = 1
  unit_scheme = 0
FEATURE [Drawing::FeatureViewPython] dimStack035  # drawing view (typed FeaturePython)
  Rotation = 0
  ViewResult = <g> <line x1="168.660000" y1="115.033299" x2="168.660000" y2="110.517162" style="stroke:rgb(0,0,255);stroke-width:0.50" />\n<line x1="184.260000" y1="115.033299" x2="184.260000" y2="110.517162" style="stroke:rgb(0,0,255);stroke-width:0.50" />\n<line x1="168.660000" y1="111.517162" x2="184.260000" y2="111.517162" style="stroke:rgb(0,0,255);stroke-width:0.50" />\n<polygon points="168.660000,111.517162 171.660000,112.517162 172.660000,111.517162 171.660000,110.517162" style="fill:rgb(0,0,255);stroke:rgb(0,0,255);stroke-width:0" />\n<polygon points="184.260000,111.517162 181.260000,110.517162 180.260000,111.517162 181.260000,112.517162" style="fill:rgb(0,0,255);stroke:rgb(0,0,255);stroke-width:0" />\n<text x="176.460000" y="109.517162" font-family="inherit" font-size="3.6" fill="rgb(0,0,255)" text-anchor="middle" transform="rotate(0.000000 176.460000,109.517162)" >15.6</text> </g> 
  Visible = false
  X = 0
  Y = 0
  arrowL1 = 3
  arrowL2 = 1
  arrowW = 2
  arrow_scheme = 0
  autoPlaceOffset = 2
  click1_x = 173.614
  click1_y = 111.517
  comma_decimal_place = false
  dimension_line_overshoot = 1
  gap_datum_points = 2
  lineColor = rgb(0,0,255)
  stack_offset = 7
  stack_offset0 = 0
  strokeWidth = 0.5
  textFormat_linear = %(value)3.3f
  textRenderer_color = rgb(0,0,255)
  textRenderer_family = inherit
  textRenderer_size = 3.6
  unit_custom_scale = 1
  unit_scheme = 0
FEATURE [Drawing::FeatureViewPython] dia014  # drawing view (typed FeaturePython)
  Rotation = 0
  ViewResult = <g>  <circle cx ="51.230000" cy ="193.167000" r="0.250000" stroke="none" fill="rgb(0,0,255)" /> \n<line x1="57.351683" y1="188.705539" x2="48.603513" y2="195.081175" style="stroke:rgb(0,0,255);stroke-width:0.50" />\n<polygon points="53.856487,191.252825 56.869914,190.294045 57.089087,188.896918 55.691960,188.677745" style="fill:rgb(0,0,255);stroke:rgb(0,0,255);stroke-width:0" />\n<polygon points="48.603513,195.081175 45.590086,196.039955 45.370913,197.437082 46.768040,197.656255" style="fill:rgb(0,0,255);stroke:rgb(0,0,255);stroke-width:0" />\n<line x1="57.351683" y1="188.705539" x2="69.315368" y2="188.705539" style="stroke:rgb(0,0,255);stroke-width:0.50" />\n<text x="63.333526" y="186.705539" font-family="inherit" font-size="3.2" fill="rgb(255,0,37)" text-anchor="middle" transform="rotate(0.000000 63.333526,186.705539)" >Ø6.5</text> </g>
  Visible = false
  X = 0
  Y = 0
  arrowL1 = 3
  arrowL2 = 1
  arrowW = 2
  arrow_scheme = 0
  autoPlaceOffset = 2
  autoPlaceText = true
  centerPointDia = 0.5
  click1_x = 57.3517
  click1_y = 188.706
  click2_x = 69.3154
  click2_y = 188.829
  click3_x = 69.3154
  click3_y = 188.829
  comma_decimal_place = false
  lineColor = rgb(0,0,255)
  strokeWidth = 0.5
  textFormat_circular = Ø%(value)3.3f
  textRenderer_color = rgb(255,0,37)
  textRenderer_family = inherit
  textRenderer_size = 3.2
  unit_custom_scale = 1
  unit_scheme = 0
FEATURE [Drawing::FeatureViewPython] dia015  # drawing view (typed FeaturePython)
  Rotation = 0
  ViewResult = <g>  <circle cx ="184.260000" cy ="117.033300" r="0.250000" stroke="none" fill="rgb(0,0,255)" /> \n<line x1="197.832473" y1="110.509910" x2="181.916620" y2="118.159608" style="stroke:rgb(0,0,255);stroke-width:0.50" />\n<polygon points="186.603380,115.906992 189.740476,115.508706 190.208581,114.174211 188.874085,113.706106" style="fill:rgb(0,0,255);stroke:rgb(0,0,255);stroke-width:0" />\n<polygon points="181.916620,118.159608 178.779524,118.557894 178.311419,119.892389 179.645915,120.360494" style="fill:rgb(0,0,255);stroke:rgb(0,0,255);stroke-width:0" />\n<line x1="197.832473" y1="110.509910" x2="207.576093" y2="110.509910" style="stroke:rgb(0,0,255);stroke-width:0.50" />\n<text x="202.704283" y="108.509910" font-family="inherit" font-size="3.2" fill="rgb(255,0,37)" text-anchor="middle" transform="rotate(0.000000 202.704283,108.509910)" >Ø5.2</text> </g>
  Visible = false
  X = 0
  Y = 0
  arrowL1 = 3
  arrowL2 = 1
  arrowW = 2
  arrow_scheme = 0
  autoPlaceOffset = 2
  autoPlaceText = true
  centerPointDia = 0.5
  click1_x = 197.832
  click1_y = 110.51
  click2_x = 207.576
  click2_y = 111.867
  click3_x = 207.576
  click3_y = 111.867
  comma_decimal_place = false
  lineColor = rgb(0,0,255)
  strokeWidth = 0.5
  textFormat_circular = Ø%(value)3.3f
  textRenderer_color = rgb(255,0,37)
  textRenderer_family = inherit
  textRenderer_size = 3.2
  unit_custom_scale = 1
  unit_scheme = 0
FEATURE [Drawing::FeatureViewPython] dia016  # drawing view (typed FeaturePython)
  Rotation = 0
  ViewResult = <g>  <circle cx ="168.660000" cy ="117.033300" r="0.250000" stroke="none" fill="rgb(0,0,255)" /> \n<line x1="157.007942" y1="111.249932" x2="170.988911" y2="118.189229" style="stroke:rgb(0,0,255);stroke-width:0.50" />\n<polygon points="166.331089,115.877371 164.088471,113.647872 162.748148,114.099019 163.199295,115.439342" style="fill:rgb(0,0,255);stroke:rgb(0,0,255);stroke-width:0" />\n<polygon points="170.988911,118.189229 173.231529,120.418728 174.571852,119.967581 174.120705,118.627258" style="fill:rgb(0,0,255);stroke:rgb(0,0,255);stroke-width:0" />\n<line x1="157.007942" y1="111.249932" x2="144.920920" y2="111.249932" style="stroke:rgb(0,0,255);stroke-width:0.50" />\n<text x="150.964431" y="109.249932" font-family="inherit" font-size="3.2" fill="rgb(255,0,37)" text-anchor="middle" transform="rotate(0.000000 150.964431,109.249932)" >Ø5.2</text> </g>
  Visible = false
  X = 0
  Y = 0
  arrowL1 = 3
  arrowL2 = 1
  arrowW = 2
  arrow_scheme = 0
  autoPlaceOffset = 2
  autoPlaceText = true
  centerPointDia = 0.5
  click1_x = 157.008
  click1_y = 111.25
  click2_x = 144.921
  click2_y = 111.99
  click3_x = 144.921
  click3_y = 111.99
  comma_decimal_place = false
  lineColor = rgb(0,0,255)
  strokeWidth = 0.5
  textFormat_circular = Ø%(value)3.3f
  textRenderer_color = rgb(255,0,37)
  textRenderer_family = inherit
  textRenderer_size = 3.2
  unit_custom_scale = 1
  unit_scheme = 0
FEATURE [Part::Feature] Unfold001  label="fu"
  shape: bbox 35 x 132.6 x 4 mm, 10 faces (baked)
FEATURE [Sketcher::SketchObject] Sketch001  label="Unfold_Sketch001"
  sketch-geometry (9):
    g0: LineSegment StartX=7.5 StartY=158.584 StartZ=0 EndX=21.5 EndY=158.584 EndZ=0
    g1: LineSegment StartX=42.5 StartY=55.5 StartZ=0 EndX=21.5 EndY=65.5 EndZ=0
    g2: LineSegment StartX=19.5 StartY=54.5 StartZ=0 EndX=19.5 EndY=26 EndZ=0
    g3: LineSegment StartX=19.5 StartY=26 StartZ=0 EndX=42.5 EndY=26 EndZ=0
    g4: LineSegment StartX=7.5 StartY=59.5 StartZ=0 EndX=19.5 EndY=54.5 EndZ=0
    g5: LineSegment StartX=7.5 StartY=59.5 StartZ=0 EndX=7.5 EndY=158.584 EndZ=0
    g6: LineSegment StartX=42.5 StartY=55.5 StartZ=0 EndX=42.5 EndY=26 EndZ=0
    g7: LineSegment StartX=21.5 StartY=158.584 StartZ=0 EndX=21.5 EndY=65.5 EndZ=0
    g8: LineSegment StartX=7.5 StartY=67.542 StartZ=0 EndX=21.5 EndY=67.542 EndZ=0
FEATURE [Part::Feature] Fusion002008006003002002003  label="开孔003-002"
  shape: bbox 120 x 91 x 94 mm, 255 faces, 8 solids (baked)
FEATURE [Part::Cut] Cut001002003002
  Base = -> Unfold001
  Tool = -> Fusion002008006003002002003
FEATURE [Part::Box] Box032  label="负极004"
  AttacherType = Attacher::AttachEngine3D
  Height = 4
  Length = 28
  Placement = pos=(-51.2,42.58,60) rot=(0,0,1;0rad)
  Width = 60
FEATURE [Part::Chamfer] Chamfer002
  Base = -> Box032
  Edges = 1 edges: [Edge7 r1=10.5 r2=8]
FEATURE [Drawing::FeatureViewPython] dimStack036  # drawing view (typed FeaturePython)
  Rotation = 0
  ViewResult = <g> <line x1="114.130000" y1="156.167000" x2="141.003499" y2="156.167000" style="stroke:rgb(0,0,255);stroke-width:0.50" />\n<line x1="114.130000" y1="166.167000" x2="141.003499" y2="166.167000" style="stroke:rgb(0,0,255);stroke-width:0.50" />\n<line x1="140.003499" y1="156.167000" x2="140.003499" y2="166.167000" style="stroke:rgb(0,0,255);stroke-width:0.50" />\n<polygon points="140.003499,156.167000 141.003499,153.167000 140.003499,152.167000 139.003499,153.167000" style="fill:rgb(0,0,255);stroke:rgb(0,0,255);stroke-width:0" />\n<polygon points="140.003499,166.167000 139.003499,169.167000 140.003499,170.167000 141.003499,169.167000" style="fill:rgb(0,0,255);stroke:rgb(0,0,255);stroke-width:0" />\n<text x="138.003499" y="161.167000" font-family="inherit" font-size="3.2" fill="rgb(255,0,37)" text-anchor="middle" transform="rotate(-90.000000 138.003499,161.167000)" >10</text> </g> 
  Visible = false
  X = 0
  Y = 0
  arrowL1 = 3
  arrowL2 = 1
  arrowW = 2
  arrow_scheme = 0
  autoPlaceOffset = 2
  click1_x = 140.003
  click1_y = 163.1
  comma_decimal_place = false
  dimension_line_overshoot = 1
  gap_datum_points = 2
  lineColor = rgb(0,0,255)
  stack_offset = 7
  stack_offset0 = 0
  strokeWidth = 0.5
  textFormat_linear = %(value)3.3f
  textRenderer_color = rgb(255,0,37)
  textRenderer_family = inherit
  textRenderer_size = 3.2
  unit_custom_scale = 1
  unit_scheme = 0
FEATURE [Drawing::FeatureViewPython] dimStack037  # drawing view (typed FeaturePython)
  Rotation = 0
  ViewResult = <g> <line x1="107.830000" y1="155.167000" x2="149.262644" y2="155.167000" style="stroke:rgb(0,0,255);stroke-width:0.50" />\n<line x1="135.630000" y1="167.167000" x2="149.262644" y2="167.167000" style="stroke:rgb(0,0,255);stroke-width:0.50" />\n<line x1="148.262644" y1="155.167000" x2="148.262644" y2="167.167000" style="stroke:rgb(0,0,255);stroke-width:0.50" />\n<polygon points="148.262644,155.167000 147.262644,158.167000 148.262644,159.167000 149.262644,158.167000" style="fill:rgb(0,0,255);stroke:rgb(0,0,255);stroke-width:0" />\n<polygon points="148.262644,167.167000 149.262644,164.167000 148.262644,163.167000 147.262644,164.167000" style="fill:rgb(0,0,255);stroke:rgb(0,0,255);stroke-width:0" />\n<text x="146.262644" y="161.167000" font-family="inherit" font-size="3.2" fill="rgb(255,0,37)" text-anchor="middle" transform="rotate(-90.000000 146.262644,161.167000)" >12</text> </g> 
  Visible = false
  X = 0
  Y = 0
  arrowL1 = 3
  arrowL2 = 1
  arrowW = 2
  arrow_scheme = 0
  autoPlaceOffset = 2
  click1_x = 148.263
  click1_y = 165.011
  comma_decimal_place = false
  dimension_line_overshoot = 1
  gap_datum_points = 2
  lineColor = rgb(0,0,255)
  stack_offset = 7
  stack_offset0 = 0
  strokeWidth = 0.5
  textFormat_linear = %(value)3.3f
  textRenderer_color = rgb(255,0,37)
  textRenderer_family = inherit
  textRenderer_size = 3.2
  unit_custom_scale = 1
  unit_scheme = 0
FEATURE [Drawing::FeaturePage] Page006
  EditableTexts = AUTHOR NAME | CREATION DATE | SUPERVISOR NAME | CHECK DATE | SCALE | WEIGHT | NUMBER | SHEET | TITLE | SUBTITLE
  Group = -> [Ortho021,Ortho022,Ortho023,Ortho024,dimStack030,dimStack031,dimStack032,dimStack033,dimStack034,dimStack035,dia014,dia015,dia016,dimStack036,dimStack037]
  Template = <path>
FEATURE [Part::Box] Box033  label="负极005"
  AttacherType = Attacher::AttachEngine3D
  Height = 4
  Length = 50
  Placement = pos=(-31,-4.9,62.1) rot=(0,1,0;0.349066rad)
  Width = 66
FEATURE [Part::Chamfer] Chamfer003  label="正007"
  Base = -> Box033
  Edges = 2 edges: [Edge1 r1=43 r2=44,Edge7 r1=40.5 r2=47]
FEATURE [Part::Feature] Cut001002003003  label="串联铜排001"
  Placement = pos=(0,1,20) rot=(0,0,1;0rad)
  shape: bbox 22 x 56.7 x 4 mm, 18 faces (baked)
FEATURE [Part::FeaturePython] Bend005  # WARN: FeaturePython — macro-defined, semantics opaque (R4)
  AutoMiter = true
  BendType = 0
  LengthList = [23]
  ReliefFactor = 0.7
  UseReliefFactor = false
  angle = 30
  baseObject = -> Chamfer003 [Face8]
  bendAList = [30]
  extend1 = 0
  extend2 = 0
  gap1 = 0
  gap2 = 0
  invert = false
  kfactor = 0.5
  length = 23
  miterangle1 = 0
  miterangle2 = 0
  offset = 0
  radius = 1
  reliefType = 0
  reliefd = 1
  reliefw = 0.8
  sketchflip = false
  sketchinvert = false
  unfold = false
FEATURE [Drawing::FeatureViewPart] Ortho025  label="Ortho_0_014"
  Direction = (1,0,0)
  HiddenWidth = 0.15
  LineWidth = 0.35
  Rotation = -90
  ShowHiddenLines = false
  ShowSmoothLines = false
  Source = -> Bend005
  Tolerance = 0.05
  ViewResult = <g id="Ortho_0_014"\n   transform="rotate(-90,91.5208,239.097) translate(91.5208,239.097) scale(1,1)"\n  >\n<g   fill="none"\n   stroke="rgb(0, 0, 0)"\n   stroke-linecap="butt"\n   stroke-linejoin="miter"\n   stroke-width="0.350000"\n   transform="scale(1,-1)"\n  >\n<path id= "1" d=" M 44.6975 -20.6 L 44.6975 4.9 " />\n</g>\n<g   fill="none"\n   stroke="rgb(0, 0, 0)"\n   stroke-linecap="butt"\n   stroke-linejoin="miter"\n   stroke-width="0.350000"\n   transform="scale(1,-1)"\n  >\n<path id= "1" d=" M 48.7673 4.9 L 52.7066 4.9 " />\n<path id= "2" d=" M 44.7734 4.9 L 48.7673 4.9 " />\n<path d="M44.6975,4.9 Q44.6977,4.9 44.7734,4.9 " /><path id= "4" d=" M 48.7673 -20.6 L 52.7066 -20.6 " />\n<path id= "5" d=" M 48.7673 4.9 L 48.7673 -20.6 " />\n<path id= "6" d=" M 52.7066 4.9 L 52.7066 -20.6 " />\n<path id= "7" d=" M 44.7734 -20.6 L 44.7734 4.9 " />\n<path id= "8" d=" M 48.7673 -20.6 L 44.7734 -20.6 " />\n<path d="M44.6975,-20.6 Q44.6977,-20.6 44.7734,-20.6 " /><path id= "10" d=" M 44.999 -20.6 L 61.0739 -61.1 " />\n<path id= "11" d=" M 65.8588 -38.1 L 65.8588 -61.1 " />\n<path id= "12" d=" M 65.8588 -38.1 L 52.7066 -0.519464 " />\n<path id= "13" d=" M 65.8588 -61.1 L 64.8327 -61.1 " />\n<path id= "14" d=" M 48.7578 -20.6 L 64.8327 -61.1 " />\n<path id= "15" d=" M 61.0739 -61.1 L 64.8327 -61.1 " />\n</g>\n</g>
  Visible = false
  X = 91.5208
  Y = 239.097
FEATURE [Drawing::FeatureViewPart] Ortho026  label="Ortho_1_004"
  Direction = (0,1,0)
  HiddenWidth = 0.15
  LineWidth = 0.35
  Rotation = -90
  ShowHiddenLines = false
  ShowSmoothLines = false
  Source = -> Bend005
  Tolerance = 0.05
  ViewResult = <g id="Ortho_1_004"\n   transform="rotate(-90,293.379,239.097) translate(293.379,239.097) scale(1,1)"\n  >\n<g   fill="none"\n   stroke="rgb(0, 0, 0)"\n   stroke-linecap="butt"\n   stroke-linejoin="miter"\n   stroke-width="0.350000"\n   transform="scale(1,-1)"\n  >\n<path id= "1" d=" M 48.7673 41.2136 L 52.7066 40.519 " />\n<path id= "2" d=" M 48.7673 41.2136 L 44.7734 18.563 " />\n<path id= "3" d=" M 52.7066 40.519 L 48.7126 17.8684 " />\n<path d="M44.999 15.9846 A5 5 0 0 0 44.7734 18.563" /><path d="M48.7578 17.3527 A1 1 0 0 0 48.7126 17.8684" /><path id= "6" d=" M 48.7126 17.8684 L 44.7734 18.563 " />\n<path id= "7" d=" M 44.999 15.9846 L 48.7578 17.3527 " />\n<path id= "8" d=" M 62.1 -31 L 61.0739 -28.1809 " />\n<path id= "9" d=" M 44.999 15.9846 L 61.0739 -28.1809 " />\n<path id= "10" d=" M 65.8588 -29.6319 L 64.8327 -26.8128 " />\n<path id= "11" d=" M 48.7578 17.3527 L 64.8327 -26.8128 " />\n<path id= "12" d=" M 61.0739 -28.1809 L 64.8327 -26.8128 " />\n<path id= "13" d=" M 62.1 -31 L 65.8588 -29.6319 " />\n</g>\n</g>
  Visible = false
  X = 293.379
  Y = 239.097
FEATURE [Drawing::FeatureViewPart] Ortho027  label="Ortho_0_015"
  Direction = (0,0,1)
  HiddenWidth = 0.15
  LineWidth = 0.35
  Rotation = 90
  ShowHiddenLines = false
  ShowSmoothLines = false
  Source = -> Bend005
  Tolerance = 0.05
  ViewResult = <g id="Ortho_0_015"\n   transform="rotate(90,91.5208,82.4028) translate(91.5208,82.4028) scale(1,1)"\n  >\n<g   fill="none"\n   stroke="rgb(0, 0, 0)"\n   stroke-linecap="butt"\n   stroke-linejoin="miter"\n   stroke-width="0.350000"\n   transform="scale(1,-1)"\n  >\n<path id= "1" d=" M 41.2136 -4.9 L 40.519 -4.9 " />\n<path id= "2" d=" M 17.8684 -4.9 L 40.519 -4.9 " />\n<path d="M17.3527,-4.9 C17.5168,-4.9 17.6964,-4.9 17.8684,-4.9 " /><path id= "4" d=" M 41.2136 20.6 L 40.519 20.6 " />\n<path id= "5" d=" M 41.2136 -4.9 L 41.2136 20.6 " />\n<path id= "6" d=" M 40.519 -4.9 L 40.519 20.6 " />\n<path id= "7" d=" M 17.8684 -4.9 L 17.8684 20.6 " />\n<path id= "8" d=" M 40.519 20.6 L 17.8684 20.6 " />\n<path d="M17.3527,20.6 C17.5168,20.6 17.6964,20.6 17.8684,20.6 " /><path id= "10" d=" M 17.3527 -4.9 L 17.3527 20.6 " />\n<path id= "11" d=" M 10.3465 -4.9 L 11.7146 -4.9 " />\n<path id= "12" d=" M 11.7146 -4.9 L 17.3527 -4.9 " />\n<path id= "13" d=" M -31 38.1 L -31 61.1 " />\n<path id= "14" d=" M -31 38.1 L 10.3465 -4.9 " />\n<path id= "15" d=" M -29.6319 38.1 L -29.6319 61.1 " />\n<path id= "16" d=" M -29.6319 38.1 L 11.7146 -4.9 " />\n<path id= "17" d=" M -29.6319 61.1 L -26.8128 61.1 " />\n<path id= "18" d=" M 17.3527 20.6 L -26.8128 61.1 " />\n<path id= "19" d=" M -31 38.1 L -29.6319 38.1 " />\n<path id= "20" d=" M -31 61.1 L -29.6319 61.1 " />\n</g>\n</g>
  Visible = false
  X = 91.5208
  Y = 82.4028
FEATURE [Drawing::FeatureViewPython] dim029  # drawing view (typed FeaturePython)
  Rotation = 0
  ViewResult = <g> <path d = "M 288.586757 182.169001 A 16.855801 16.855801 0 0 0 257.133404 190.596900" style="stroke:rgb(0,0,255);stroke-width:0.50;fill:none" />\n<polygon points="288.586757,182.169001 287.952783,179.070924 286.586758,178.704899 286.220732,180.070924" style="fill:rgb(0,0,255);stroke:rgb(0,0,255);stroke-width:0" />\n<polygon points="257.133404,190.596900 258.133404,187.596900 257.133404,186.596900 256.133404,187.596900" style="fill:rgb(0,0,255);stroke:rgb(0,0,255);stroke-width:0" />\n<text x="262.435942" y="169.607361" font-family="inherit" font-size="3.2" fill="rgb(255,0,37)" text-anchor="-2.07396929851"  >150.0°</text> </g>
  Visible = false
  X = 0
  Y = 0
  arrowL1 = 3
  arrowL2 = 1
  arrowW = 2
  arrow_scheme = 0
  click1_x = 268.075
  click1_y = 174.813
  click2_x = 262.436
  click2_y = 169.607
  comma_decimal_place = false
  dimension_line_overshoot = 1
  gap_datum_points = 2
  lineColor = rgb(0,0,255)
  strokeWidth = 0.5
  textFormat_angular = %(value)3.1f°
  textRenderer_color = rgb(255,0,37)
  textRenderer_family = inherit
  textRenderer_size = 3.2
FEATURE [Drawing::FeaturePage] Page007
  EditableTexts = AUTHOR NAME | CREATION DATE | SUPERVISOR NAME | CHECK DATE | SCALE | WEIGHT | NUMBER | SHEET | TITLE | SUBTITLE
  Group = -> [Ortho025,Ortho026,Ortho027,dim029]
  Template = <path>
FEATURE [Part::FeaturePython] Bend006  # WARN: FeaturePython — macro-defined, semantics opaque (R4)
  AutoMiter = true
  BendType = 0
  LengthList = [20]
  ReliefFactor = 0.7
  UseReliefFactor = false
  angle = -20
  baseObject = -> Chamfer003 [Face1]
  bendAList = [-20]
  extend1 = 0
  extend2 = 0
  gap1 = 0
  gap2 = 0
  invert = false
  kfactor = 0.5
  length = 20
  miterangle1 = 0
  miterangle2 = 0
  offset = 0
  radius = 1
  reliefType = 0
  reliefd = 1
  reliefw = 0.8
  sketchflip = false
  sketchinvert = false
  unfold = false
FEATURE [Part::FeaturePython] Bend007  # WARN: FeaturePython — macro-defined, semantics opaque (R4)
  AutoMiter = true
  BendType = 0
  LengthList = [22]
  ReliefFactor = 0.7
  UseReliefFactor = false
  angle = 20
  baseObject = -> Bend006 [Face16]
  bendAList = [20]
  extend1 = 0
  extend2 = 0
  gap1 = 0
  gap2 = 0
  invert = false
  kfactor = 0.5
  length = 22
  miterangle1 = 0
  miterangle2 = 0
  offset = 0
  radius = 1
  reliefType = 0
  reliefd = 1
  reliefw = 0.8
  sketchflip = false
  sketchinvert = false
  unfold = false
FEATURE [Part::FeaturePython] Bend008  # WARN: FeaturePython — macro-defined, semantics opaque (R4)
  AutoMiter = true
  BendType = 0
  LengthList = [22]
  ReliefFactor = 0.7
  UseReliefFactor = false
  angle = 0
  baseObject = -> Bend007 [Face23]
  bendAList = [0]
  extend1 = 0
  extend2 = 0
  gap1 = 0
  gap2 = 0
  invert = false
  kfactor = 0.5
  length = 22
  miterangle1 = 0
  miterangle2 = 0
  offset = 0
  radius = 1
  reliefType = 0
  reliefd = 1
  reliefw = 0.8
  sketchflip = false
  sketchinvert = false
  unfold = false
FEATURE [Part::FeaturePython] Bend009  label="Bend009_material_0.40ansi"  # WARN: FeaturePython — macro-defined, semantics opaque (R4)
  AutoMiter = true
  BendType = 0
  LengthList = [50]
  ReliefFactor = 0.7
  UseReliefFactor = false
  angle = 90
  baseObject = -> Bend008 [Face3]
  bendAList = [90]
  extend1 = 0
  extend2 = 0
  gap1 = 0
  gap2 = 0
  invert = false
  kfactor = 0.5
  length = 50
  miterangle1 = 0
  miterangle2 = 0
  offset = 0
  radius = 1
  reliefType = 0
  reliefd = 1
  reliefw = 0.8
  sketchflip = false
  sketchinvert = false
  unfold = false
FEATURE [Part::Feature] Unfold002
  shape: bbox 93.82 x 142.1 x 4 mm, 12 faces (baked)
FEATURE [Sketcher::SketchObject] Sketch002  label="Unfold_Sketch002"
  sketch-geometry (13):
    g0: LineSegment StartX=-30.4344 StartY=39.1 StartZ=0 EndX=13.5656 EndY=-4.9 EndZ=0
    g1: LineSegment StartX=-51.342 StartY=39.1 StartZ=0 EndX=-51.342 EndY=137.184 EndZ=0
    g2: LineSegment StartX=-30.4344 StartY=39.1 StartZ=0 EndX=-51.342 EndY=39.1 EndZ=0
    g3: LineSegment StartX=13.5656 StartY=-4.9 StartZ=0 EndX=42.4731 EndY=-4.9 EndZ=0
    g4: LineSegment StartX=42.4731 StartY=-4.9 StartZ=0 EndX=42.4731 EndY=20.6 EndZ=0
    g5: LineSegment StartX=42.4731 StartY=20.6 StartZ=0 EndX=19.5656 EndY=20.6 EndZ=0
    g6: LineSegment StartX=19.5656 StartY=20.6 StartZ=0 EndX=-27.4344 EndY=61.1 EndZ=0
    g7: LineSegment StartX=-31.342 StartY=61.1 StartZ=0 EndX=-27.4344 EndY=61.1 EndZ=0
    g8: LineSegment StartX=-31.342 StartY=137.184 StartZ=0 EndX=-31.342 EndY=61.1 EndZ=0
    g9: LineSegment StartX=-51.342 StartY=137.184 StartZ=0 EndX=-31.342 EndY=137.184 EndZ=0
    g10: LineSegment StartX=20.0193 StartY=-4.9 StartZ=0 EndX=20.0193 EndY=20.6 EndZ=0
    g11: LineSegment StartX=-30.8882 StartY=39.1 StartZ=0 EndX=-30.8882 EndY=61.1 EndZ=0
    g12: LineSegment StartX=-31.342 StartY=85.142 StartZ=0 EndX=-51.342 EndY=85.142 EndZ=0
FEATURE [Part::Feature] Fusion002008006003002002004  label="开孔003"
  shape: bbox 120 x 112 x 94 mm, 237 faces, 2 solids (baked)
FEATURE [Part::Cut] Cut001002003004
  Base = -> Bend009
  Tool = -> Fusion002008006003002002004
FEATURE [Drawing::FeatureViewPart] Ortho028  label="Ortho_0_016"
  Direction = (0,1,0)
  HiddenWidth = 0.15
  LineWidth = 0.35
  Rotation = 90
  ShowHiddenLines = false
  ShowSmoothLines = false
  Source = -> Cut001002003004
  Tolerance = 0.05
  ViewResult = <blob: 2411 chars omitted>
  Visible = false
  X = 133.33
  Y = 21.8397
FEATURE [Drawing::FeatureViewPart] Ortho030  label="Ortho_0_-002"
  Direction = (0,0,1)
  HiddenWidth = 0.15
  LineWidth = 0.35
  Rotation = 0
  ShowHiddenLines = false
  ShowSmoothLines = false
  Source = -> Cut001002003004
  Tolerance = 0.05
  ViewResult = <blob: 2208 chars omitted>
  Visible = false
  X = 133.33
  Y = 199.1
FEATURE [Drawing::FeatureViewPart] Ortho031  label="Ortho_1_005"
  Direction = (1,0,0)
  HiddenWidth = 0.15
  LineWidth = 0.35
  Rotation = 90
  ShowHiddenLines = false
  ShowSmoothLines = false
  Source = -> Cut001002003004
  Tolerance = 0.05
  ViewResult = <g id="Ortho_1_005"\n   transform="rotate(90,333.112,21.8397) translate(333.112,21.8397) scale(1,1)"\n  >\n<g   fill="none"\n   stroke="rgb(0, 0, 0)"\n   stroke-linecap="butt"\n   stroke-linejoin="miter"\n   stroke-width="0.350000"\n   transform="scale(1,-1)"\n  >\n<path id= "1" d=" M 11.1603 -88.1 L 11.1603 -84.1 " />\n<path id= "2" d=" M 11.1603 -88.1 L 61.1603 -88.1 " />\n<path id= "3" d=" M 11.1603 -84.1 L 61.1603 -84.1 " />\n<path d="M66.1603 -83.1 A5 5 0 0 0 61.1603 -88.1" /><path d="M62.1603 -83.1 A1 1 0 0 0 61.1603 -84.1" /><path id= "6" d=" M 61.1603 -84.1 L 61.1603 -88.1 " />\n<path id= "7" d=" M 66.1603 -83.1 L 62.1603 -83.1 " />\n<path id= "8" d=" M 66.1603 -83.1 L 66.1603 -61.1 " />\n<path id= "9" d=" M 62.1603 -83.1 L 62.1603 -61.1 " />\n<path id= "10" d=" M 66.1603 -38.1 L 66.1603 -61.1 " />\n<path d="M65.8588,-61.1 Q66.1584,-61.1 66.1603,-61.1 " /><path d="M65.8588,-38.1 Q66.1584,-38.1 66.1603,-38.1 " /><path id= "13" d=" M 65.8588 -38.1 L 65.8588 -61.1 " />\n<path id= "14" d=" M 61.0739 -61.1 L 64.8327 -61.1 " />\n<path id= "15" d=" M 65.8588 -61.1 L 64.8327 -61.1 " />\n<path id= "16" d=" M 65.8588 -38.1 L 50.8099 4.9 " />\n<path id= "17" d=" M 50.8099 4.9 L 48.7578 4.9 " />\n<path id= "18" d=" M 48.7578 -20.6 L 64.8327 -61.1 " />\n<path id= "19" d=" M 48.7578 4.9 L 48.7578 -20.6 " />\n<path id= "20" d=" M 44.999 -20.6 L 61.0739 -61.1 " />\n<path d="M48.7578,4.9 Q48.6978,4.9 48.6975,4.9 " /><path d="M48.7578,-20.6 Q48.6978,-20.6 48.6975,-20.6 " /><path id= "23" d=" M 48.6975 4.9 L 48.6975 -20.6 " />\n<path id= "24" d=" M 44.6975 4.9 L 44.6975 -20.6 " />\n<path id= "25" d=" M 44.6975 -20.6 L 48.6975 -20.6 " />\n<path id= "26" d=" M 44.6975 4.9 L 48.6975 4.9 " />\n</g>\n</g>
  Visible = false
  X = 333.112
  Y = 21.8397
FEATURE [Drawing::FeatureViewPart] Ortho032  label="Ortho_1_-1"
  Direction = (0.57735,0.57735,0.57735)
  HiddenWidth = 0.15
  LineWidth = 0.35
  Rotation = -60
  ShowHiddenLines = false
  ShowSmoothLines = false
  Source = -> Cut001002003004
  Tolerance = 0.05
  ViewResult = <blob: 3871 chars omitted>
  Visible = false
  X = 325.046
  Y = 140.54
FEATURE [Drawing::FeatureViewPython] dim030  # drawing view (typed FeaturePython)
  Rotation = 0
  ViewResult = <g> <line x1="108.396578" y1="85.988341" x2="116.252628" y2="83.128885" style="stroke:rgb(0,0,255);stroke-width:0.50" />\n<path d = "M 89.627960 88.000000 A 13.241801 13.241801 0 0 1 115.312939 83.470915" style="stroke:rgb(0,0,255);stroke-width:0.50;fill:none" />\n<polygon points="89.627960,88.000000 90.627960,85.000000 89.627960,84.000000 88.627960,85.000000" style="fill:rgb(0,0,255);stroke:rgb(0,0,255);stroke-width:0" />\n<polygon points="115.312939,83.470915 115.226540,80.309817 113.944821,79.712158 113.347161,80.993876" style="fill:rgb(0,0,255);stroke:rgb(0,0,255);stroke-width:0" />\n<text x="103.890990" y="72.501246" font-family="inherit" font-size="3.2" fill="rgb(255,0,37)" text-anchor="-1.50500037634"  >160.0°</text> </g>
  Visible = false
  X = 0
  Y = 0
  arrowL1 = 3
  arrowL2 = 1
  arrowW = 2
  arrow_scheme = 0
  click1_x = 99.1125
  click1_y = 75.3024
  click2_x = 103.891
  click2_y = 72.5012
  comma_decimal_place = false
  dimension_line_overshoot = 1
  gap_datum_points = 2
  lineColor = rgb(0,0,255)
  strokeWidth = 0.5
  textFormat_angular = %(value)3.1f°
  textRenderer_color = rgb(255,0,37)
  textRenderer_family = inherit
  textRenderer_size = 3.2
FEATURE [Drawing::FeatureViewPython] dim031  # drawing view (typed FeaturePython)
  Rotation = 0
  ViewResult = <g> <path d = "M 138.274746 70.856871 A 12.629893 12.629893 0 0 0 162.772859 66.537200" style="stroke:rgb(0,0,255);stroke-width:0.50;fill:none" />\n<polygon points="138.274746,70.856871 138.361112,74.017969 139.642824,74.615643 140.240498,73.333930" style="fill:rgb(0,0,255);stroke:rgb(0,0,255);stroke-width:0" />\n<polygon points="162.772859,66.537200 161.772859,69.537200 162.772859,70.537200 163.772859,69.537200" style="fill:rgb(0,0,255);stroke:rgb(0,0,255);stroke-width:0" />\n<text x="151.213222" y="84.776720" font-family="inherit" font-size="3.2" fill="rgb(255,0,37)" text-anchor="1.51218565861"  >160.0°</text> </g>
  Visible = false
  X = 0
  Y = 0
  arrowL1 = 3
  arrowL2 = 1
  arrowW = 2
  arrow_scheme = 0
  click1_x = 152.336
  click1_y = 78.9752
  click2_x = 151.213
  click2_y = 84.7767
  comma_decimal_place = false
  dimension_line_overshoot = 1
  gap_datum_points = 2
  lineColor = rgb(0,0,255)
  strokeWidth = 0.5
  textFormat_angular = %(value)3.1f°
  textRenderer_color = rgb(255,0,37)
  textRenderer_family = inherit
  textRenderer_size = 3.2
FEATURE [Drawing::FeatureViewPython] dim032  # drawing view (typed FeaturePython)
  Rotation = 0
  ViewResult = <g> \n  <line x1="79.988000" y1="160.000000" x2="69.740839" y2="160.000000" style="stroke:rgb(0,0,255);stroke-width:0.50" />\n<line x1="79.988000" y1="138.000000" x2="69.740839" y2="138.000000" style="stroke:rgb(0,0,255);stroke-width:0.50" />\n<line x1="70.740839" y1="160.000000" x2="70.740839" y2="138.000000" style="stroke:rgb(0,0,255);stroke-width:0.50" /> \n  <polygon points="70.740839,138.000000 69.740839,141.000000 70.740839,142.000000 71.740839,141.000000" style="fill:rgb(0,0,255);stroke:rgb(0,0,255);stroke-width:0" /><polygon points="70.740839,160.000000 71.740839,157.000000 70.740839,156.000000 69.740839,157.000000" style="fill:rgb(0,0,255);stroke:rgb(0,0,255);stroke-width:0" /> \n  <text x="68.740839" y="149.000000" font-family="inherit" font-size="3.2" fill="rgb(255,0,37)" text-anchor="middle" transform="rotate(-90.000000 68.740839,149.000000)" >22</text> </g>
  Visible = false
  X = 0
  Y = 0
  arrowL1 = 3
  arrowL2 = 1
  arrowW = 2
  arrow_scheme = 0
  autoPlaceOffset = 2
  autoPlaceText = true
  click1_x = 70.7408
  click1_y = 145.225
  click2_x = 70.7408
  click2_y = 145.225
  comma_decimal_place = false
  dimension_line_overshoot = 1
  gap_datum_points = 2
  halfDimension_linear = false
  lineColor = rgb(0,0,255)
  strokeWidth = 0.5
  textFormat_linear = %(value)3.3f
  textRenderer_color = rgb(255,0,37)
  textRenderer_family = inherit
  textRenderer_size = 3.2
  unit_custom_scale = 1
  unit_scheme = 0
FEATURE [Drawing::FeatureViewPython] dim033  # drawing view (typed FeaturePython)
  Rotation = 0
  ViewResult = <g> \n  <line x1="79.988000" y1="138.000000" x2="69.553694" y2="138.000000" style="stroke:rgb(0,0,255);stroke-width:0.50" />\n<line x1="79.988000" y1="116.000000" x2="69.553694" y2="116.000000" style="stroke:rgb(0,0,255);stroke-width:0.50" />\n<line x1="70.553694" y1="138.000000" x2="70.553694" y2="116.000000" style="stroke:rgb(0,0,255);stroke-width:0.50" /> \n  <polygon points="70.553694,116.000000 69.553694,119.000000 70.553694,120.000000 71.553694,119.000000" style="fill:rgb(0,0,255);stroke:rgb(0,0,255);stroke-width:0" /><polygon points="70.553694,138.000000 71.553694,135.000000 70.553694,134.000000 69.553694,135.000000" style="fill:rgb(0,0,255);stroke:rgb(0,0,255);stroke-width:0" /> \n  <text x="68.553694" y="127.000000" font-family="inherit" font-size="3.2" fill="rgb(255,0,37)" text-anchor="middle" transform="rotate(-90.000000 68.553694,127.000000)" >22</text> </g>
  Visible = false
  X = 0
  Y = 0
  arrowL1 = 3
  arrowL2 = 1
  arrowW = 2
  arrow_scheme = 0
  autoPlaceOffset = 2
  autoPlaceText = true
  click1_x = 70.5537
  click1_y = 126.697
  click2_x = 70.5537
  click2_y = 126.697
  comma_decimal_place = false
  dimension_line_overshoot = 1
  gap_datum_points = 2
  halfDimension_linear = false
  lineColor = rgb(0,0,255)
  strokeWidth = 0.5
  textFormat_linear = %(value)3.3f
  textRenderer_color = rgb(255,0,37)
  textRenderer_family = inherit
  textRenderer_size = 3.2
  unit_custom_scale = 1
  unit_scheme = 0
FEATURE [Drawing::FeatureViewPython] dim034  # drawing view (typed FeaturePython)
  Rotation = 0
  ViewResult = <g> \n  <line x1="152.034421" y1="177.025940" x2="173.062982" y2="154.094164" style="stroke:rgb(0,0,255);stroke-width:0.50" />\n<line x1="107.868921" y1="136.525940" x2="128.897482" y2="113.594164" style="stroke:rgb(0,0,255);stroke-width:0.50" />\n<line x1="172.387122" y1="154.831194" x2="128.221622" y2="114.331194" style="stroke:rgb(0,0,255);stroke-width:0.50" /> \n  <polygon points="128.221622,114.331194 129.756851,117.095805 131.169741,117.034635 131.108571,115.621745" style="fill:rgb(0,0,255);stroke:rgb(0,0,255);stroke-width:0" /><polygon points="172.387122,154.831194 170.851893,152.066584 169.439003,152.127753 169.500172,153.540643" style="fill:rgb(0,0,255);stroke:rgb(0,0,255);stroke-width:0" /> \n  <text x="148.830312" y="133.229474" font-family="inherit" font-size="3.2" fill="rgb(255,0,37)" text-anchor="middle" transform="rotate(-47.479010 148.830312,133.229474)" >59.924</text> </g>
  Visible = false
  X = 0
  Y = 0
  arrowL1 = 3
  arrowL2 = 1
  arrowW = 2
  arrow_scheme = 0
  autoPlaceOffset = 2
  autoPlaceText = true
  click1_x = 152.523
  click1_y = 136.616
  click2_x = 152.523
  click2_y = 136.616
  comma_decimal_place = false
  dimension_line_overshoot = 1
  gap_datum_points = 2
  halfDimension_linear = false
  lineColor = rgb(0,0,255)
  strokeWidth = 0.5
  textFormat_linear = %(value)3.3f
  textRenderer_color = rgb(255,0,37)
  textRenderer_family = inherit
  textRenderer_size = 3.2
  unit_custom_scale = 1
  unit_scheme = 0
FEATURE [Drawing::FeatureViewPython] dim035  # drawing view (typed FeaturePython)
  Rotation = 0
  ViewResult = <g> \n  <line x1="103.698100" y1="136.000000" x2="103.698100" y2="134.921711" style="stroke:rgb(0,0,255);stroke-width:0.50" />\n<line x1="106.517200" y1="136.000000" x2="106.517200" y2="134.921711" style="stroke:rgb(0,0,255);stroke-width:0.50" />\n<line x1="103.698100" y1="135.921711" x2="106.517200" y2="135.921711" style="stroke:rgb(0,0,255);stroke-width:0.50" /> \n  <polygon points="106.517200,135.921711 109.517200,136.921711 110.517200,135.921711 109.517200,134.921711" style="fill:rgb(0,0,255);stroke:rgb(0,0,255);stroke-width:0" /><polygon points="103.698100,135.921711 100.698100,134.921711 99.698100,135.921711 100.698100,136.921711" style="fill:rgb(0,0,255);stroke:rgb(0,0,255);stroke-width:0" /> \n  <text x="105.107650" y="133.921711" font-family="inherit" font-size="3.2" fill="rgb(255,0,37)" text-anchor="middle" transform="rotate(0.000000 105.107650,133.921711)" >2.819</text> </g>
  Visible = false
  X = 0
  Y = 0
  arrowL1 = 3
  arrowL2 = 1
  arrowW = 2
  arrow_scheme = 0
  autoPlaceOffset = 2
  autoPlaceText = true
  click1_x = 105.002
  click1_y = 135.922
  click2_x = 105.002
  click2_y = 135.922
  comma_decimal_place = false
  dimension_line_overshoot = 1
  gap_datum_points = 2
  halfDimension_linear = false
  lineColor = rgb(0,0,255)
  strokeWidth = 0.5
  textFormat_linear = %(value)3.3f
  textRenderer_color = rgb(255,0,37)
  textRenderer_family = inherit
  textRenderer_size = 3.2
  unit_custom_scale = 1
  unit_scheme = 0
FEATURE [Drawing::FeatureViewPython] dim036  # drawing view (typed FeaturePython)
  Rotation = 0
  ViewResult = <g> \n  <line x1="151.024700" y1="206.000000" x2="151.024700" y2="214.549125" style="stroke:rgb(0,0,255);stroke-width:0.50" />\n<line x1="173.024700" y1="206.000000" x2="173.024700" y2="214.549125" style="stroke:rgb(0,0,255);stroke-width:0.50" />\n<line x1="151.024700" y1="213.549125" x2="173.024700" y2="213.549125" style="stroke:rgb(0,0,255);stroke-width:0.50" /> \n  <polygon points="173.024700,213.549125 170.024700,212.549125 169.024700,213.549125 170.024700,214.549125" style="fill:rgb(0,0,255);stroke:rgb(0,0,255);stroke-width:0" /><polygon points="151.024700,213.549125 154.024700,214.549125 155.024700,213.549125 154.024700,212.549125" style="fill:rgb(0,0,255);stroke:rgb(0,0,255);stroke-width:0" /> \n  <text x="162.024700" y="211.549125" font-family="inherit" font-size="3.2" fill="rgb(255,0,37)" text-anchor="middle" transform="rotate(0.000000 162.024700,211.549125)" >22</text> </g>
  Visible = false
  X = 0
  Y = 0
  arrowL1 = 3
  arrowL2 = 1
  arrowW = 2
  arrow_scheme = 0
  autoPlaceOffset = 2
  autoPlaceText = true
  click1_x = 161.614
  click1_y = 213.549
  click2_x = 161.614
  click2_y = 213.549
  comma_decimal_place = false
  dimension_line_overshoot = 1
  gap_datum_points = 2
  halfDimension_linear = false
  lineColor = rgb(0,0,255)
  strokeWidth = 0.5
  textFormat_linear = %(value)3.3f
  textRenderer_color = rgb(255,0,37)
  textRenderer_family = inherit
  textRenderer_size = 3.2
  unit_custom_scale = 1
  unit_scheme = 0
FEATURE [Drawing::FeatureViewPython] dim037  # drawing view (typed FeaturePython)
  Rotation = 0
  ViewResult = <g> \n  <line x1="175.024700" y1="204.000000" x2="183.627212" y2="204.000000" style="stroke:rgb(0,0,255);stroke-width:0.50" />\n<line x1="175.024700" y1="178.500000" x2="183.627212" y2="178.500000" style="stroke:rgb(0,0,255);stroke-width:0.50" />\n<line x1="182.627212" y1="204.000000" x2="182.627212" y2="178.500000" style="stroke:rgb(0,0,255);stroke-width:0.50" /> \n  <polygon points="182.627212,178.500000 181.627212,181.500000 182.627212,182.500000 183.627212,181.500000" style="fill:rgb(0,0,255);stroke:rgb(0,0,255);stroke-width:0" /><polygon points="182.627212,204.000000 183.627212,201.000000 182.627212,200.000000 181.627212,201.000000" style="fill:rgb(0,0,255);stroke:rgb(0,0,255);stroke-width:0" /> \n  <text x="180.627212" y="191.250000" font-family="inherit" font-size="3.2" fill="rgb(255,0,37)" text-anchor="middle" transform="rotate(-90.000000 180.627212,191.250000)" >25.5</text> </g>
  Visible = false
  X = 0
  Y = 0
  arrowL1 = 3
  arrowL2 = 1
  arrowW = 2
  arrow_scheme = 0
  autoPlaceOffset = 2
  autoPlaceText = true
  click1_x = 182.627
  click1_y = 193.903
  click2_x = 182.627
  click2_y = 193.903
  comma_decimal_place = false
  dimension_line_overshoot = 1
  gap_datum_points = 2
  halfDimension_linear = false
  lineColor = rgb(0,0,255)
  strokeWidth = 0.5
  textFormat_linear = %(value)3.3f
  textRenderer_color = rgb(255,0,37)
  textRenderer_family = inherit
  textRenderer_size = 3.2
  unit_custom_scale = 1
  unit_scheme = 0
FEATURE [Drawing::FeatureViewPython] dim038  # drawing view (typed FeaturePython)
  Rotation = 0
  ViewResult = <g> \n  <line x1="167.330000" y1="199.100000" x2="172.387201" y2="199.100000" style="stroke:rgb(0,0,255);stroke-width:0.50" />\n<line x1="167.330000" y1="183.500000" x2="172.387201" y2="183.500000" style="stroke:rgb(0,0,255);stroke-width:0.50" />\n<line x1="171.387201" y1="199.100000" x2="171.387201" y2="183.500000" style="stroke:rgb(0,0,255);stroke-width:0.50" /> \n  <polygon points="171.387201,183.500000 170.387201,186.500000 171.387201,187.500000 172.387201,186.500000" style="fill:rgb(0,0,255);stroke:rgb(0,0,255);stroke-width:0" /><polygon points="171.387201,199.100000 172.387201,196.100000 171.387201,195.100000 170.387201,196.100000" style="fill:rgb(0,0,255);stroke:rgb(0,0,255);stroke-width:0" /> \n  <text x="169.387201" y="191.300000" font-family="inherit" font-size="3.2" fill="rgb(255,0,37)" text-anchor="middle" transform="rotate(-90.000000 169.387201,191.300000)" >15.6</text> </g>
  Visible = false
  X = 0
  Y = 0
  arrowL1 = 3
  arrowL2 = 1
  arrowW = 2
  arrow_scheme = 0
  autoPlaceOffset = 2
  autoPlaceText = true
  click1_x = 171.387
  click1_y = 184.474
  click2_x = 171.387
  click2_y = 184.474
  comma_decimal_place = false
  dimension_line_overshoot = 1
  gap_datum_points = 2
  halfDimension_linear = false
  lineColor = rgb(0,0,255)
  strokeWidth = 0.5
  textFormat_linear = %(value)3.3f
  textRenderer_color = rgb(255,0,37)
  textRenderer_family = inherit
  textRenderer_size = 3.2
  unit_custom_scale = 1
  unit_scheme = 0
FEATURE [Drawing::FeatureViewPython] dim040  # drawing view (typed FeaturePython)
  Rotation = 0
  ViewResult = <g> \n  <line x1="175.024700" y1="204.000000" x2="192.061983" y2="204.000000" style="stroke:rgb(0,0,255);stroke-width:0.50" />\n<line x1="167.330000" y1="199.100000" x2="192.061983" y2="199.100000" style="stroke:rgb(0,0,255);stroke-width:0.50" />\n<line x1="191.061983" y1="204.000000" x2="191.061983" y2="199.100000" style="stroke:rgb(0,0,255);stroke-width:0.50" /> \n  <polygon points="191.061983,199.100000 192.061983,196.100000 191.061983,195.100000 190.061983,196.100000" style="fill:rgb(0,0,255);stroke:rgb(0,0,255);stroke-width:0" /><polygon points="191.061983,204.000000 190.061983,207.000000 191.061983,208.000000 192.061983,207.000000" style="fill:rgb(0,0,255);stroke:rgb(0,0,255);stroke-width:0" /> \n  <text x="189.061983" y="201.550000" font-family="inherit" font-size="3.2" fill="rgb(255,0,37)" text-anchor="middle" transform="rotate(-90.000000 189.061983,201.550000)" >4.9</text> </g>
  Visible = false
  X = 0
  Y = 0
  arrowL1 = 3
  arrowL2 = 1
  arrowW = 2
  arrow_scheme = 0
  autoPlaceOffset = 2
  autoPlaceText = true
  click1_x = 191.062
  click1_y = 200.177
  click2_x = 191.062
  click2_y = 200.177
  comma_decimal_place = false
  dimension_line_overshoot = 1
  gap_datum_points = 2
  halfDimension_linear = false
  lineColor = rgb(0,0,255)
  strokeWidth = 0.5
  textFormat_linear = %(value)3.3f
  textRenderer_color = rgb(255,0,37)
  textRenderer_family = inherit
  textRenderer_size = 3.2
  unit_custom_scale = 1
  unit_scheme = 0
FEATURE [Drawing::FeatureViewPython] dim039  # drawing view (typed FeaturePython)
  Rotation = 0
  ViewResult = <g> \n  <line x1="167.330000" y1="183.500000" x2="191.956690" y2="183.500000" style="stroke:rgb(0,0,255);stroke-width:0.50" />\n<line x1="175.024700" y1="178.500000" x2="191.956690" y2="178.500000" style="stroke:rgb(0,0,255);stroke-width:0.50" />\n<line x1="190.956690" y1="183.500000" x2="190.956690" y2="178.500000" style="stroke:rgb(0,0,255);stroke-width:0.50" /> \n  <polygon points="190.956690,178.500000 191.956690,175.500000 190.956690,174.500000 189.956690,175.500000" style="fill:rgb(0,0,255);stroke:rgb(0,0,255);stroke-width:0" /><polygon points="190.956690,183.500000 189.956690,186.500000 190.956690,187.500000 191.956690,186.500000" style="fill:rgb(0,0,255);stroke:rgb(0,0,255);stroke-width:0" /> \n  <text x="188.956690" y="181.000000" font-family="inherit" font-size="3.2" fill="rgb(255,0,37)" text-anchor="middle" transform="rotate(-90.000000 188.956690,181.000000)" >5</text> </g>
  Visible = false
  X = 0
  Y = 0
  arrowL1 = 3
  arrowL2 = 1
  arrowW = 2
  arrow_scheme = 0
  autoPlaceOffset = 2
  autoPlaceText = true
  click1_x = 190.957
  click1_y = 181.48
  click2_x = 190.957
  click2_y = 181.48
  comma_decimal_place = false
  dimension_line_overshoot = 1
  gap_datum_points = 2
  halfDimension_linear = false
  lineColor = rgb(0,0,255)
  strokeWidth = 0.5
  textFormat_linear = %(value)3.3f
  textRenderer_color = rgb(255,0,37)
  textRenderer_family = inherit
  textRenderer_size = 3.2
  unit_custom_scale = 1
  unit_scheme = 0
FEATURE [Drawing::FeatureViewPython] dim041  # drawing view (typed FeaturePython)
  Rotation = 0
  ViewResult = <g> \n  <line x1="165.330000" y1="181.500000" x2="165.330000" y2="171.547693" style="stroke:rgb(0,0,255);stroke-width:0.50" />\n<line x1="173.024700" y1="176.500000" x2="173.024700" y2="171.547693" style="stroke:rgb(0,0,255);stroke-width:0.50" />\n<line x1="165.330000" y1="172.547693" x2="173.024700" y2="172.547693" style="stroke:rgb(0,0,255);stroke-width:0.50" /> \n  <polygon points="173.024700,172.547693 176.024700,173.547693 177.024700,172.547693 176.024700,171.547693" style="fill:rgb(0,0,255);stroke:rgb(0,0,255);stroke-width:0" /><polygon points="165.330000,172.547693 162.330000,171.547693 161.330000,172.547693 162.330000,173.547693" style="fill:rgb(0,0,255);stroke:rgb(0,0,255);stroke-width:0" /> \n  <text x="169.177350" y="170.547693" font-family="inherit" font-size="3.2" fill="rgb(255,0,37)" text-anchor="middle" transform="rotate(0.000000 169.177350,170.547693)" >7.695</text> </g>
  Visible = false
  X = 0
  Y = 0
  arrowL1 = 3
  arrowL2 = 1
  arrowW = 2
  arrow_scheme = 0
  autoPlaceOffset = 2
  autoPlaceText = true
  click1_x = 172.206
  click1_y = 172.548
  click2_x = 172.206
  click2_y = 172.548
  comma_decimal_place = false
  dimension_line_overshoot = 1
  gap_datum_points = 2
  halfDimension_linear = false
  lineColor = rgb(0,0,255)
  strokeWidth = 0.5
  textFormat_linear = %(value)3.3f
  textRenderer_color = rgb(255,0,37)
  textRenderer_family = inherit
  textRenderer_size = 3.2
  unit_custom_scale = 1
  unit_scheme = 0
FEATURE [Drawing::FeatureViewPython] dim042  # drawing view (typed FeaturePython)
  Rotation = 0
  ViewResult = <g> \n  <line x1="79.988000" y1="83.000000" x2="72.674448" y2="83.000000" style="stroke:rgb(0,0,255);stroke-width:0.50" />\n<line x1="79.988000" y1="33.000000" x2="72.674448" y2="33.000000" style="stroke:rgb(0,0,255);stroke-width:0.50" />\n<line x1="73.674448" y1="83.000000" x2="73.674448" y2="33.000000" style="stroke:rgb(0,0,255);stroke-width:0.50" /> \n  <polygon points="73.674448,33.000000 72.674448,36.000000 73.674448,37.000000 74.674448,36.000000" style="fill:rgb(0,0,255);stroke:rgb(0,0,255);stroke-width:0" /><polygon points="73.674448,83.000000 74.674448,80.000000 73.674448,79.000000 72.674448,80.000000" style="fill:rgb(0,0,255);stroke:rgb(0,0,255);stroke-width:0" /> \n  <text x="71.674448" y="58.000000" font-family="inherit" font-size="3.2" fill="rgb(255,0,37)" text-anchor="middle" transform="rotate(-90.000000 71.674448,58.000000)" >50</text> </g>
  Visible = false
  X = 0
  Y = 0
  arrowL1 = 3
  arrowL2 = 1
  arrowW = 2
  arrow_scheme = 0
  autoPlaceOffset = 2
  autoPlaceText = true
  click1_x = 73.6744
  click1_y = 52.6755
  click2_x = 73.6744
  click2_y = 52.6755
  comma_decimal_place = false
  dimension_line_overshoot = 1
  gap_datum_points = 2
  halfDimension_linear = false
  lineColor = rgb(0,0,255)
  strokeWidth = 0.5
  textFormat_linear = %(value)3.3f
  textRenderer_color = rgb(255,0,37)
  textRenderer_family = inherit
  textRenderer_size = 3.2
  unit_custom_scale = 1
  unit_scheme = 0
FEATURE [Drawing::FeatureViewPython] dim043  # drawing view (typed FeaturePython)
  Rotation = 0
  ViewResult = <g> \n  <line x1="81.988000" y1="31.000000" x2="81.988000" y2="27.829132" style="stroke:rgb(0,0,255);stroke-width:0.50" />\n<line x1="101.988000" y1="31.000000" x2="101.988000" y2="27.829132" style="stroke:rgb(0,0,255);stroke-width:0.50" />\n<line x1="81.988000" y1="28.829132" x2="101.988000" y2="28.829132" style="stroke:rgb(0,0,255);stroke-width:0.50" /> \n  <polygon points="101.988000,28.829132 98.988000,27.829132 97.988000,28.829132 98.988000,29.829132" style="fill:rgb(0,0,255);stroke:rgb(0,0,255);stroke-width:0" /><polygon points="81.988000,28.829132 84.988000,29.829132 85.988000,28.829132 84.988000,27.829132" style="fill:rgb(0,0,255);stroke:rgb(0,0,255);stroke-width:0" /> \n  <text x="91.988000" y="26.829132" font-family="inherit" font-size="3.2" fill="rgb(255,0,37)" text-anchor="middle" transform="rotate(0.000000 91.988000,26.829132)" >20</text> </g>
  Visible = false
  X = 0
  Y = 0
  arrowL1 = 3
  arrowL2 = 1
  arrowW = 2
  arrow_scheme = 0
  autoPlaceOffset = 2
  autoPlaceText = true
  click1_x = 93.9616
  click1_y = 28.8291
  click2_x = 93.9616
  click2_y = 28.8291
  comma_decimal_place = false
  dimension_line_overshoot = 1
  gap_datum_points = 2
  halfDimension_linear = false
  lineColor = rgb(0,0,255)
  strokeWidth = 0.5
  textFormat_linear = %(value)3.3f
  textRenderer_color = rgb(255,0,37)
  textRenderer_family = inherit
  textRenderer_size = 3.2
  unit_custom_scale = 1
  unit_scheme = 0
FEATURE [Drawing::FeatureViewPython] dim044  # drawing view (typed FeaturePython)
  Rotation = 0
  ViewResult = <g> \n  <line x1="93.230000" y1="45.839700" x2="93.230000" y2="56.641411" style="stroke:rgb(0,0,255);stroke-width:0.50" />\n<line x1="101.988000" y1="35.000000" x2="101.988000" y2="56.641411" style="stroke:rgb(0,0,255);stroke-width:0.50" />\n<line x1="93.230000" y1="55.641411" x2="101.988000" y2="55.641411" style="stroke:rgb(0,0,255);stroke-width:0.50" /> \n  <polygon points="101.988000,55.641411 104.988000,56.641411 105.988000,55.641411 104.988000,54.641411" style="fill:rgb(0,0,255);stroke:rgb(0,0,255);stroke-width:0" /><polygon points="93.230000,55.641411 90.230000,54.641411 89.230000,55.641411 90.230000,56.641411" style="fill:rgb(0,0,255);stroke:rgb(0,0,255);stroke-width:0" /> \n  <text x="97.609000" y="53.641411" font-family="inherit" font-size="3.2" fill="rgb(255,0,37)" text-anchor="middle" transform="rotate(0.000000 97.609000,53.641411)" >8.758</text> </g>
  Visible = false
  X = 0
  Y = 0
  arrowL1 = 3
  arrowL2 = 1
  arrowW = 2
  arrow_scheme = 0
  autoPlaceOffset = 2
  autoPlaceText = true
  click1_x = 100.249
  click1_y = 55.6414
  click2_x = 100.249
  click2_y = 55.6414
  comma_decimal_place = false
  dimension_line_overshoot = 1
  gap_datum_points = 2
  halfDimension_linear = false
  lineColor = rgb(0,0,255)
  strokeWidth = 0.5
  textFormat_linear = %(value)3.3f
  textRenderer_color = rgb(255,0,37)
  textRenderer_family = inherit
  textRenderer_size = 3.2
  unit_custom_scale = 1
  unit_scheme = 0
FEATURE [Drawing::FeatureViewPython] dim045  # drawing view (typed FeaturePython)
  Rotation = 0
  ViewResult = <g> \n  <line x1="93.230000" y1="41.839700" x2="93.230000" y2="36.727012" style="stroke:rgb(0,0,255);stroke-width:0.50" />\n<line x1="81.988000" y1="35.000000" x2="81.988000" y2="38.727012" style="stroke:rgb(0,0,255);stroke-width:0.50" />\n<line x1="93.230000" y1="37.727012" x2="81.988000" y2="37.727012" style="stroke:rgb(0,0,255);stroke-width:0.50" /> \n  <polygon points="81.988000,37.727012 84.988000,38.727012 85.988000,37.727012 84.988000,36.727012" style="fill:rgb(0,0,255);stroke:rgb(0,0,255);stroke-width:0" /><polygon points="93.230000,37.727012 90.230000,36.727012 89.230000,37.727012 90.230000,38.727012" style="fill:rgb(0,0,255);stroke:rgb(0,0,255);stroke-width:0" /> \n  <text x="87.609000" y="35.727012" font-family="inherit" font-size="3.2" fill="rgb(255,0,37)" text-anchor="middle" transform="rotate(0.000000 87.609000,35.727012)" >11.242</text> </g>
  Visible = false
  X = 0
  Y = 0
  arrowL1 = 3
  arrowL2 = 1
  arrowW = 2
  arrow_scheme = 0
  autoPlaceOffset = 2
  autoPlaceText = true
  click1_x = 86.0128
  click1_y = 37.727
  click2_x = 86.0128
  click2_y = 37.727
  comma_decimal_place = false
  dimension_line_overshoot = 1
  gap_datum_points = 2
  halfDimension_linear = false
  lineColor = rgb(0,0,255)
  strokeWidth = 0.5
  textFormat_linear = %(value)3.3f
  textRenderer_color = rgb(255,0,37)
  textRenderer_family = inherit
  textRenderer_size = 3.2
  unit_custom_scale = 1
  unit_scheme = 0
FEATURE [Drawing::FeatureViewPython] dim046  # drawing view (typed FeaturePython)
  Rotation = 0
  ViewResult = <g> \n  <line x1="95.230000" y1="43.839700" x2="118.807934" y2="43.839700" style="stroke:rgb(0,0,255);stroke-width:0.50" />\n<line x1="103.988000" y1="33.000000" x2="118.807934" y2="33.000000" style="stroke:rgb(0,0,255);stroke-width:0.50" />\n<line x1="117.807934" y1="43.839700" x2="117.807934" y2="33.000000" style="stroke:rgb(0,0,255);stroke-width:0.50" /> \n  <polygon points="117.807934,33.000000 116.807934,36.000000 117.807934,37.000000 118.807934,36.000000" style="fill:rgb(0,0,255);stroke:rgb(0,0,255);stroke-width:0" /><polygon points="117.807934,43.839700 118.807934,40.839700 117.807934,39.839700 116.807934,40.839700" style="fill:rgb(0,0,255);stroke:rgb(0,0,255);stroke-width:0" /> \n  <text x="115.807934" y="38.419850" font-family="inherit" font-size="3.2" fill="rgb(255,0,37)" text-anchor="middle" transform="rotate(-90.000000 115.807934,38.419850)" >10.84</text> </g>
  Visible = false
  X = 0
  Y = 0
  arrowL1 = 3
  arrowL2 = 1
  arrowW = 2
  arrow_scheme = 0
  autoPlaceOffset = 2
  autoPlaceText = true
  click1_x = 117.808
  click1_y = 37.9643
  click2_x = 117.808
  click2_y = 37.9643
  comma_decimal_place = false
  dimension_line_overshoot = 1
  gap_datum_points = 2
  halfDimension_linear = false
  lineColor = rgb(0,0,255)
  strokeWidth = 0.5
  textFormat_linear = %(value)3.3f
  textRenderer_color = rgb(255,0,37)
  textRenderer_family = inherit
  textRenderer_size = 3.2
  unit_custom_scale = 1
  unit_scheme = 0
FEATURE [Drawing::FeatureViewPython] dia017  # drawing view (typed FeaturePython)
  Rotation = 0
  ViewResult = <g>  <circle cx ="93.230000" cy ="43.839700" r="0.250000" stroke="none" fill="rgb(0,0,255)" /> \n<line x1="98.363452" y1="49.630874" x2="91.074164" y2="41.407649" style="stroke:rgb(0,0,255);stroke-width:0.50" />\n<polygon points="95.385836,46.271751 96.627514,49.180056 98.039172,49.265045 98.124161,47.853388" style="fill:rgb(0,0,255);stroke:rgb(0,0,255);stroke-width:0" />\n<polygon points="91.074164,41.407649 89.832486,38.499344 88.420828,38.414355 88.335839,39.826012" style="fill:rgb(0,0,255);stroke:rgb(0,0,255);stroke-width:0" />\n<line x1="98.363452" y1="49.630874" x2="117.676824" y2="49.630874" style="stroke:rgb(0,0,255);stroke-width:0.50" />\n<text x="108.020138" y="47.630874" font-family="inherit" font-size="3.2" fill="rgb(255,0,37)" text-anchor="middle" transform="rotate(0.000000 108.020138,47.630874)" >Ø6.5</text> </g>
  Visible = false
  X = 0
  Y = 0
  arrowL1 = 3
  arrowL2 = 1
  arrowW = 2
  arrow_scheme = 0
  autoPlaceOffset = 2
  autoPlaceText = true
  centerPointDia = 0.5
  click1_x = 98.3635
  click1_y = 49.6309
  click2_x = 117.677
  click2_y = 51.8766
  click3_x = 117.677
  click3_y = 51.8766
  comma_decimal_place = false
  lineColor = rgb(0,0,255)
  strokeWidth = 0.5
  textFormat_circular = Ø%(value)3.3f
  textRenderer_color = rgb(255,0,37)
  textRenderer_family = inherit
  textRenderer_size = 3.2
  unit_custom_scale = 1
  unit_scheme = 0
FEATURE [Drawing::FeatureViewPython] dia018  # drawing view (typed FeaturePython)
  Rotation = 0
  ViewResult = <g>  <circle cx ="165.330000" cy ="183.500000" r="0.250000" stroke="none" fill="rgb(0,0,255)" /> \n<line x1="157.996558" y1="189.879272" x2="167.291661" y2="181.793575" style="stroke:rgb(0,0,255);stroke-width:0.50" />\n<polygon points="163.368339,185.206425 160.448567,186.420892 160.350399,187.831694 161.761201,187.929862" style="fill:rgb(0,0,255);stroke:rgb(0,0,255);stroke-width:0" />\n<polygon points="167.291661,181.793575 170.211433,180.579108 170.309601,179.168306 168.898799,179.070138" style="fill:rgb(0,0,255);stroke:rgb(0,0,255);stroke-width:0" />\n<line x1="157.996558" y1="189.879272" x2="153.745530" y2="189.879272" style="stroke:rgb(0,0,255);stroke-width:0.50" />\n<text x="155.871044" y="187.879272" font-family="inherit" font-size="3.2" fill="rgb(255,0,37)" text-anchor="middle" transform="rotate(0.000000 155.871044,187.879272)" >Ø5.2</text> </g>
  Visible = false
  X = 0
  Y = 0
  arrowL1 = 3
  arrowL2 = 1
  arrowW = 2
  arrow_scheme = 0
  autoPlaceOffset = 2
  autoPlaceText = true
  centerPointDia = 0.5
  click1_x = 157.997
  click1_y = 189.879
  click2_x = 153.746
  click2_y = 188.462
  click3_x = 153.746
  click3_y = 188.462
  comma_decimal_place = false
  lineColor = rgb(0,0,255)
  strokeWidth = 0.5
  textFormat_circular = Ø%(value)3.3f
  textRenderer_color = rgb(255,0,37)
  textRenderer_family = inherit
  textRenderer_size = 3.2
  unit_custom_scale = 1
  unit_scheme = 0
FEATURE [Drawing::FeatureViewPython] dia019  # drawing view (typed FeaturePython)
  Rotation = 0
  ViewResult = <g>  <circle cx ="165.330000" cy ="199.100000" r="0.250000" stroke="none" fill="rgb(0,0,255)" /> \n<line x1="154.808287" y1="201.569600" x2="167.861211" y2="198.505888" style="stroke:rgb(0,0,255);stroke-width:0.50" />\n<polygon points="162.798789,199.694112 159.649656,199.406084 158.904618,200.608131 160.106665,201.353169" style="fill:rgb(0,0,255);stroke:rgb(0,0,255);stroke-width:0" />\n<polygon points="167.861211,198.505888 171.010344,198.793916 171.755382,197.591869 170.553335,196.846831" style="fill:rgb(0,0,255);stroke:rgb(0,0,255);stroke-width:0" />\n<line x1="154.808287" y1="201.569600" x2="155.162539" y2="201.569600" style="stroke:rgb(0,0,255);stroke-width:0.50" />\n<text x="154.985413" y="199.569600" font-family="inherit" font-size="3.2" fill="rgb(255,0,37)" text-anchor="middle" transform="rotate(0.000000 154.985413,199.569600)" >Ø5.2</text> </g>
  Visible = false
  X = 0
  Y = 0
  arrowL1 = 3
  arrowL2 = 1
  arrowW = 2
  arrow_scheme = 0
  autoPlaceOffset = 2
  autoPlaceText = true
  centerPointDia = 0.5
  click1_x = 154.808
  click1_y = 201.57
  click2_x = 155.163
  click2_y = 197.673
  click3_x = 155.163
  click3_y = 197.673
  comma_decimal_place = false
  lineColor = rgb(0,0,255)
  strokeWidth = 0.5
  textFormat_circular = Ø%(value)3.3f
  textRenderer_color = rgb(255,0,37)
  textRenderer_family = inherit
  textRenderer_size = 3.2
  unit_custom_scale = 1
  unit_scheme = 0
FEATURE [Drawing::FeaturePage] Page008
  EditableTexts = AUTHOR NAME | CREATION DATE | SUPERVISOR NAME | CHECK DATE | SCALE | WEIGHT | NUMBER | SHEET | TITLE | SUBTITLE
  Group = -> [Ortho028,Ortho030,Ortho031,Ortho032,dim030,dim031,dim032,dim033,dim034,dim035,dim036,dim037,dim038,dim040,dim039,dim041,dim042,dim043,dim044,dim045,dim046,dia017,dia018,dia019]
  Template = <path>
FEATURE [Drawing::FeatureViewPart] Ortho033  label="Ortho_0_017"
  Direction = (0,0,1)
  HiddenWidth = 0.15
  LineWidth = 0.35
  Rotation = 0
  Scale = 1.5
  ShowHiddenLines = false
  ShowSmoothLines = false
  Source = -> Unfold002
  Tolerance = 0.05
  ViewResult = <g id="Ortho_0_017"\n   transform="rotate(0,121.652,247.713) translate(121.652,247.713) scale(1.5,1.5)"\n  >\n<g   fill="none"\n   stroke="rgb(0, 0, 0)"\n   stroke-linecap="butt"\n   stroke-linejoin="miter"\n   stroke-width="0.233333"\n   transform="scale(1,-1)"\n  >\n<path id= "1" d=" M -30.4344 39.1 L 13.5656 -4.9 " />\n<path id= "2" d=" M -51.342 39.1 L -51.342 137.184 " />\n<path id= "3" d=" M -30.4344 39.1 L -51.342 39.1 " />\n<path id= "4" d=" M 13.5656 -4.9 L 42.4731 -4.9 " />\n<path id= "5" d=" M 42.4731 -4.9 L 42.4731 20.6 " />\n<path id= "6" d=" M 42.4731 20.6 L 19.5656 20.6 " />\n<path id= "7" d=" M 19.5656 20.6 L -27.4344 61.1 " />\n<path id= "8" d=" M -31.342 61.1 L -27.4344 61.1 " />\n<path id= "9" d=" M -31.342 137.184 L -31.342 61.1 " />\n<path id= "10" d=" M -51.342 137.184 L -31.342 137.184 " />\n</g>\n</g>
  Visible = false
  X = 121.652
  Y = 247.713
FEATURE [Drawing::FeatureViewPython] dim047  # drawing view (typed FeaturePython)
  Rotation = 0
  ViewResult = <g> \n  <line x1="44.639000" y1="39.937000" x2="44.639000" y2="27.906994" style="stroke:rgb(0,0,255);stroke-width:0.50" />\n<line x1="74.639000" y1="39.937000" x2="74.639000" y2="27.906994" style="stroke:rgb(0,0,255);stroke-width:0.50" />\n<line x1="44.639000" y1="28.906994" x2="74.639000" y2="28.906994" style="stroke:rgb(0,0,255);stroke-width:0.50" /> \n  <polygon points="74.639000,28.906994 71.639000,27.906994 70.639000,28.906994 71.639000,29.906994" style="fill:rgb(0,0,255);stroke:rgb(0,0,255);stroke-width:0" /><polygon points="44.639000,28.906994 47.639000,29.906994 48.639000,28.906994 47.639000,27.906994" style="fill:rgb(0,0,255);stroke:rgb(0,0,255);stroke-width:0" /> \n  <text x="59.639000" y="26.906994" font-family="inherit" font-size="3.2" fill="rgb(255,0,37)" text-anchor="middle" transform="rotate(0.000000 59.639000,26.906994)" >20</text> </g>
  Visible = false
  X = 0
  Y = 0
  arrowL1 = 3
  arrowL2 = 1
  arrowW = 2
  arrow_scheme = 0
  autoPlaceOffset = 2
  autoPlaceText = true
  click1_x = 58.2391
  click1_y = 28.907
  click2_x = 58.2391
  click2_y = 28.907
  comma_decimal_place = false
  dimension_line_overshoot = 1
  gap_datum_points = 2
  halfDimension_linear = false
  lineColor = rgb(0,0,255)
  strokeWidth = 0.5
  textFormat_linear = %(value)3.3f
  textRenderer_color = rgb(255,0,37)
  textRenderer_family = inherit
  textRenderer_size = 3.2
  unit_custom_scale = 1
  unit_scheme = 0
FEATURE [Drawing::FeatureViewPython] dim048  # drawing view (typed FeaturePython)
  Rotation = 0
  ViewResult = <g> \n  <line x1="76.639000" y1="41.937000" x2="95.797935" y2="41.937000" style="stroke:rgb(0,0,255);stroke-width:0.50" />\n<line x1="76.639000" y1="156.063000" x2="95.797935" y2="156.063000" style="stroke:rgb(0,0,255);stroke-width:0.50" />\n<line x1="94.797935" y1="41.937000" x2="94.797935" y2="156.063000" style="stroke:rgb(0,0,255);stroke-width:0.50" /> \n  <polygon points="94.797935,156.063000 95.797935,153.063000 94.797935,152.063000 93.797935,153.063000" style="fill:rgb(0,0,255);stroke:rgb(0,0,255);stroke-width:0" /><polygon points="94.797935,41.937000 93.797935,44.937000 94.797935,45.937000 95.797935,44.937000" style="fill:rgb(0,0,255);stroke:rgb(0,0,255);stroke-width:0" /> \n  <text x="92.797935" y="99.000000" font-family="inherit" font-size="3.2" fill="rgb(255,0,37)" text-anchor="middle" transform="rotate(-90.000000 92.797935,99.000000)" >76.084</text> </g>
  Visible = false
  X = 0
  Y = 0
  arrowL1 = 3
  arrowL2 = 1
  arrowW = 2
  arrow_scheme = 0
  autoPlaceOffset = 2
  autoPlaceText = true
  click1_x = 94.7979
  click1_y = 73.5428
  click2_x = 94.7979
  click2_y = 73.5428
  comma_decimal_place = false
  dimension_line_overshoot = 1
  gap_datum_points = 2
  halfDimension_linear = false
  lineColor = rgb(0,0,255)
  strokeWidth = 0.5
  textFormat_linear = %(value)3.3f
  textRenderer_color = rgb(255,0,37)
  textRenderer_family = inherit
  textRenderer_size = 3.2
  unit_custom_scale = 1
  unit_scheme = 0
FEATURE [Drawing::FeatureViewPython] dim049  # drawing view (typed FeaturePython)
  Rotation = 0
  ViewResult = <g> \n  <line x1="74.639000" y1="154.063000" x2="74.639000" y2="148.975985" style="stroke:rgb(0,0,255);stroke-width:0.50" />\n<line x1="80.500400" y1="154.063000" x2="80.500400" y2="148.975985" style="stroke:rgb(0,0,255);stroke-width:0.50" />\n<line x1="74.639000" y1="149.975985" x2="80.500400" y2="149.975985" style="stroke:rgb(0,0,255);stroke-width:0.50" /> \n  <polygon points="80.500400,149.975985 83.500400,150.975985 84.500400,149.975985 83.500400,148.975985" style="fill:rgb(0,0,255);stroke:rgb(0,0,255);stroke-width:0" /><polygon points="74.639000,149.975985 71.639000,148.975985 70.639000,149.975985 71.639000,150.975985" style="fill:rgb(0,0,255);stroke:rgb(0,0,255);stroke-width:0" /> \n  <text x="77.569700" y="147.975985" font-family="inherit" font-size="3.2" fill="rgb(255,0,37)" text-anchor="middle" transform="rotate(0.000000 77.569700,147.975985)" >3.908</text> </g>
  Visible = false
  X = 0
  Y = 0
  arrowL1 = 3
  arrowL2 = 1
  arrowW = 2
  arrow_scheme = 0
  autoPlaceOffset = 2
  autoPlaceText = true
  click1_x = 77.3273
  click1_y = 149.976
  click2_x = 77.3273
  click2_y = 149.976
  comma_decimal_place = false
  dimension_line_overshoot = 1
  gap_datum_points = 2
  halfDimension_linear = false
  lineColor = rgb(0,0,255)
  strokeWidth = 0.5
  textFormat_linear = %(value)3.3f
  textRenderer_color = rgb(255,0,37)
  textRenderer_family = inherit
  textRenderer_size = 3.2
  unit_custom_scale = 1
  unit_scheme = 0
FEATURE [Drawing::FeatureViewPython] dim050  # drawing view (typed FeaturePython)
  Rotation = 0
  ViewResult = <g> \n  <line x1="42.639000" y1="189.063000" x2="31.985443" y2="189.063000" style="stroke:rgb(0,0,255);stroke-width:0.50" />\n<line x1="42.639000" y1="41.937000" x2="31.985443" y2="41.937000" style="stroke:rgb(0,0,255);stroke-width:0.50" />\n<line x1="32.985443" y1="189.063000" x2="32.985443" y2="41.937000" style="stroke:rgb(0,0,255);stroke-width:0.50" /> \n  <polygon points="32.985443,41.937000 31.985443,44.937000 32.985443,45.937000 33.985443,44.937000" style="fill:rgb(0,0,255);stroke:rgb(0,0,255);stroke-width:0" /><polygon points="32.985443,189.063000 33.985443,186.063000 32.985443,185.063000 31.985443,186.063000" style="fill:rgb(0,0,255);stroke:rgb(0,0,255);stroke-width:0" /> \n  <text x="30.985443" y="115.500000" font-family="inherit" font-size="3.2" fill="rgb(255,0,37)" text-anchor="middle" transform="rotate(-90.000000 30.985443,115.500000)" >98.084</text> </g>
  Visible = false
  X = 0
  Y = 0
  arrowL1 = 3
  arrowL2 = 1
  arrowW = 2
  arrow_scheme = 0
  autoPlaceOffset = 2
  autoPlaceText = true
  click1_x = 32.9854
  click1_y = 131.554
  click2_x = 32.9854
  click2_y = 131.554
  comma_decimal_place = false
  dimension_line_overshoot = 1
  gap_datum_points = 2
  halfDimension_linear = false
  lineColor = rgb(0,0,255)
  strokeWidth = 0.5
  textFormat_linear = %(value)3.3f
  textRenderer_color = rgb(255,0,37)
  textRenderer_family = inherit
  textRenderer_size = 3.2
  unit_custom_scale = 1
  unit_scheme = 0
FEATURE [Drawing::FeatureViewPython] dim051  # drawing view (typed FeaturePython)
  Rotation = 0
  ViewResult = <g> \n  <line x1="76.000400" y1="191.063000" x2="76.000400" y2="208.226193" style="stroke:rgb(0,0,255);stroke-width:0.50" />\n<line x1="44.639000" y1="191.063000" x2="44.639000" y2="208.226193" style="stroke:rgb(0,0,255);stroke-width:0.50" />\n<line x1="76.000400" y1="207.226193" x2="44.639000" y2="207.226193" style="stroke:rgb(0,0,255);stroke-width:0.50" /> \n  <polygon points="44.639000,207.226193 47.639000,208.226193 48.639000,207.226193 47.639000,206.226193" style="fill:rgb(0,0,255);stroke:rgb(0,0,255);stroke-width:0" /><polygon points="76.000400,207.226193 73.000400,206.226193 72.000400,207.226193 73.000400,208.226193" style="fill:rgb(0,0,255);stroke:rgb(0,0,255);stroke-width:0" /> \n  <text x="60.319700" y="205.226193" font-family="inherit" font-size="3.2" fill="rgb(255,0,37)" text-anchor="middle" transform="rotate(0.000000 60.319700,205.226193)" >20.908</text> </g>
  Visible = false
  X = 0
  Y = 0
  arrowL1 = 3
  arrowL2 = 1
  arrowW = 2
  arrow_scheme = 0
  autoPlaceOffset = 2
  autoPlaceText = true
  click1_x = 64.8067
  click1_y = 207.226
  click2_x = 64.8067
  click2_y = 207.226
  comma_decimal_place = false
  dimension_line_overshoot = 1
  gap_datum_points = 2
  halfDimension_linear = false
  lineColor = rgb(0,0,255)
  strokeWidth = 0.5
  textFormat_linear = %(value)3.3f
  textRenderer_color = rgb(255,0,37)
  textRenderer_family = inherit
  textRenderer_size = 3.2
  unit_custom_scale = 1
  unit_scheme = 0
FEATURE [Drawing::FeatureViewPython] dim052  # drawing view (typed FeaturePython)
  Rotation = 0
  ViewResult = <g> \n  <line x1="77.414614" y1="187.648786" x2="146.821048" y2="118.242352" style="stroke:rgb(0,0,255);stroke-width:0.50" />\n<line x1="143.414614" y1="253.648786" x2="212.821048" y2="184.242352" style="stroke:rgb(0,0,255);stroke-width:0.50" />\n<line x1="146.113941" y1="118.949459" x2="212.113941" y2="184.949459" style="stroke:rgb(0,0,255);stroke-width:0.50" /> \n  <polygon points="212.113941,184.949459 210.699728,182.121032 209.285514,182.121032 209.285514,183.535245" style="fill:rgb(0,0,255);stroke:rgb(0,0,255);stroke-width:0" /><polygon points="146.113941,118.949459 147.528155,121.777886 148.942368,121.777886 148.942368,120.363672" style="fill:rgb(0,0,255);stroke:rgb(0,0,255);stroke-width:0" /> \n  <text x="177.699728" y="150.535245" font-family="inherit" font-size="3.2" fill="rgb(255,0,37)" text-anchor="middle" transform="rotate(-45.000000 177.699728,150.535245)" >62.225</text> </g>
  Visible = false
  X = 0
  Y = 0
  arrowL1 = 3
  arrowL2 = 1
  arrowW = 2
  arrow_scheme = 0
  autoPlaceOffset = 2
  autoPlaceText = true
  click1_x = 181.614
  click1_y = 154.449
  click2_x = 181.614
  click2_y = 154.449
  comma_decimal_place = false
  dimension_line_overshoot = 1
  gap_datum_points = 2
  halfDimension_linear = false
  lineColor = rgb(0,0,255)
  strokeWidth = 0.5
  textFormat_linear = %(value)3.3f
  textRenderer_color = rgb(255,0,37)
  textRenderer_family = inherit
  textRenderer_size = 3.2
  unit_custom_scale = 1
  unit_scheme = 0
FEATURE [Drawing::FeatureViewPython] dim053  # drawing view (typed FeaturePython)
  Rotation = 0
  ViewResult = <g> \n  <line x1="152.305960" y1="215.297905" x2="183.690891" y2="178.875887" style="stroke:rgb(0,0,255);stroke-width:0.50" />\n<line x1="81.805960" y1="154.547905" x2="113.190891" y2="118.125887" style="stroke:rgb(0,0,255);stroke-width:0.50" />\n<line x1="183.038111" y1="179.633434" x2="112.538111" y2="118.883434" style="stroke:rgb(0,0,255);stroke-width:0.50" /> \n  <polygon points="112.538111,118.883434 114.157973,121.599322 115.568301,121.494555 115.463533,120.084227" style="fill:rgb(0,0,255);stroke:rgb(0,0,255);stroke-width:0" /><polygon points="183.038111,179.633434 181.418249,176.917546 180.007922,177.022313 180.112689,178.432641" style="fill:rgb(0,0,255);stroke:rgb(0,0,255);stroke-width:0" /> \n  <text x="146.273016" y="147.952874" font-family="inherit" font-size="3.2" fill="rgb(255,0,37)" text-anchor="middle" transform="rotate(-49.248455 146.273016,147.952874)" >62.042</text> </g>
  Visible = false
  X = 0
  Y = 0
  arrowL1 = 3
  arrowL2 = 1
  arrowW = 2
  arrow_scheme = 0
  autoPlaceOffset = 2
  autoPlaceText = true
  click1_x = 155.614
  click1_y = 156.002
  click2_x = 155.614
  click2_y = 156.002
  comma_decimal_place = false
  dimension_line_overshoot = 1
  gap_datum_points = 2
  halfDimension_linear = false
  lineColor = rgb(0,0,255)
  strokeWidth = 0.5
  textFormat_linear = %(value)3.3f
  textRenderer_color = rgb(255,0,37)
  textRenderer_family = inherit
  textRenderer_size = 3.2
  unit_custom_scale = 1
  unit_scheme = 0
FEATURE [Drawing::FeatureViewPython] dim054  # drawing view (typed FeaturePython)
  Rotation = 0
  ViewResult = <g> \n  <line x1="185.361650" y1="214.813000" x2="185.361650" y2="198.464912" style="stroke:rgb(0,0,255);stroke-width:0.50" />\n<line x1="151.000400" y1="214.813000" x2="151.000400" y2="198.464912" style="stroke:rgb(0,0,255);stroke-width:0.50" />\n<line x1="185.361650" y1="199.464912" x2="151.000400" y2="199.464912" style="stroke:rgb(0,0,255);stroke-width:0.50" /> \n  <polygon points="151.000400,199.464912 154.000400,200.464912 155.000400,199.464912 154.000400,198.464912" style="fill:rgb(0,0,255);stroke:rgb(0,0,255);stroke-width:0" /><polygon points="185.361650,199.464912 182.361650,198.464912 181.361650,199.464912 182.361650,200.464912" style="fill:rgb(0,0,255);stroke:rgb(0,0,255);stroke-width:0" /> \n  <text x="168.181025" y="197.464912" font-family="inherit" font-size="3.2" fill="rgb(255,0,37)" text-anchor="middle" transform="rotate(0.000000 168.181025,197.464912)" >22.907</text> </g>
  Visible = false
  X = 0
  Y = 0
  arrowL1 = 3
  arrowL2 = 1
  arrowW = 2
  arrow_scheme = 0
  autoPlaceOffset = 2
  autoPlaceText = true
  click1_x = 172.688
  click1_y = 199.465
  click2_x = 172.688
  click2_y = 199.465
  comma_decimal_place = false
  dimension_line_overshoot = 1
  gap_datum_points = 2
  halfDimension_linear = false
  lineColor = rgb(0,0,255)
  strokeWidth = 0.5
  textFormat_linear = %(value)3.3f
  textRenderer_color = rgb(255,0,37)
  textRenderer_family = inherit
  textRenderer_size = 3.2
  unit_custom_scale = 1
  unit_scheme = 0
FEATURE [Drawing::FeatureViewPython] dim055  # drawing view (typed FeaturePython)
  Rotation = 0
  ViewResult = <g> \n  <line x1="187.361650" y1="255.063000" x2="200.852976" y2="255.063000" style="stroke:rgb(0,0,255);stroke-width:0.50" />\n<line x1="187.361650" y1="216.813000" x2="200.852976" y2="216.813000" style="stroke:rgb(0,0,255);stroke-width:0.50" />\n<line x1="199.852976" y1="255.063000" x2="199.852976" y2="216.813000" style="stroke:rgb(0,0,255);stroke-width:0.50" /> \n  <polygon points="199.852976,216.813000 198.852976,219.813000 199.852976,220.813000 200.852976,219.813000" style="fill:rgb(0,0,255);stroke:rgb(0,0,255);stroke-width:0" /><polygon points="199.852976,255.063000 200.852976,252.063000 199.852976,251.063000 198.852976,252.063000" style="fill:rgb(0,0,255);stroke:rgb(0,0,255);stroke-width:0" /> \n  <text x="197.852976" y="235.938000" font-family="inherit" font-size="3.2" fill="rgb(255,0,37)" text-anchor="middle" transform="rotate(-90.000000 197.852976,235.938000)" >25.5</text> </g>
  Visible = false
  X = 0
  Y = 0
  arrowL1 = 3
  arrowL2 = 1
  arrowW = 2
  arrow_scheme = 0
  autoPlaceOffset = 2
  autoPlaceText = true
  click1_x = 199.853
  click1_y = 228.958
  click2_x = 199.853
  click2_y = 228.958
  comma_decimal_place = false
  dimension_line_overshoot = 1
  gap_datum_points = 2
  halfDimension_linear = false
  lineColor = rgb(0,0,255)
  strokeWidth = 0.5
  textFormat_linear = %(value)3.3f
  textRenderer_color = rgb(255,0,37)
  textRenderer_family = inherit
  textRenderer_size = 3.2
  unit_custom_scale = 1
  unit_scheme = 0
FEATURE [Drawing::FeatureViewPython] dim056  # drawing view (typed FeaturePython)
  Rotation = 0
  ViewResult = <g> \n  <line x1="142.000400" y1="257.063000" x2="142.000400" y2="266.823861" style="stroke:rgb(0,0,255);stroke-width:0.50" />\n<line x1="185.361650" y1="257.063000" x2="185.361650" y2="266.823861" style="stroke:rgb(0,0,255);stroke-width:0.50" />\n<line x1="142.000400" y1="265.823861" x2="185.361650" y2="265.823861" style="stroke:rgb(0,0,255);stroke-width:0.50" /> \n  <polygon points="185.361650,265.823861 182.361650,264.823861 181.361650,265.823861 182.361650,266.823861" style="fill:rgb(0,0,255);stroke:rgb(0,0,255);stroke-width:0" /><polygon points="142.000400,265.823861 145.000400,266.823861 146.000400,265.823861 145.000400,264.823861" style="fill:rgb(0,0,255);stroke:rgb(0,0,255);stroke-width:0" /> \n  <text x="163.681025" y="263.823861" font-family="inherit" font-size="3.2" fill="rgb(255,0,37)" text-anchor="middle" transform="rotate(0.000000 163.681025,263.823861)" >28.907</text> </g>
  Visible = false
  X = 0
  Y = 0
  arrowL1 = 3
  arrowL2 = 1
  arrowW = 2
  arrow_scheme = 0
  autoPlaceOffset = 2
  autoPlaceText = true
  click1_x = 173.077
  click1_y = 265.824
  click2_x = 173.077
  click2_y = 265.824
  comma_decimal_place = false
  dimension_line_overshoot = 1
  gap_datum_points = 2
  halfDimension_linear = false
  lineColor = rgb(0,0,255)
  strokeWidth = 0.5
  textFormat_linear = %(value)3.3f
  textRenderer_color = rgb(255,0,37)
  textRenderer_family = inherit
  textRenderer_size = 3.2
  unit_custom_scale = 1
  unit_scheme = 0
FEATURE [Drawing::FeaturePage] Page009
  EditableTexts = AUTHOR NAME | CREATION DATE | SUPERVISOR NAME | CHECK DATE | SCALE | WEIGHT | NUMBER | SHEET | TITLE | SUBTITLE
  Group = -> [Ortho033,dim047,dim048,dim049,dim050,dim051,dim052,dim053,dim054,dim055,dim056]
  Template = <path>
note: 11 file-system paths scrubbed to <path> (originals preserved in the JSON sidecar)
